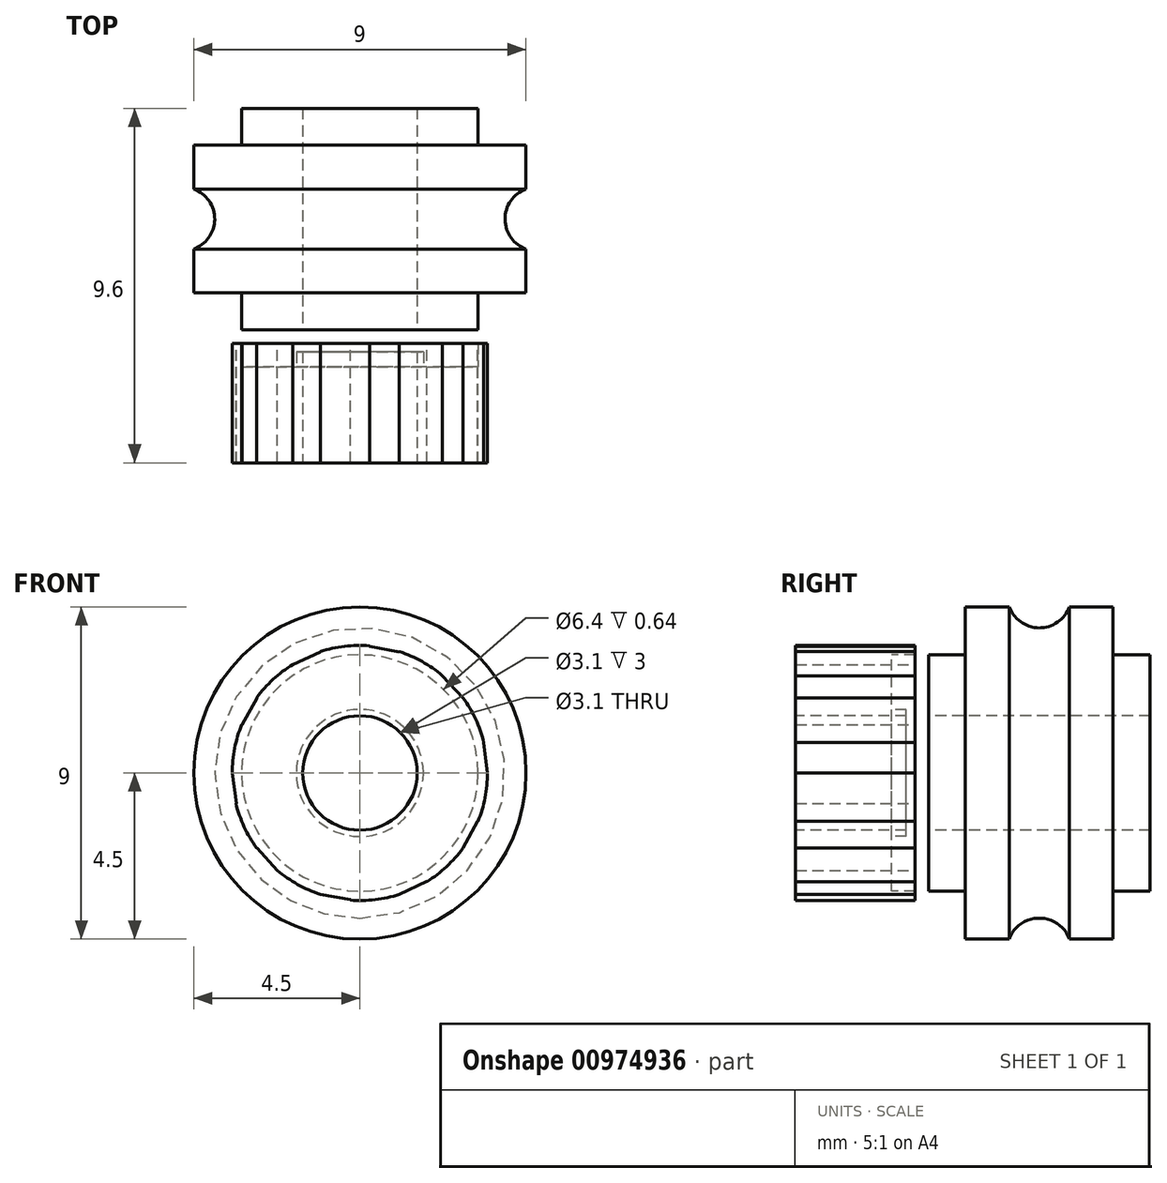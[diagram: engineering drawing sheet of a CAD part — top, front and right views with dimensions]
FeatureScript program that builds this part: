
annotation { "Feature Type Name" : "Feature", "Feature Type Description" : "" }
export const myFeature = defineFeature(function(context is Context, id is Id, definition is map)
    precondition{}
    {
        {
            var Q0;
            Q0=qCreatedBy(makeId("Front.planeOp"),FACE);
            var sketch = newSketch(context, id + "F0", { "sketchPlane" : qUnion([Q0])});
            skCircle(sketch, "E0", {"center": v(0, 0) * mm, "radius": 1.5 * mm});
            skCircle(sketch, "E1", {"center": v(0, 0) * mm, "radius": 4.5 * mm});
            skSolve(sketch);
        }
        {
            var Q0;
            Q0=makeQuery(id+"F0.imprint","IMPRINT",FACE,{"disambiguationData":[TD([[makeQuery(id+"F0.imprint","IMPRINT",EDGE,{"derivedFrom":sQuery(id+"F0.wireOp",EDGE,"E0")}),-1.0]])]});
            extrude(context, id + "F1", {"entities" : qUnion([Q0]), "endBound" : BoundingType.SYMMETRIC, "depth" : 11 * mm});
        }
        {
            var Q0;
            Q0=qCreatedBy(makeId("Right.planeOp"),FACE);
            var sketch = newSketch(context, id + "F2", { "sketchPlane" : qUnion([Q0])});
            skLineSegment(sketch, "E2", {"start": v(5.5, 0) * mm, "end": v(-5.5, 0) * mm, "construction": true});
            skLineSegment(sketch, "E3", {"start": v(3.2, 0) * mm, "end": v(3.2, 4.5) * mm});
            skLineSegment(sketch, "E4", {"start": v(-2.16, 4.5) * mm, "end": v(-0.84, 4.5) * mm, "construction": true});
            skPoint(sketch, "E5", {"position": v(-1.5, 4.6) * mm});
            skCircle(sketch, "E6", {"center": v(-1.5, 4.8) * mm, "radius": 0.87 * mm});
            skSolve(sketch);
        }
        {
            var Q0;
            Q0=makeQuery(id+"F2.imprint","IMPRINT",FACE,{"disambiguationData":[TD([[makeQuery(id+"F2.imprint","IMPRINT",EDGE,{"derivedFrom":sQuery(id+"F2.wireOp",EDGE,"jA4JG8t2-koIH-J3Tn-0CPV-hgkhpaPEa3mh")}),1.0]])]});
            var Q1;
            Q1=makeQuery(id+"F2.imprint","IMPRINT",FACE,{"disambiguationData":[TD([[makeQuery(id+"F2.imprint","IMPRINT",EDGE,{"derivedFrom":sQuery(id+"F2.wireOp",EDGE,"E6")}),1.0]])]});
            var Q2;
            Q2=sQuery(id+"F2.wireOp",EDGE,"E2");
            revolve(context, id + "F3", {"operationType" : NewBodyOperationType.REMOVE, "surfaceOperationType" : NewSurfaceOperationType.NEW, "entities" : qUnion([Q0, Q1]), "axis" : qUnion([Q2]), "revolveType" : RevolveType.FULL, "oppositeDirection" : true});
        }
        {
            var Q0;
            Q0=sQuery(id+"F2.wireOp",VERTEX,"E3.end");
            var Q1;
            Q1=sQuery(id+"F2.wireOp",EDGE,"E3");
            cPlane(context, id + "F4", {"entities" : qUnion([Q0, Q1]), "cplaneType" : CPlaneType.LINE_POINT, "offset" : 25 * mm, "width" : 150 * mm, "height" : 150 * mm});
        }
        {
            var Q0;
            Q0=qCreatedBy(id+"F4.planeOp",FACE);
            var sketch = newSketch(context, id + "F5", { "sketchPlane" : qUnion([Q0])});
            skPoint(sketch, "E7.0", {"position": v(0, 3.2) * mm});
            skSolve(sketch);
        }
        {
            var Q0;
            Q0=makeQuery(id+"F1.opExtrude","CAP_FACE",FACE,{"disambiguationData":[OSD([sQuery(id+"F0.wireOp",EDGE,"E0"),sQuery(id+"F0.wireOp",EDGE,"E1")])],"isStart":false});
            var sketch = newSketch(context, id + "F6", { "sketchPlane" : qUnion([Q0])});
            skPoint(sketch, "E8.center", {"position": v(0, 0) * mm});
            skCircle(sketch, "E9", {"center": v(0, 0) * mm, "radius": 2.24 * mm});
            skArc(sketch, "E10", {"start": v(2.65, 3.64) * mm, "mid": v(1.1, 3.37) * mm, "end": v(0, 2.24) * mm});
            skArc(sketch, "E11", {"start": v(2.65, 3.64) * mm, "mid": v(1.73, 2.67) * mm, "end": v(1.79, 1.34) * mm});
            skArc(sketch, "E12.1.0", {"start": v(0, 4.5) * mm, "mid": v(-1.09, 3.37) * mm, "end": v(-1.31, 1.8) * mm});
            skArc(sketch, "E12.1.1", {"start": v(0, 4.5) * mm, "mid": v(-0.17, 3.18) * mm, "end": v(0.66, 2.14) * mm});
            skArc(sketch, "E12.2.0", {"start": v(-2.64, 3.64) * mm, "mid": v(-2.86, 2.08) * mm, "end": v(-2.13, 0.7) * mm});
            skArc(sketch, "E12.2.1", {"start": v(-2.64, 3.64) * mm, "mid": v(-2, 2.48) * mm, "end": v(-0.72, 2.12) * mm});
            skArc(sketch, "E12.3.0", {"start": v(-4.28, 1.4) * mm, "mid": v(-3.54, 0) * mm, "end": v(-2.13, -0.7) * mm});
            skArc(sketch, "E12.3.1", {"start": v(-4.28, 1.4) * mm, "mid": v(-3.08, 0.82) * mm, "end": v(-1.83, 1.29) * mm});
            skArc(sketch, "E12.4.0", {"start": v(-4.28, -1.38) * mm, "mid": v(-2.87, -2.08) * mm, "end": v(-1.31, -1.8) * mm});
            skArc(sketch, "E12.4.1", {"start": v(-4.28, -1.38) * mm, "mid": v(-2.97, -1.14) * mm, "end": v(-2.24, -0.03) * mm});
            skArc(sketch, "E12.5.0", {"start": v(-2.65, -3.64) * mm, "mid": v(-1.1, -3.37) * mm, "end": v(0, -2.24) * mm});
            skArc(sketch, "E12.5.1", {"start": v(-2.65, -3.64) * mm, "mid": v(-1.73, -2.67) * mm, "end": v(-1.79, -1.34) * mm});
            skArc(sketch, "E12.6.0", {"start": v(0, -4.5) * mm, "mid": v(1.09, -3.37) * mm, "end": v(1.31, -1.8) * mm});
            skArc(sketch, "E12.6.1", {"start": v(0, -4.5) * mm, "mid": v(0.17, -3.18) * mm, "end": v(-0.66, -2.14) * mm});
            skArc(sketch, "E12.7.0", {"start": v(2.64, -3.64) * mm, "mid": v(2.86, -2.08) * mm, "end": v(2.13, -0.7) * mm});
            skArc(sketch, "E12.7.1", {"start": v(2.64, -3.64) * mm, "mid": v(2, -2.48) * mm, "end": v(0.72, -2.12) * mm});
            skArc(sketch, "E12.8.0", {"start": v(4.28, -1.4) * mm, "mid": v(3.54, 0) * mm, "end": v(2.13, 0.7) * mm});
            skArc(sketch, "E12.8.1", {"start": v(4.28, -1.4) * mm, "mid": v(3.08, -0.82) * mm, "end": v(1.83, -1.29) * mm});
            skArc(sketch, "E12.9.0", {"start": v(4.28, 1.38) * mm, "mid": v(2.87, 2.08) * mm, "end": v(1.31, 1.8) * mm});
            skArc(sketch, "E12.9.1", {"start": v(4.28, 1.38) * mm, "mid": v(2.97, 1.14) * mm, "end": v(2.24, 0.03) * mm});
            skSolve(sketch);
        }
        {
            var Q0;
            {var subQ0=sQuery(id+"F6.wireOp",EDGE,"E12.2.0");var subQ3=sQuery(id+"F6.wireOp",EDGE,"E12.3.1");var subQ4=makeQuery(id+"F6.imprint","INTERSECT",VERTEX,{"derivedFrom":[subQ0,subQ3]});Q0=makeQuery(id+"F6.imprint","IMPRINT",FACE,{"disambiguationData":[TD([[makeQuery(id+"F6.imprint","IMPRINT",EDGE,{"disambiguationData":[TD([[subQ4,1.0]])],"derivedFrom":subQ0}),-1.0]])]});}
            var Q1;
            {var subQ0=sQuery(id+"F6.wireOp",EDGE,"E12.1.0");var subQ3=sQuery(id+"F6.wireOp",EDGE,"E12.2.1");var subQ4=makeQuery(id+"F6.imprint","INTERSECT",VERTEX,{"derivedFrom":[subQ0,subQ3]});Q1=makeQuery(id+"F6.imprint","IMPRINT",FACE,{"disambiguationData":[TD([[makeQuery(id+"F6.imprint","IMPRINT",EDGE,{"disambiguationData":[TD([[subQ4,1.0]])],"derivedFrom":subQ0}),-1.0]])]});}
            var Q2;
            {var subQ0=sQuery(id+"F6.wireOp",EDGE,"E10");var subQ3=sQuery(id+"F6.wireOp",EDGE,"E12.1.1");var subQ4=makeQuery(id+"F6.imprint","INTERSECT",VERTEX,{"derivedFrom":[subQ0,subQ3]});Q2=makeQuery(id+"F6.imprint","IMPRINT",FACE,{"disambiguationData":[TD([[makeQuery(id+"F6.imprint","IMPRINT",EDGE,{"disambiguationData":[TD([[subQ4,1.0]])],"derivedFrom":subQ0}),-1.0]])]});}
            var Q3;
            {var subQ0=sQuery(id+"F6.wireOp",EDGE,"E11");var subQ3=sQuery(id+"F6.wireOp",EDGE,"E12.9.0");var subQ4=makeQuery(id+"F6.imprint","INTERSECT",VERTEX,{"derivedFrom":[subQ0,subQ3]});Q3=makeQuery(id+"F6.imprint","IMPRINT",FACE,{"disambiguationData":[TD([[makeQuery(id+"F6.imprint","IMPRINT",EDGE,{"disambiguationData":[TD([[subQ4,1.0]])],"derivedFrom":subQ0}),1.0]])]});}
            var Q4;
            {var subQ0=sQuery(id+"F6.wireOp",EDGE,"E12.8.0");var subQ3=sQuery(id+"F6.wireOp",EDGE,"E12.9.1");var subQ4=makeQuery(id+"F6.imprint","INTERSECT",VERTEX,{"derivedFrom":[subQ0,subQ3]});Q4=makeQuery(id+"F6.imprint","IMPRINT",FACE,{"disambiguationData":[TD([[makeQuery(id+"F6.imprint","IMPRINT",EDGE,{"disambiguationData":[TD([[subQ4,1.0]])],"derivedFrom":subQ0}),-1.0]])]});}
            var Q5;
            {var subQ0=sQuery(id+"F6.wireOp",EDGE,"E12.7.0");var subQ3=sQuery(id+"F6.wireOp",EDGE,"E12.8.1");var subQ4=makeQuery(id+"F6.imprint","INTERSECT",VERTEX,{"derivedFrom":[subQ0,subQ3]});Q5=makeQuery(id+"F6.imprint","IMPRINT",FACE,{"disambiguationData":[TD([[makeQuery(id+"F6.imprint","IMPRINT",EDGE,{"disambiguationData":[TD([[subQ4,1.0]])],"derivedFrom":subQ0}),-1.0]])]});}
            var Q6;
            {var subQ0=sQuery(id+"F6.wireOp",EDGE,"E12.6.0");var subQ3=sQuery(id+"F6.wireOp",EDGE,"E12.7.1");var subQ4=makeQuery(id+"F6.imprint","INTERSECT",VERTEX,{"derivedFrom":[subQ0,subQ3]});Q6=makeQuery(id+"F6.imprint","IMPRINT",FACE,{"disambiguationData":[TD([[makeQuery(id+"F6.imprint","IMPRINT",EDGE,{"disambiguationData":[TD([[subQ4,1.0]])],"derivedFrom":subQ0}),-1.0]])]});}
            var Q7;
            {var subQ0=sQuery(id+"F6.wireOp",EDGE,"E12.5.0");var subQ3=sQuery(id+"F6.wireOp",EDGE,"E12.6.1");var subQ4=makeQuery(id+"F6.imprint","INTERSECT",VERTEX,{"derivedFrom":[subQ0,subQ3]});Q7=makeQuery(id+"F6.imprint","IMPRINT",FACE,{"disambiguationData":[TD([[makeQuery(id+"F6.imprint","IMPRINT",EDGE,{"disambiguationData":[TD([[subQ4,1.0]])],"derivedFrom":subQ0}),-1.0]])]});}
            var Q8;
            {var subQ0=sQuery(id+"F6.wireOp",EDGE,"E12.4.0");var subQ3=sQuery(id+"F6.wireOp",EDGE,"E12.5.1");var subQ4=makeQuery(id+"F6.imprint","INTERSECT",VERTEX,{"derivedFrom":[subQ0,subQ3]});Q8=makeQuery(id+"F6.imprint","IMPRINT",FACE,{"disambiguationData":[TD([[makeQuery(id+"F6.imprint","IMPRINT",EDGE,{"disambiguationData":[TD([[subQ4,1.0]])],"derivedFrom":subQ0}),-1.0]])]});}
            var Q9;
            {var subQ0=sQuery(id+"F6.wireOp",EDGE,"E12.3.0");var subQ3=sQuery(id+"F6.wireOp",EDGE,"E12.4.1");var subQ4=makeQuery(id+"F6.imprint","INTERSECT",VERTEX,{"derivedFrom":[subQ0,subQ3]});Q9=makeQuery(id+"F6.imprint","IMPRINT",FACE,{"disambiguationData":[TD([[makeQuery(id+"F6.imprint","IMPRINT",EDGE,{"disambiguationData":[TD([[subQ4,1.0]])],"derivedFrom":subQ0}),-1.0]])]});}
            extrude(context, id + "F7", {"entities" : qUnion([Q0, Q1, Q2, Q3, Q4, Q5, Q6, Q7, Q8, Q9]), "operationType" : NewBodyOperationType.ADD, "oppositeDirection" : true, "depth" : 2 * mm, "offsetDistance" : 25 * mm});
        }
        {
            var Q0;
            Q0=makeQuery(id+"F1.opExtrude","CAP_FACE",FACE,{"disambiguationData":[OSD([sQuery(id+"F0.wireOp",EDGE,"E0"),sQuery(id+"F0.wireOp",EDGE,"E1")])],"isStart":true});
            var sketch = newSketch(context, id + "F8", { "sketchPlane" : qUnion([Q0])});
            skCircle(sketch, "E13", {"center": v(0, 0) * mm, "radius": 3.2 * mm});
            skSolve(sketch);
        }
        {
            var Q0;
            Q0=makeQuery(id+"F8.imprint","IMPRINT",FACE,{"disambiguationData":[TD([[makeQuery(id+"F8.imprint","IMPRINT",EDGE,{"derivedFrom":sQuery(id+"F8.wireOp",EDGE,"E13")}),-1.0]])]});
            extrude(context, id + "F9", {"entities" : qUnion([Q0]), "operationType" : NewBodyOperationType.REMOVE, "oppositeDirection" : true, "depth" : 5 * mm, "offsetDistance" : 25 * mm});
        }
        {
            var Q0;
            Q0=makeQuery(id+"F1.opExtrude","CAP_FACE",FACE,{"disambiguationData":[OSD([sQuery(id+"F0.wireOp",EDGE,"E0"),sQuery(id+"F0.wireOp",EDGE,"E1")])],"isStart":true});
            var sketch = newSketch(context, id + "F10", { "sketchPlane" : qUnion([Q0])});
            skLineSegment(sketch, "E14", {"start": v(3.6, 0.87) * mm, "end": v(3.1, 0.76) * mm});
            skLineSegment(sketch, "E15", {"start": v(3.6, 0.88) * mm, "end": v(3.6, 0.87) * mm});
            skLineSegment(sketch, "E16", {"start": v(3.6, 0.88) * mm, "end": v(3.6, 0.88) * mm});
            skLineSegment(sketch, "E17", {"start": v(3.62, 0.88) * mm, "end": v(3.6, 0.88) * mm});
            skLineSegment(sketch, "E18", {"start": v(3.63, 0.9) * mm, "end": v(3.62, 0.88) * mm});
            skLineSegment(sketch, "E19", {"start": v(3.65, 0.9) * mm, "end": v(3.63, 0.9) * mm});
            skLineSegment(sketch, "E20", {"start": v(3.68, 0.91) * mm, "end": v(3.65, 0.9) * mm});
            skLineSegment(sketch, "E21", {"start": v(3.7, 0.93) * mm, "end": v(3.68, 0.91) * mm});
            skLineSegment(sketch, "E22", {"start": v(3.74, 0.94) * mm, "end": v(3.7, 0.93) * mm});
            skLineSegment(sketch, "E23", {"start": v(3.77, 0.96) * mm, "end": v(3.74, 0.94) * mm});
            skLineSegment(sketch, "E24", {"start": v(3.8, 0.99) * mm, "end": v(3.77, 0.96) * mm});
            skLineSegment(sketch, "E25", {"start": v(3.85, 1.02) * mm, "end": v(3.8, 0.99) * mm});
            skLineSegment(sketch, "E26", {"start": v(3.9, 1.05) * mm, "end": v(3.85, 1.02) * mm});
            skLineSegment(sketch, "E27", {"start": v(3.94, 1.09) * mm, "end": v(3.9, 1.05) * mm});
            skLineSegment(sketch, "E28", {"start": v(3.98, 1.13) * mm, "end": v(3.94, 1.09) * mm});
            skLineSegment(sketch, "E29", {"start": v(4.03, 1.18) * mm, "end": v(3.98, 1.13) * mm});
            skLineSegment(sketch, "E30", {"start": v(4.08, 1.23) * mm, "end": v(4.03, 1.18) * mm});
            skLineSegment(sketch, "E31", {"start": v(4.14, 1.29) * mm, "end": v(4.08, 1.23) * mm});
            skLineSegment(sketch, "E32", {"start": v(4.19, 1.35) * mm, "end": v(4.14, 1.29) * mm});
            skLineSegment(sketch, "E33", {"start": v(4.24, 1.41) * mm, "end": v(4.19, 1.35) * mm});
            skLineSegment(sketch, "E34", {"start": v(4.3, 1.49) * mm, "end": v(4.24, 1.41) * mm});
            skLineSegment(sketch, "E35", {"start": v(4.35, 1.57) * mm, "end": v(4.3, 1.49) * mm});
            skLineSegment(sketch, "E36", {"start": v(4.4, 1.65) * mm, "end": v(4.35, 1.57) * mm});
            skLineSegment(sketch, "E37", {"start": v(4.45, 1.74) * mm, "end": v(4.4, 1.65) * mm});
            skLineSegment(sketch, "E38", {"start": v(4.5, 1.83) * mm, "end": v(4.45, 1.74) * mm});
            skLineSegment(sketch, "E39", {"start": v(4.55, 1.93) * mm, "end": v(4.5, 1.83) * mm});
            skLineSegment(sketch, "E40", {"start": v(4.55, 2.02) * mm, "end": v(4.55, 1.93) * mm});
            skLineSegment(sketch, "E41", {"start": v(4.48, 2.16) * mm, "end": v(4.55, 2.02) * mm});
            skLineSegment(sketch, "E42", {"start": v(4.42, 2.22) * mm, "end": v(4.48, 2.16) * mm});
            skLineSegment(sketch, "E43", {"start": v(4.31, 2.25) * mm, "end": v(4.42, 2.22) * mm});
            skLineSegment(sketch, "E44", {"start": v(4.2, 2.27) * mm, "end": v(4.31, 2.25) * mm});
            skLineSegment(sketch, "E45", {"start": v(4.1, 2.29) * mm, "end": v(4.2, 2.27) * mm});
            skLineSegment(sketch, "E46", {"start": v(4, 2.3) * mm, "end": v(4.1, 2.29) * mm});
            skLineSegment(sketch, "E47", {"start": v(3.91, 2.31) * mm, "end": v(4, 2.3) * mm});
            skLineSegment(sketch, "E48", {"start": v(3.82, 2.32) * mm, "end": v(3.91, 2.31) * mm});
            skLineSegment(sketch, "E49", {"start": v(3.74, 2.32) * mm, "end": v(3.82, 2.32) * mm});
            skLineSegment(sketch, "E50", {"start": v(3.66, 2.32) * mm, "end": v(3.74, 2.32) * mm});
            skLineSegment(sketch, "E51", {"start": v(3.58, 2.32) * mm, "end": v(3.66, 2.32) * mm});
            skLineSegment(sketch, "E52", {"start": v(3.5, 2.31) * mm, "end": v(3.58, 2.32) * mm});
            skLineSegment(sketch, "E53", {"start": v(3.44, 2.3) * mm, "end": v(3.5, 2.31) * mm});
            skLineSegment(sketch, "E54", {"start": v(3.38, 2.3) * mm, "end": v(3.44, 2.3) * mm});
            skLineSegment(sketch, "E55", {"start": v(3.32, 2.29) * mm, "end": v(3.38, 2.3) * mm});
            skLineSegment(sketch, "E56", {"start": v(3.27, 2.28) * mm, "end": v(3.32, 2.29) * mm});
            skLineSegment(sketch, "E57", {"start": v(3.22, 2.26) * mm, "end": v(3.27, 2.28) * mm});
            skLineSegment(sketch, "E58", {"start": v(3.18, 2.25) * mm, "end": v(3.22, 2.26) * mm});
            skLineSegment(sketch, "E59", {"start": v(3.14, 2.24) * mm, "end": v(3.18, 2.25) * mm});
            skLineSegment(sketch, "E60", {"start": v(3.1, 2.23) * mm, "end": v(3.14, 2.24) * mm});
            skLineSegment(sketch, "E61", {"start": v(3.07, 2.22) * mm, "end": v(3.1, 2.23) * mm});
            skLineSegment(sketch, "E62", {"start": v(3.05, 2.2) * mm, "end": v(3.07, 2.22) * mm});
            skLineSegment(sketch, "E63", {"start": v(3.03, 2.2) * mm, "end": v(3.05, 2.2) * mm});
            skLineSegment(sketch, "E64", {"start": v(3.01, 2.19) * mm, "end": v(3.03, 2.2) * mm});
            skLineSegment(sketch, "E65", {"start": v(3, 2.18) * mm, "end": v(3.01, 2.19) * mm});
            skLineSegment(sketch, "E66", {"start": v(3, 2.18) * mm, "end": v(3, 2.18) * mm});
            skLineSegment(sketch, "E67", {"start": v(3, 2.17) * mm, "end": v(3, 2.18) * mm});
            skLineSegment(sketch, "E68", {"start": v(2.58, 1.88) * mm, "end": v(3, 2.17) * mm});
            skLineSegment(sketch, "E69", {"start": v(2.07, 2.44) * mm, "end": v(2.58, 1.88) * mm});
            skLineSegment(sketch, "E70", {"start": v(2.4, 2.82) * mm, "end": v(2.07, 2.44) * mm});
            skLineSegment(sketch, "E71", {"start": v(2.4, 2.82) * mm, "end": v(2.4, 2.82) * mm});
            skLineSegment(sketch, "E72", {"start": v(2.4, 2.83) * mm, "end": v(2.4, 2.82) * mm});
            skLineSegment(sketch, "E73", {"start": v(2.4, 2.84) * mm, "end": v(2.4, 2.83) * mm});
            skLineSegment(sketch, "E74", {"start": v(2.42, 2.86) * mm, "end": v(2.4, 2.84) * mm});
            skLineSegment(sketch, "E75", {"start": v(2.43, 2.88) * mm, "end": v(2.42, 2.86) * mm});
            skLineSegment(sketch, "E76", {"start": v(2.44, 2.9) * mm, "end": v(2.43, 2.88) * mm});
            skLineSegment(sketch, "E77", {"start": v(2.45, 2.93) * mm, "end": v(2.44, 2.9) * mm});
            skLineSegment(sketch, "E78", {"start": v(2.47, 2.96) * mm, "end": v(2.45, 2.93) * mm});
            skLineSegment(sketch, "E79", {"start": v(2.48, 3) * mm, "end": v(2.47, 2.96) * mm});
            skLineSegment(sketch, "E80", {"start": v(2.5, 3.04) * mm, "end": v(2.48, 3) * mm});
            skLineSegment(sketch, "E81", {"start": v(2.52, 3.09) * mm, "end": v(2.5, 3.04) * mm});
            skLineSegment(sketch, "E82", {"start": v(2.53, 3.14) * mm, "end": v(2.52, 3.09) * mm});
            skLineSegment(sketch, "E83", {"start": v(2.55, 3.2) * mm, "end": v(2.53, 3.14) * mm});
            skLineSegment(sketch, "E84", {"start": v(2.56, 3.26) * mm, "end": v(2.55, 3.2) * mm});
            skLineSegment(sketch, "E85", {"start": v(2.57, 3.32) * mm, "end": v(2.56, 3.26) * mm});
            skLineSegment(sketch, "E86", {"start": v(2.58, 3.4) * mm, "end": v(2.57, 3.32) * mm});
            skLineSegment(sketch, "E87", {"start": v(2.59, 3.47) * mm, "end": v(2.58, 3.4) * mm});
            skLineSegment(sketch, "E88", {"start": v(2.6, 3.55) * mm, "end": v(2.59, 3.47) * mm});
            skLineSegment(sketch, "E89", {"start": v(2.6, 3.64) * mm, "end": v(2.6, 3.55) * mm});
            skLineSegment(sketch, "E90", {"start": v(2.6, 3.73) * mm, "end": v(2.6, 3.64) * mm});
            skLineSegment(sketch, "E91", {"start": v(2.6, 3.82) * mm, "end": v(2.6, 3.73) * mm});
            skLineSegment(sketch, "E92", {"start": v(2.6, 3.92) * mm, "end": v(2.6, 3.82) * mm});
            skLineSegment(sketch, "E93", {"start": v(2.58, 4.02) * mm, "end": v(2.6, 3.92) * mm});
            skLineSegment(sketch, "E94", {"start": v(2.57, 4.13) * mm, "end": v(2.58, 4.02) * mm});
            skLineSegment(sketch, "E95", {"start": v(2.55, 4.24) * mm, "end": v(2.57, 4.13) * mm});
            skLineSegment(sketch, "E96", {"start": v(2.5, 4.3) * mm, "end": v(2.55, 4.24) * mm});
            skLineSegment(sketch, "E97", {"start": v(2.35, 4.39) * mm, "end": v(2.5, 4.3) * mm});
            skLineSegment(sketch, "E98", {"start": v(2.27, 4.4) * mm, "end": v(2.35, 4.39) * mm});
            skLineSegment(sketch, "E99", {"start": v(2.17, 4.35) * mm, "end": v(2.27, 4.4) * mm});
            skLineSegment(sketch, "E100", {"start": v(2.07, 4.3) * mm, "end": v(2.17, 4.35) * mm});
            skLineSegment(sketch, "E101", {"start": v(1.98, 4.26) * mm, "end": v(2.07, 4.3) * mm});
            skLineSegment(sketch, "E102", {"start": v(1.89, 4.22) * mm, "end": v(1.98, 4.26) * mm});
            skLineSegment(sketch, "E103", {"start": v(1.8, 4.17) * mm, "end": v(1.89, 4.22) * mm});
            skLineSegment(sketch, "E104", {"start": v(1.73, 4.12) * mm, "end": v(1.8, 4.17) * mm});
            skLineSegment(sketch, "E105", {"start": v(1.66, 4.07) * mm, "end": v(1.73, 4.12) * mm});
            skLineSegment(sketch, "E106", {"start": v(1.6, 4.03) * mm, "end": v(1.66, 4.07) * mm});
            skLineSegment(sketch, "E107", {"start": v(1.53, 3.98) * mm, "end": v(1.6, 4.03) * mm});
            skLineSegment(sketch, "E108", {"start": v(1.48, 3.93) * mm, "end": v(1.53, 3.98) * mm});
            skLineSegment(sketch, "E109", {"start": v(1.43, 3.89) * mm, "end": v(1.48, 3.93) * mm});
            skLineSegment(sketch, "E110", {"start": v(1.38, 3.84) * mm, "end": v(1.43, 3.89) * mm});
            skLineSegment(sketch, "E111", {"start": v(1.34, 3.8) * mm, "end": v(1.38, 3.84) * mm});
            skLineSegment(sketch, "E112", {"start": v(1.3, 3.76) * mm, "end": v(1.34, 3.8) * mm});
            skLineSegment(sketch, "E113", {"start": v(1.27, 3.72) * mm, "end": v(1.3, 3.76) * mm});
            skLineSegment(sketch, "E114", {"start": v(1.25, 3.69) * mm, "end": v(1.27, 3.72) * mm});
            skLineSegment(sketch, "E115", {"start": v(1.22, 3.66) * mm, "end": v(1.25, 3.69) * mm});
            skLineSegment(sketch, "E116", {"start": v(1.2, 3.63) * mm, "end": v(1.22, 3.66) * mm});
            skLineSegment(sketch, "E117", {"start": v(1.18, 3.6) * mm, "end": v(1.2, 3.63) * mm});
            skLineSegment(sketch, "E118", {"start": v(1.17, 3.58) * mm, "end": v(1.18, 3.6) * mm});
            skLineSegment(sketch, "E119", {"start": v(1.16, 3.56) * mm, "end": v(1.17, 3.58) * mm});
            skLineSegment(sketch, "E120", {"start": v(1.15, 3.54) * mm, "end": v(1.16, 3.56) * mm});
            skLineSegment(sketch, "E121", {"start": v(1.15, 3.53) * mm, "end": v(1.15, 3.54) * mm});
            skLineSegment(sketch, "E122", {"start": v(1.14, 3.52) * mm, "end": v(1.15, 3.53) * mm});
            skLineSegment(sketch, "E123", {"start": v(1.14, 3.52) * mm, "end": v(1.14, 3.52) * mm});
            skLineSegment(sketch, "E124", {"start": v(0.99, 3.04) * mm, "end": v(1.14, 3.52) * mm});
            skLineSegment(sketch, "E125", {"start": v(0.24, 3.18) * mm, "end": v(0.99, 3.04) * mm});
            skLineSegment(sketch, "E126", {"start": v(0.28, 3.69) * mm, "end": v(0.24, 3.18) * mm});
            skLineSegment(sketch, "E127", {"start": v(0.28, 3.7) * mm, "end": v(0.28, 3.69) * mm});
            skLineSegment(sketch, "E128", {"start": v(0.28, 3.7) * mm, "end": v(0.28, 3.7) * mm});
            skLineSegment(sketch, "E129", {"start": v(0.28, 3.71) * mm, "end": v(0.28, 3.7) * mm});
            skLineSegment(sketch, "E130", {"start": v(0.28, 3.73) * mm, "end": v(0.28, 3.71) * mm});
            skLineSegment(sketch, "E131", {"start": v(0.27, 3.75) * mm, "end": v(0.28, 3.73) * mm});
            skLineSegment(sketch, "E132", {"start": v(0.27, 3.78) * mm, "end": v(0.27, 3.75) * mm});
            skLineSegment(sketch, "E133", {"start": v(0.27, 3.81) * mm, "end": v(0.27, 3.78) * mm});
            skLineSegment(sketch, "E134", {"start": v(0.26, 3.85) * mm, "end": v(0.27, 3.81) * mm});
            skLineSegment(sketch, "E135", {"start": v(0.25, 3.89) * mm, "end": v(0.26, 3.85) * mm});
            skLineSegment(sketch, "E136", {"start": v(0.24, 3.93) * mm, "end": v(0.25, 3.89) * mm});
            skLineSegment(sketch, "E137", {"start": v(0.22, 3.98) * mm, "end": v(0.24, 3.93) * mm});
            skLineSegment(sketch, "E138", {"start": v(0.2, 4.03) * mm, "end": v(0.22, 3.98) * mm});
            skLineSegment(sketch, "E139", {"start": v(0.18, 4.08) * mm, "end": v(0.2, 4.03) * mm});
            skLineSegment(sketch, "E140", {"start": v(0.16, 4.14) * mm, "end": v(0.18, 4.08) * mm});
            skLineSegment(sketch, "E141", {"start": v(0.13, 4.2) * mm, "end": v(0.16, 4.14) * mm});
            skLineSegment(sketch, "E142", {"start": v(0.1, 4.26) * mm, "end": v(0.13, 4.2) * mm});
            skLineSegment(sketch, "E143", {"start": v(0.05, 4.33) * mm, "end": v(0.1, 4.26) * mm});
            skLineSegment(sketch, "E144", {"start": v(0.01, 4.4) * mm, "end": v(0.05, 4.33) * mm});
            skLineSegment(sketch, "E145", {"start": v(-0.04, 4.47) * mm, "end": v(0.01, 4.4) * mm});
            skLineSegment(sketch, "E146", {"start": v(-0.09, 4.54) * mm, "end": v(-0.04, 4.47) * mm});
            skLineSegment(sketch, "E147", {"start": v(-0.15, 4.62) * mm, "end": v(-0.09, 4.54) * mm});
            skLineSegment(sketch, "E148", {"start": v(-0.2, 4.7) * mm, "end": v(-0.15, 4.62) * mm});
            skLineSegment(sketch, "E149", {"start": v(-0.28, 4.77) * mm, "end": v(-0.2, 4.7) * mm});
            skLineSegment(sketch, "E150", {"start": v(-0.35, 4.85) * mm, "end": v(-0.28, 4.77) * mm});
            skLineSegment(sketch, "E151", {"start": v(-0.43, 4.93) * mm, "end": v(-0.35, 4.85) * mm});
            skLineSegment(sketch, "E152", {"start": v(-0.51, 4.95) * mm, "end": v(-0.43, 4.93) * mm});
            skLineSegment(sketch, "E153", {"start": v(-0.67, 4.93) * mm, "end": v(-0.51, 4.95) * mm});
            skLineSegment(sketch, "E154", {"start": v(-0.75, 4.9) * mm, "end": v(-0.67, 4.93) * mm});
            skLineSegment(sketch, "E155", {"start": v(-0.8, 4.8) * mm, "end": v(-0.75, 4.9) * mm});
            skLineSegment(sketch, "E156", {"start": v(-0.86, 4.7) * mm, "end": v(-0.8, 4.8) * mm});
            skLineSegment(sketch, "E157", {"start": v(-0.9, 4.61) * mm, "end": v(-0.86, 4.7) * mm});
            skLineSegment(sketch, "E158", {"start": v(-0.95, 4.52) * mm, "end": v(-0.9, 4.61) * mm});
            skLineSegment(sketch, "E159", {"start": v(-1, 4.44) * mm, "end": v(-0.95, 4.52) * mm});
            skLineSegment(sketch, "E160", {"start": v(-1.02, 4.35) * mm, "end": v(-1, 4.44) * mm});
            skLineSegment(sketch, "E161", {"start": v(-1.05, 4.27) * mm, "end": v(-1.02, 4.35) * mm});
            skLineSegment(sketch, "E162", {"start": v(-1.08, 4.2) * mm, "end": v(-1.05, 4.27) * mm});
            skLineSegment(sketch, "E163", {"start": v(-1.1, 4.12) * mm, "end": v(-1.08, 4.2) * mm});
            skLineSegment(sketch, "E164", {"start": v(-1.12, 4.05) * mm, "end": v(-1.1, 4.12) * mm});
            skLineSegment(sketch, "E165", {"start": v(-1.13, 3.98) * mm, "end": v(-1.12, 4.05) * mm});
            skLineSegment(sketch, "E166", {"start": v(-1.14, 3.92) * mm, "end": v(-1.13, 3.98) * mm});
            skLineSegment(sketch, "E167", {"start": v(-1.15, 3.86) * mm, "end": v(-1.14, 3.92) * mm});
            skLineSegment(sketch, "E168", {"start": v(-1.16, 3.81) * mm, "end": v(-1.15, 3.86) * mm});
            skLineSegment(sketch, "E169", {"start": v(-1.16, 3.76) * mm, "end": v(-1.16, 3.81) * mm});
            skLineSegment(sketch, "E170", {"start": v(-1.16, 3.72) * mm, "end": v(-1.16, 3.76) * mm});
            skLineSegment(sketch, "E171", {"start": v(-1.16, 3.68) * mm, "end": v(-1.16, 3.72) * mm});
            skLineSegment(sketch, "E172", {"start": v(-1.16, 3.64) * mm, "end": v(-1.16, 3.68) * mm});
            skLineSegment(sketch, "E173", {"start": v(-1.16, 3.6) * mm, "end": v(-1.16, 3.64) * mm});
            skLineSegment(sketch, "E174", {"start": v(-1.15, 3.58) * mm, "end": v(-1.16, 3.6) * mm});
            skLineSegment(sketch, "E175", {"start": v(-1.15, 3.56) * mm, "end": v(-1.15, 3.58) * mm});
            skLineSegment(sketch, "E176", {"start": v(-1.15, 3.54) * mm, "end": v(-1.15, 3.56) * mm});
            skLineSegment(sketch, "E177", {"start": v(-1.15, 3.53) * mm, "end": v(-1.15, 3.54) * mm});
            skLineSegment(sketch, "E178", {"start": v(-1.14, 3.52) * mm, "end": v(-1.15, 3.53) * mm});
            skLineSegment(sketch, "E179", {"start": v(-1.14, 3.52) * mm, "end": v(-1.14, 3.52) * mm});
            skLineSegment(sketch, "E180", {"start": v(-0.99, 3.04) * mm, "end": v(-1.14, 3.52) * mm});
            skLineSegment(sketch, "E181", {"start": v(-1.68, 2.72) * mm, "end": v(-0.99, 3.04) * mm});
            skLineSegment(sketch, "E182", {"start": v(-1.94, 3.15) * mm, "end": v(-1.68, 2.72) * mm});
            skLineSegment(sketch, "E183", {"start": v(-1.94, 3.15) * mm, "end": v(-1.94, 3.15) * mm});
            skLineSegment(sketch, "E184", {"start": v(-1.95, 3.16) * mm, "end": v(-1.94, 3.15) * mm});
            skLineSegment(sketch, "E185", {"start": v(-1.96, 3.17) * mm, "end": v(-1.95, 3.16) * mm});
            skLineSegment(sketch, "E186", {"start": v(-1.97, 3.18) * mm, "end": v(-1.96, 3.17) * mm});
            skLineSegment(sketch, "E187", {"start": v(-1.98, 3.2) * mm, "end": v(-1.97, 3.18) * mm});
            skLineSegment(sketch, "E188", {"start": v(-2, 3.22) * mm, "end": v(-1.98, 3.2) * mm});
            skLineSegment(sketch, "E189", {"start": v(-2.03, 3.24) * mm, "end": v(-2, 3.22) * mm});
            skLineSegment(sketch, "E190", {"start": v(-2.05, 3.26) * mm, "end": v(-2.03, 3.24) * mm});
            skLineSegment(sketch, "E191", {"start": v(-2.08, 3.29) * mm, "end": v(-2.05, 3.26) * mm});
            skLineSegment(sketch, "E192", {"start": v(-2.12, 3.32) * mm, "end": v(-2.08, 3.29) * mm});
            skLineSegment(sketch, "E193", {"start": v(-2.16, 3.35) * mm, "end": v(-2.12, 3.32) * mm});
            skLineSegment(sketch, "E194", {"start": v(-2.2, 3.38) * mm, "end": v(-2.16, 3.35) * mm});
            skLineSegment(sketch, "E195", {"start": v(-2.25, 3.4) * mm, "end": v(-2.2, 3.38) * mm});
            skLineSegment(sketch, "E196", {"start": v(-2.3, 3.44) * mm, "end": v(-2.25, 3.4) * mm});
            skLineSegment(sketch, "E197", {"start": v(-2.37, 3.47) * mm, "end": v(-2.3, 3.44) * mm});
            skLineSegment(sketch, "E198", {"start": v(-2.43, 3.5) * mm, "end": v(-2.37, 3.47) * mm});
            skLineSegment(sketch, "E199", {"start": v(-2.5, 3.54) * mm, "end": v(-2.43, 3.5) * mm});
            skLineSegment(sketch, "E200", {"start": v(-2.58, 3.57) * mm, "end": v(-2.5, 3.54) * mm});
            skLineSegment(sketch, "E201", {"start": v(-2.66, 3.6) * mm, "end": v(-2.58, 3.57) * mm});
            skLineSegment(sketch, "E202", {"start": v(-2.74, 3.62) * mm, "end": v(-2.66, 3.6) * mm});
            skLineSegment(sketch, "E203", {"start": v(-2.83, 3.65) * mm, "end": v(-2.74, 3.62) * mm});
            skLineSegment(sketch, "E204", {"start": v(-2.93, 3.68) * mm, "end": v(-2.83, 3.65) * mm});
            skLineSegment(sketch, "E205", {"start": v(-3.03, 3.7) * mm, "end": v(-2.93, 3.68) * mm});
            skLineSegment(sketch, "E206", {"start": v(-3.14, 3.72) * mm, "end": v(-3.03, 3.7) * mm});
            skLineSegment(sketch, "E207", {"start": v(-3.25, 3.73) * mm, "end": v(-3.14, 3.72) * mm});
            skLineSegment(sketch, "E208", {"start": v(-3.33, 3.7) * mm, "end": v(-3.25, 3.73) * mm});
            skLineSegment(sketch, "E209", {"start": v(-3.44, 3.6) * mm, "end": v(-3.33, 3.7) * mm});
            skLineSegment(sketch, "E210", {"start": v(-3.48, 3.52) * mm, "end": v(-3.44, 3.6) * mm});
            skLineSegment(sketch, "E211", {"start": v(-3.47, 3.4) * mm, "end": v(-3.48, 3.52) * mm});
            skLineSegment(sketch, "E212", {"start": v(-3.46, 3.3) * mm, "end": v(-3.47, 3.4) * mm});
            skLineSegment(sketch, "E213", {"start": v(-3.45, 3.2) * mm, "end": v(-3.46, 3.3) * mm});
            skLineSegment(sketch, "E214", {"start": v(-3.43, 3.1) * mm, "end": v(-3.45, 3.2) * mm});
            skLineSegment(sketch, "E215", {"start": v(-3.4, 3) * mm, "end": v(-3.43, 3.1) * mm});
            skLineSegment(sketch, "E216", {"start": v(-3.39, 2.92) * mm, "end": v(-3.4, 3) * mm});
            skLineSegment(sketch, "E217", {"start": v(-3.36, 2.84) * mm, "end": v(-3.39, 2.92) * mm});
            skLineSegment(sketch, "E218", {"start": v(-3.34, 2.76) * mm, "end": v(-3.36, 2.84) * mm});
            skLineSegment(sketch, "E219", {"start": v(-3.31, 2.69) * mm, "end": v(-3.34, 2.76) * mm});
            skLineSegment(sketch, "E220", {"start": v(-3.28, 2.62) * mm, "end": v(-3.31, 2.69) * mm});
            skLineSegment(sketch, "E221", {"start": v(-3.26, 2.56) * mm, "end": v(-3.28, 2.62) * mm});
            skLineSegment(sketch, "E222", {"start": v(-3.23, 2.5) * mm, "end": v(-3.26, 2.56) * mm});
            skLineSegment(sketch, "E223", {"start": v(-3.2, 2.45) * mm, "end": v(-3.23, 2.5) * mm});
            skLineSegment(sketch, "E224", {"start": v(-3.18, 2.4) * mm, "end": v(-3.2, 2.45) * mm});
            skLineSegment(sketch, "E225", {"start": v(-3.15, 2.36) * mm, "end": v(-3.18, 2.4) * mm});
            skLineSegment(sketch, "E226", {"start": v(-3.12, 2.32) * mm, "end": v(-3.15, 2.36) * mm});
            skLineSegment(sketch, "E227", {"start": v(-3.1, 2.3) * mm, "end": v(-3.12, 2.32) * mm});
            skLineSegment(sketch, "E228", {"start": v(-3.08, 2.26) * mm, "end": v(-3.1, 2.3) * mm});
            skLineSegment(sketch, "E229", {"start": v(-3.06, 2.24) * mm, "end": v(-3.08, 2.26) * mm});
            skLineSegment(sketch, "E230", {"start": v(-3.04, 2.22) * mm, "end": v(-3.06, 2.24) * mm});
            skLineSegment(sketch, "E231", {"start": v(-3.02, 2.2) * mm, "end": v(-3.04, 2.22) * mm});
            skLineSegment(sketch, "E232", {"start": v(-3.01, 2.2) * mm, "end": v(-3.02, 2.2) * mm});
            skLineSegment(sketch, "E233", {"start": v(-3, 2.18) * mm, "end": v(-3.01, 2.2) * mm});
            skLineSegment(sketch, "E234", {"start": v(-3, 2.18) * mm, "end": v(-3, 2.18) * mm});
            skLineSegment(sketch, "E235", {"start": v(-3, 2.17) * mm, "end": v(-3, 2.18) * mm});
            skLineSegment(sketch, "E236", {"start": v(-2.58, 1.88) * mm, "end": v(-3, 2.17) * mm});
            skLineSegment(sketch, "E237", {"start": v(-2.95, 1.21) * mm, "end": v(-2.58, 1.88) * mm});
            skLineSegment(sketch, "E238", {"start": v(-3.42, 1.4) * mm, "end": v(-2.95, 1.21) * mm});
            skLineSegment(sketch, "E239", {"start": v(-3.42, 1.4) * mm, "end": v(-3.42, 1.4) * mm});
            skLineSegment(sketch, "E240", {"start": v(-3.43, 1.4) * mm, "end": v(-3.42, 1.4) * mm});
            skLineSegment(sketch, "E241", {"start": v(-3.45, 1.41) * mm, "end": v(-3.43, 1.4) * mm});
            skLineSegment(sketch, "E242", {"start": v(-3.46, 1.42) * mm, "end": v(-3.45, 1.41) * mm});
            skLineSegment(sketch, "E243", {"start": v(-3.48, 1.42) * mm, "end": v(-3.46, 1.42) * mm});
            skLineSegment(sketch, "E244", {"start": v(-3.51, 1.43) * mm, "end": v(-3.48, 1.42) * mm});
            skLineSegment(sketch, "E245", {"start": v(-3.54, 1.43) * mm, "end": v(-3.51, 1.43) * mm});
            skLineSegment(sketch, "E246", {"start": v(-3.58, 1.43) * mm, "end": v(-3.54, 1.43) * mm});
            skLineSegment(sketch, "E247", {"start": v(-3.62, 1.44) * mm, "end": v(-3.58, 1.43) * mm});
            skLineSegment(sketch, "E248", {"start": v(-3.66, 1.44) * mm, "end": v(-3.62, 1.44) * mm});
            skLineSegment(sketch, "E249", {"start": v(-3.71, 1.44) * mm, "end": v(-3.66, 1.44) * mm});
            skLineSegment(sketch, "E250", {"start": v(-3.77, 1.44) * mm, "end": v(-3.71, 1.44) * mm});
            skLineSegment(sketch, "E251", {"start": v(-3.83, 1.43) * mm, "end": v(-3.77, 1.44) * mm});
            skLineSegment(sketch, "E252", {"start": v(-3.89, 1.43) * mm, "end": v(-3.83, 1.43) * mm});
            skLineSegment(sketch, "E253", {"start": v(-3.96, 1.42) * mm, "end": v(-3.89, 1.43) * mm});
            skLineSegment(sketch, "E254", {"start": v(-4.03, 1.4) * mm, "end": v(-3.96, 1.42) * mm});
            skLineSegment(sketch, "E255", {"start": v(-4.1, 1.4) * mm, "end": v(-4.03, 1.4) * mm});
            skLineSegment(sketch, "E256", {"start": v(-4.18, 1.37) * mm, "end": v(-4.1, 1.4) * mm});
            skLineSegment(sketch, "E257", {"start": v(-4.26, 1.35) * mm, "end": v(-4.18, 1.37) * mm});
            skLineSegment(sketch, "E258", {"start": v(-4.35, 1.32) * mm, "end": v(-4.26, 1.35) * mm});
            skLineSegment(sketch, "E259", {"start": v(-4.44, 1.29) * mm, "end": v(-4.35, 1.32) * mm});
            skLineSegment(sketch, "E260", {"start": v(-4.53, 1.25) * mm, "end": v(-4.44, 1.29) * mm});
            skLineSegment(sketch, "E261", {"start": v(-4.62, 1.21) * mm, "end": v(-4.53, 1.25) * mm});
            skLineSegment(sketch, "E262", {"start": v(-4.72, 1.16) * mm, "end": v(-4.62, 1.21) * mm});
            skLineSegment(sketch, "E263", {"start": v(-4.82, 1.11) * mm, "end": v(-4.72, 1.16) * mm});
            skLineSegment(sketch, "E264", {"start": v(-4.87, 1.04) * mm, "end": v(-4.82, 1.11) * mm});
            skLineSegment(sketch, "E265", {"start": v(-4.9, 0.88) * mm, "end": v(-4.87, 1.04) * mm});
            skLineSegment(sketch, "E266", {"start": v(-4.88, 0.8) * mm, "end": v(-4.9, 0.88) * mm});
            skLineSegment(sketch, "E267", {"start": v(-4.8, 0.72) * mm, "end": v(-4.88, 0.8) * mm});
            skLineSegment(sketch, "E268", {"start": v(-4.74, 0.64) * mm, "end": v(-4.8, 0.72) * mm});
            skLineSegment(sketch, "E269", {"start": v(-4.67, 0.56) * mm, "end": v(-4.74, 0.64) * mm});
            skLineSegment(sketch, "E270", {"start": v(-4.6, 0.5) * mm, "end": v(-4.67, 0.56) * mm});
            skLineSegment(sketch, "E271", {"start": v(-4.52, 0.43) * mm, "end": v(-4.6, 0.5) * mm});
            skLineSegment(sketch, "E272", {"start": v(-4.46, 0.37) * mm, "end": v(-4.52, 0.43) * mm});
            skLineSegment(sketch, "E273", {"start": v(-4.39, 0.32) * mm, "end": v(-4.46, 0.37) * mm});
            skLineSegment(sketch, "E274", {"start": v(-4.32, 0.27) * mm, "end": v(-4.39, 0.32) * mm});
            skLineSegment(sketch, "E275", {"start": v(-4.26, 0.23) * mm, "end": v(-4.32, 0.27) * mm});
            skLineSegment(sketch, "E276", {"start": v(-4.2, 0.19) * mm, "end": v(-4.26, 0.23) * mm});
            skLineSegment(sketch, "E277", {"start": v(-4.14, 0.16) * mm, "end": v(-4.2, 0.19) * mm});
            skLineSegment(sketch, "E278", {"start": v(-4.08, 0.13) * mm, "end": v(-4.14, 0.16) * mm});
            skLineSegment(sketch, "E279", {"start": v(-4.03, 0.1) * mm, "end": v(-4.08, 0.13) * mm});
            skLineSegment(sketch, "E280", {"start": v(-3.98, 0.08) * mm, "end": v(-4.03, 0.1) * mm});
            skLineSegment(sketch, "E281", {"start": v(-3.94, 0.06) * mm, "end": v(-3.98, 0.08) * mm});
            skLineSegment(sketch, "E282", {"start": v(-3.9, 0.04) * mm, "end": v(-3.94, 0.06) * mm});
            skLineSegment(sketch, "E283", {"start": v(-3.85, 0.03) * mm, "end": v(-3.9, 0.04) * mm});
            skLineSegment(sketch, "E284", {"start": v(-3.82, 0.02) * mm, "end": v(-3.85, 0.03) * mm});
            skLineSegment(sketch, "E285", {"start": v(-3.79, 0.01) * mm, "end": v(-3.82, 0.02) * mm});
            skLineSegment(sketch, "E286", {"start": v(-3.76, 0) * mm, "end": v(-3.79, 0.01) * mm});
            skLineSegment(sketch, "E287", {"start": v(-3.74, 0) * mm, "end": v(-3.76, 0) * mm});
            skLineSegment(sketch, "E288", {"start": v(-3.72, 0) * mm, "end": v(-3.74, 0) * mm});
            skLineSegment(sketch, "E289", {"start": v(-3.7, 0) * mm, "end": v(-3.72, 0) * mm});
            skLineSegment(sketch, "E290", {"start": v(-3.7, 0) * mm, "end": v(-3.7, 0) * mm});
            skLineSegment(sketch, "E291", {"start": v(-3.2, 0) * mm, "end": v(-3.7, 0) * mm});
            skLineSegment(sketch, "E292", {"start": v(-3.1, -0.76) * mm, "end": v(-3.2, 0) * mm});
            skLineSegment(sketch, "E293", {"start": v(-3.6, -0.87) * mm, "end": v(-3.1, -0.76) * mm});
            skLineSegment(sketch, "E294", {"start": v(-3.6, -0.88) * mm, "end": v(-3.6, -0.87) * mm});
            skLineSegment(sketch, "E295", {"start": v(-3.6, -0.88) * mm, "end": v(-3.6, -0.88) * mm});
            skLineSegment(sketch, "E296", {"start": v(-3.62, -0.88) * mm, "end": v(-3.6, -0.88) * mm});
            skLineSegment(sketch, "E297", {"start": v(-3.63, -0.9) * mm, "end": v(-3.62, -0.88) * mm});
            skLineSegment(sketch, "E298", {"start": v(-3.65, -0.9) * mm, "end": v(-3.63, -0.9) * mm});
            skLineSegment(sketch, "E299", {"start": v(-3.68, -0.91) * mm, "end": v(-3.65, -0.9) * mm});
            skLineSegment(sketch, "E300", {"start": v(-3.7, -0.93) * mm, "end": v(-3.68, -0.91) * mm});
            skLineSegment(sketch, "E301", {"start": v(-3.74, -0.94) * mm, "end": v(-3.7, -0.93) * mm});
            skLineSegment(sketch, "E302", {"start": v(-3.77, -0.96) * mm, "end": v(-3.74, -0.94) * mm});
            skLineSegment(sketch, "E303", {"start": v(-3.8, -0.99) * mm, "end": v(-3.77, -0.96) * mm});
            skLineSegment(sketch, "E304", {"start": v(-3.85, -1.02) * mm, "end": v(-3.8, -0.99) * mm});
            skLineSegment(sketch, "E305", {"start": v(-3.9, -1.05) * mm, "end": v(-3.85, -1.02) * mm});
            skLineSegment(sketch, "E306", {"start": v(-3.94, -1.09) * mm, "end": v(-3.9, -1.05) * mm});
            skLineSegment(sketch, "E307", {"start": v(-3.98, -1.13) * mm, "end": v(-3.94, -1.09) * mm});
            skLineSegment(sketch, "E308", {"start": v(-4.03, -1.18) * mm, "end": v(-3.98, -1.13) * mm});
            skLineSegment(sketch, "E309", {"start": v(-4.08, -1.23) * mm, "end": v(-4.03, -1.18) * mm});
            skLineSegment(sketch, "E310", {"start": v(-4.14, -1.29) * mm, "end": v(-4.08, -1.23) * mm});
            skLineSegment(sketch, "E311", {"start": v(-4.19, -1.35) * mm, "end": v(-4.14, -1.29) * mm});
            skLineSegment(sketch, "E312", {"start": v(-4.24, -1.41) * mm, "end": v(-4.19, -1.35) * mm});
            skLineSegment(sketch, "E313", {"start": v(-4.3, -1.49) * mm, "end": v(-4.24, -1.41) * mm});
            skLineSegment(sketch, "E314", {"start": v(-4.35, -1.57) * mm, "end": v(-4.3, -1.49) * mm});
            skLineSegment(sketch, "E315", {"start": v(-4.4, -1.65) * mm, "end": v(-4.35, -1.57) * mm});
            skLineSegment(sketch, "E316", {"start": v(-4.45, -1.74) * mm, "end": v(-4.4, -1.65) * mm});
            skLineSegment(sketch, "E317", {"start": v(-4.5, -1.83) * mm, "end": v(-4.45, -1.74) * mm});
            skLineSegment(sketch, "E318", {"start": v(-4.55, -1.93) * mm, "end": v(-4.5, -1.83) * mm});
            skLineSegment(sketch, "E319", {"start": v(-4.55, -2.02) * mm, "end": v(-4.55, -1.93) * mm});
            skLineSegment(sketch, "E320", {"start": v(-4.48, -2.16) * mm, "end": v(-4.55, -2.02) * mm});
            skLineSegment(sketch, "E321", {"start": v(-4.42, -2.22) * mm, "end": v(-4.48, -2.16) * mm});
            skLineSegment(sketch, "E322", {"start": v(-4.31, -2.25) * mm, "end": v(-4.42, -2.22) * mm});
            skLineSegment(sketch, "E323", {"start": v(-4.2, -2.27) * mm, "end": v(-4.31, -2.25) * mm});
            skLineSegment(sketch, "E324", {"start": v(-4.1, -2.29) * mm, "end": v(-4.2, -2.27) * mm});
            skLineSegment(sketch, "E325", {"start": v(-4, -2.3) * mm, "end": v(-4.1, -2.29) * mm});
            skLineSegment(sketch, "E326", {"start": v(-3.91, -2.31) * mm, "end": v(-4, -2.3) * mm});
            skLineSegment(sketch, "E327", {"start": v(-3.82, -2.32) * mm, "end": v(-3.91, -2.31) * mm});
            skLineSegment(sketch, "E328", {"start": v(-3.74, -2.32) * mm, "end": v(-3.82, -2.32) * mm});
            skLineSegment(sketch, "E329", {"start": v(-3.66, -2.32) * mm, "end": v(-3.74, -2.32) * mm});
            skLineSegment(sketch, "E330", {"start": v(-3.58, -2.32) * mm, "end": v(-3.66, -2.32) * mm});
            skLineSegment(sketch, "E331", {"start": v(-3.5, -2.31) * mm, "end": v(-3.58, -2.32) * mm});
            skLineSegment(sketch, "E332", {"start": v(-3.44, -2.3) * mm, "end": v(-3.5, -2.31) * mm});
            skLineSegment(sketch, "E333", {"start": v(-3.38, -2.3) * mm, "end": v(-3.44, -2.3) * mm});
            skLineSegment(sketch, "E334", {"start": v(-3.32, -2.29) * mm, "end": v(-3.38, -2.3) * mm});
            skLineSegment(sketch, "E335", {"start": v(-3.27, -2.28) * mm, "end": v(-3.32, -2.29) * mm});
            skLineSegment(sketch, "E336", {"start": v(-3.22, -2.26) * mm, "end": v(-3.27, -2.28) * mm});
            skLineSegment(sketch, "E337", {"start": v(-3.18, -2.25) * mm, "end": v(-3.22, -2.26) * mm});
            skLineSegment(sketch, "E338", {"start": v(-3.14, -2.24) * mm, "end": v(-3.18, -2.25) * mm});
            skLineSegment(sketch, "E339", {"start": v(-3.1, -2.23) * mm, "end": v(-3.14, -2.24) * mm});
            skLineSegment(sketch, "E340", {"start": v(-3.07, -2.22) * mm, "end": v(-3.1, -2.23) * mm});
            skLineSegment(sketch, "E341", {"start": v(-3.05, -2.2) * mm, "end": v(-3.07, -2.22) * mm});
            skLineSegment(sketch, "E342", {"start": v(-3.03, -2.2) * mm, "end": v(-3.05, -2.2) * mm});
            skLineSegment(sketch, "E343", {"start": v(-3.01, -2.19) * mm, "end": v(-3.03, -2.2) * mm});
            skLineSegment(sketch, "E344", {"start": v(-3, -2.18) * mm, "end": v(-3.01, -2.19) * mm});
            skLineSegment(sketch, "E345", {"start": v(-3, -2.18) * mm, "end": v(-3, -2.18) * mm});
            skLineSegment(sketch, "E346", {"start": v(-3, -2.17) * mm, "end": v(-3, -2.18) * mm});
            skLineSegment(sketch, "E347", {"start": v(-2.58, -1.88) * mm, "end": v(-3, -2.17) * mm});
            skLineSegment(sketch, "E348", {"start": v(-2.07, -2.44) * mm, "end": v(-2.58, -1.88) * mm});
            skLineSegment(sketch, "E349", {"start": v(-2.4, -2.82) * mm, "end": v(-2.07, -2.44) * mm});
            skLineSegment(sketch, "E350", {"start": v(-2.4, -2.82) * mm, "end": v(-2.4, -2.82) * mm});
            skLineSegment(sketch, "E351", {"start": v(-2.4, -2.83) * mm, "end": v(-2.4, -2.82) * mm});
            skLineSegment(sketch, "E352", {"start": v(-2.4, -2.84) * mm, "end": v(-2.4, -2.83) * mm});
            skLineSegment(sketch, "E353", {"start": v(-2.42, -2.86) * mm, "end": v(-2.4, -2.84) * mm});
            skLineSegment(sketch, "E354", {"start": v(-2.43, -2.88) * mm, "end": v(-2.42, -2.86) * mm});
            skLineSegment(sketch, "E355", {"start": v(-2.44, -2.9) * mm, "end": v(-2.43, -2.88) * mm});
            skLineSegment(sketch, "E356", {"start": v(-2.45, -2.93) * mm, "end": v(-2.44, -2.9) * mm});
            skLineSegment(sketch, "E357", {"start": v(-2.47, -2.96) * mm, "end": v(-2.45, -2.93) * mm});
            skLineSegment(sketch, "E358", {"start": v(-2.48, -3) * mm, "end": v(-2.47, -2.96) * mm});
            skLineSegment(sketch, "E359", {"start": v(-2.5, -3.04) * mm, "end": v(-2.48, -3) * mm});
            skLineSegment(sketch, "E360", {"start": v(-2.52, -3.09) * mm, "end": v(-2.5, -3.04) * mm});
            skLineSegment(sketch, "E361", {"start": v(-2.53, -3.14) * mm, "end": v(-2.52, -3.09) * mm});
            skLineSegment(sketch, "E362", {"start": v(-2.55, -3.2) * mm, "end": v(-2.53, -3.14) * mm});
            skLineSegment(sketch, "E363", {"start": v(-2.56, -3.26) * mm, "end": v(-2.55, -3.2) * mm});
            skLineSegment(sketch, "E364", {"start": v(-2.57, -3.32) * mm, "end": v(-2.56, -3.26) * mm});
            skLineSegment(sketch, "E365", {"start": v(-2.58, -3.4) * mm, "end": v(-2.57, -3.32) * mm});
            skLineSegment(sketch, "E366", {"start": v(-2.59, -3.47) * mm, "end": v(-2.58, -3.4) * mm});
            skLineSegment(sketch, "E367", {"start": v(-2.6, -3.55) * mm, "end": v(-2.59, -3.47) * mm});
            skLineSegment(sketch, "E368", {"start": v(-2.6, -3.64) * mm, "end": v(-2.6, -3.55) * mm});
            skLineSegment(sketch, "E369", {"start": v(-2.6, -3.73) * mm, "end": v(-2.6, -3.64) * mm});
            skLineSegment(sketch, "E370", {"start": v(-2.6, -3.82) * mm, "end": v(-2.6, -3.73) * mm});
            skLineSegment(sketch, "E371", {"start": v(-2.6, -3.92) * mm, "end": v(-2.6, -3.82) * mm});
            skLineSegment(sketch, "E372", {"start": v(-2.58, -4.02) * mm, "end": v(-2.6, -3.92) * mm});
            skLineSegment(sketch, "E373", {"start": v(-2.57, -4.13) * mm, "end": v(-2.58, -4.02) * mm});
            skLineSegment(sketch, "E374", {"start": v(-2.55, -4.24) * mm, "end": v(-2.57, -4.13) * mm});
            skLineSegment(sketch, "E375", {"start": v(-2.5, -4.3) * mm, "end": v(-2.55, -4.24) * mm});
            skLineSegment(sketch, "E376", {"start": v(-2.35, -4.39) * mm, "end": v(-2.5, -4.3) * mm});
            skLineSegment(sketch, "E377", {"start": v(-2.27, -4.4) * mm, "end": v(-2.35, -4.39) * mm});
            skLineSegment(sketch, "E378", {"start": v(-2.17, -4.35) * mm, "end": v(-2.27, -4.4) * mm});
            skLineSegment(sketch, "E379", {"start": v(-2.07, -4.3) * mm, "end": v(-2.17, -4.35) * mm});
            skLineSegment(sketch, "E380", {"start": v(-1.98, -4.26) * mm, "end": v(-2.07, -4.3) * mm});
            skLineSegment(sketch, "E381", {"start": v(-1.89, -4.22) * mm, "end": v(-1.98, -4.26) * mm});
            skLineSegment(sketch, "E382", {"start": v(-1.8, -4.17) * mm, "end": v(-1.89, -4.22) * mm});
            skLineSegment(sketch, "E383", {"start": v(-1.73, -4.12) * mm, "end": v(-1.8, -4.17) * mm});
            skLineSegment(sketch, "E384", {"start": v(-1.66, -4.07) * mm, "end": v(-1.73, -4.12) * mm});
            skLineSegment(sketch, "E385", {"start": v(-1.6, -4.03) * mm, "end": v(-1.66, -4.07) * mm});
            skLineSegment(sketch, "E386", {"start": v(-1.53, -3.98) * mm, "end": v(-1.6, -4.03) * mm});
            skLineSegment(sketch, "E387", {"start": v(-1.48, -3.93) * mm, "end": v(-1.53, -3.98) * mm});
            skLineSegment(sketch, "E388", {"start": v(-1.43, -3.89) * mm, "end": v(-1.48, -3.93) * mm});
            skLineSegment(sketch, "E389", {"start": v(-1.38, -3.84) * mm, "end": v(-1.43, -3.89) * mm});
            skLineSegment(sketch, "E390", {"start": v(-1.34, -3.8) * mm, "end": v(-1.38, -3.84) * mm});
            skLineSegment(sketch, "E391", {"start": v(-1.3, -3.76) * mm, "end": v(-1.34, -3.8) * mm});
            skLineSegment(sketch, "E392", {"start": v(-1.27, -3.72) * mm, "end": v(-1.3, -3.76) * mm});
            skLineSegment(sketch, "E393", {"start": v(-1.25, -3.69) * mm, "end": v(-1.27, -3.72) * mm});
            skLineSegment(sketch, "E394", {"start": v(-1.22, -3.66) * mm, "end": v(-1.25, -3.69) * mm});
            skLineSegment(sketch, "E395", {"start": v(-1.2, -3.63) * mm, "end": v(-1.22, -3.66) * mm});
            skLineSegment(sketch, "E396", {"start": v(-1.18, -3.6) * mm, "end": v(-1.2, -3.63) * mm});
            skLineSegment(sketch, "E397", {"start": v(-1.17, -3.58) * mm, "end": v(-1.18, -3.6) * mm});
            skLineSegment(sketch, "E398", {"start": v(-1.16, -3.56) * mm, "end": v(-1.17, -3.58) * mm});
            skLineSegment(sketch, "E399", {"start": v(-1.15, -3.54) * mm, "end": v(-1.16, -3.56) * mm});
            skLineSegment(sketch, "E400", {"start": v(-1.15, -3.53) * mm, "end": v(-1.15, -3.54) * mm});
            skLineSegment(sketch, "E401", {"start": v(-1.14, -3.52) * mm, "end": v(-1.15, -3.53) * mm});
            skLineSegment(sketch, "E402", {"start": v(-1.14, -3.52) * mm, "end": v(-1.14, -3.52) * mm});
            skLineSegment(sketch, "E403", {"start": v(-0.99, -3.04) * mm, "end": v(-1.14, -3.52) * mm});
            skLineSegment(sketch, "E404", {"start": v(-0.24, -3.18) * mm, "end": v(-0.99, -3.04) * mm});
            skLineSegment(sketch, "E405", {"start": v(-0.28, -3.69) * mm, "end": v(-0.24, -3.18) * mm});
            skLineSegment(sketch, "E406", {"start": v(-0.28, -3.7) * mm, "end": v(-0.28, -3.69) * mm});
            skLineSegment(sketch, "E407", {"start": v(-0.28, -3.7) * mm, "end": v(-0.28, -3.7) * mm});
            skLineSegment(sketch, "E408", {"start": v(-0.28, -3.71) * mm, "end": v(-0.28, -3.7) * mm});
            skLineSegment(sketch, "E409", {"start": v(-0.28, -3.73) * mm, "end": v(-0.28, -3.71) * mm});
            skLineSegment(sketch, "E410", {"start": v(-0.27, -3.75) * mm, "end": v(-0.28, -3.73) * mm});
            skLineSegment(sketch, "E411", {"start": v(-0.27, -3.78) * mm, "end": v(-0.27, -3.75) * mm});
            skLineSegment(sketch, "E412", {"start": v(-0.27, -3.81) * mm, "end": v(-0.27, -3.78) * mm});
            skLineSegment(sketch, "E413", {"start": v(-0.26, -3.85) * mm, "end": v(-0.27, -3.81) * mm});
            skLineSegment(sketch, "E414", {"start": v(-0.25, -3.89) * mm, "end": v(-0.26, -3.85) * mm});
            skLineSegment(sketch, "E415", {"start": v(-0.24, -3.93) * mm, "end": v(-0.25, -3.89) * mm});
            skLineSegment(sketch, "E416", {"start": v(-0.22, -3.98) * mm, "end": v(-0.24, -3.93) * mm});
            skLineSegment(sketch, "E417", {"start": v(-0.2, -4.03) * mm, "end": v(-0.22, -3.98) * mm});
            skLineSegment(sketch, "E418", {"start": v(-0.18, -4.08) * mm, "end": v(-0.2, -4.03) * mm});
            skLineSegment(sketch, "E419", {"start": v(-0.16, -4.14) * mm, "end": v(-0.18, -4.08) * mm});
            skLineSegment(sketch, "E420", {"start": v(-0.13, -4.2) * mm, "end": v(-0.16, -4.14) * mm});
            skLineSegment(sketch, "E421", {"start": v(-0.1, -4.26) * mm, "end": v(-0.13, -4.2) * mm});
            skLineSegment(sketch, "E422", {"start": v(-0.05, -4.33) * mm, "end": v(-0.1, -4.26) * mm});
            skLineSegment(sketch, "E423", {"start": v(-0.01, -4.4) * mm, "end": v(-0.05, -4.33) * mm});
            skLineSegment(sketch, "E424", {"start": v(0.04, -4.47) * mm, "end": v(-0.01, -4.4) * mm});
            skLineSegment(sketch, "E425", {"start": v(0.09, -4.54) * mm, "end": v(0.04, -4.47) * mm});
            skLineSegment(sketch, "E426", {"start": v(0.15, -4.62) * mm, "end": v(0.09, -4.54) * mm});
            skLineSegment(sketch, "E427", {"start": v(0.2, -4.7) * mm, "end": v(0.15, -4.62) * mm});
            skLineSegment(sketch, "E428", {"start": v(0.28, -4.77) * mm, "end": v(0.2, -4.7) * mm});
            skLineSegment(sketch, "E429", {"start": v(0.35, -4.85) * mm, "end": v(0.28, -4.77) * mm});
            skLineSegment(sketch, "E430", {"start": v(0.43, -4.93) * mm, "end": v(0.35, -4.85) * mm});
            skLineSegment(sketch, "E431", {"start": v(0.51, -4.95) * mm, "end": v(0.43, -4.93) * mm});
            skLineSegment(sketch, "E432", {"start": v(0.67, -4.93) * mm, "end": v(0.51, -4.95) * mm});
            skLineSegment(sketch, "E433", {"start": v(0.75, -4.9) * mm, "end": v(0.67, -4.93) * mm});
            skLineSegment(sketch, "E434", {"start": v(0.8, -4.8) * mm, "end": v(0.75, -4.9) * mm});
            skLineSegment(sketch, "E435", {"start": v(0.86, -4.7) * mm, "end": v(0.8, -4.8) * mm});
            skLineSegment(sketch, "E436", {"start": v(0.9, -4.61) * mm, "end": v(0.86, -4.7) * mm});
            skLineSegment(sketch, "E437", {"start": v(0.95, -4.52) * mm, "end": v(0.9, -4.61) * mm});
            skLineSegment(sketch, "E438", {"start": v(1, -4.44) * mm, "end": v(0.95, -4.52) * mm});
            skLineSegment(sketch, "E439", {"start": v(1.02, -4.35) * mm, "end": v(1, -4.44) * mm});
            skLineSegment(sketch, "E440", {"start": v(1.05, -4.27) * mm, "end": v(1.02, -4.35) * mm});
            skLineSegment(sketch, "E441", {"start": v(1.08, -4.2) * mm, "end": v(1.05, -4.27) * mm});
            skLineSegment(sketch, "E442", {"start": v(1.1, -4.12) * mm, "end": v(1.08, -4.2) * mm});
            skLineSegment(sketch, "E443", {"start": v(1.12, -4.05) * mm, "end": v(1.1, -4.12) * mm});
            skLineSegment(sketch, "E444", {"start": v(1.13, -3.98) * mm, "end": v(1.12, -4.05) * mm});
            skLineSegment(sketch, "E445", {"start": v(1.14, -3.92) * mm, "end": v(1.13, -3.98) * mm});
            skLineSegment(sketch, "E446", {"start": v(1.15, -3.86) * mm, "end": v(1.14, -3.92) * mm});
            skLineSegment(sketch, "E447", {"start": v(1.16, -3.81) * mm, "end": v(1.15, -3.86) * mm});
            skLineSegment(sketch, "E448", {"start": v(1.16, -3.76) * mm, "end": v(1.16, -3.81) * mm});
            skLineSegment(sketch, "E449", {"start": v(1.16, -3.72) * mm, "end": v(1.16, -3.76) * mm});
            skLineSegment(sketch, "E450", {"start": v(1.16, -3.68) * mm, "end": v(1.16, -3.72) * mm});
            skLineSegment(sketch, "E451", {"start": v(1.16, -3.64) * mm, "end": v(1.16, -3.68) * mm});
            skLineSegment(sketch, "E452", {"start": v(1.16, -3.6) * mm, "end": v(1.16, -3.64) * mm});
            skLineSegment(sketch, "E453", {"start": v(1.15, -3.58) * mm, "end": v(1.16, -3.6) * mm});
            skLineSegment(sketch, "E454", {"start": v(1.15, -3.56) * mm, "end": v(1.15, -3.58) * mm});
            skLineSegment(sketch, "E455", {"start": v(1.15, -3.54) * mm, "end": v(1.15, -3.56) * mm});
            skLineSegment(sketch, "E456", {"start": v(1.15, -3.53) * mm, "end": v(1.15, -3.54) * mm});
            skLineSegment(sketch, "E457", {"start": v(1.14, -3.52) * mm, "end": v(1.15, -3.53) * mm});
            skLineSegment(sketch, "E458", {"start": v(1.14, -3.52) * mm, "end": v(1.14, -3.52) * mm});
            skLineSegment(sketch, "E459", {"start": v(0.99, -3.04) * mm, "end": v(1.14, -3.52) * mm});
            skLineSegment(sketch, "E460", {"start": v(1.68, -2.72) * mm, "end": v(0.99, -3.04) * mm});
            skLineSegment(sketch, "E461", {"start": v(1.94, -3.15) * mm, "end": v(1.68, -2.72) * mm});
            skLineSegment(sketch, "E462", {"start": v(1.94, -3.15) * mm, "end": v(1.94, -3.15) * mm});
            skLineSegment(sketch, "E463", {"start": v(1.95, -3.16) * mm, "end": v(1.94, -3.15) * mm});
            skLineSegment(sketch, "E464", {"start": v(1.96, -3.17) * mm, "end": v(1.95, -3.16) * mm});
            skLineSegment(sketch, "E465", {"start": v(1.97, -3.18) * mm, "end": v(1.96, -3.17) * mm});
            skLineSegment(sketch, "E466", {"start": v(1.98, -3.2) * mm, "end": v(1.97, -3.18) * mm});
            skLineSegment(sketch, "E467", {"start": v(2, -3.22) * mm, "end": v(1.98, -3.2) * mm});
            skLineSegment(sketch, "E468", {"start": v(2.03, -3.24) * mm, "end": v(2, -3.22) * mm});
            skLineSegment(sketch, "E469", {"start": v(2.05, -3.26) * mm, "end": v(2.03, -3.24) * mm});
            skLineSegment(sketch, "E470", {"start": v(2.08, -3.29) * mm, "end": v(2.05, -3.26) * mm});
            skLineSegment(sketch, "E471", {"start": v(2.12, -3.32) * mm, "end": v(2.08, -3.29) * mm});
            skLineSegment(sketch, "E472", {"start": v(2.16, -3.35) * mm, "end": v(2.12, -3.32) * mm});
            skLineSegment(sketch, "E473", {"start": v(2.2, -3.38) * mm, "end": v(2.16, -3.35) * mm});
            skLineSegment(sketch, "E474", {"start": v(2.25, -3.4) * mm, "end": v(2.2, -3.38) * mm});
            skLineSegment(sketch, "E475", {"start": v(2.3, -3.44) * mm, "end": v(2.25, -3.4) * mm});
            skLineSegment(sketch, "E476", {"start": v(2.37, -3.47) * mm, "end": v(2.3, -3.44) * mm});
            skLineSegment(sketch, "E477", {"start": v(2.43, -3.5) * mm, "end": v(2.37, -3.47) * mm});
            skLineSegment(sketch, "E478", {"start": v(2.5, -3.54) * mm, "end": v(2.43, -3.5) * mm});
            skLineSegment(sketch, "E479", {"start": v(2.58, -3.57) * mm, "end": v(2.5, -3.54) * mm});
            skLineSegment(sketch, "E480", {"start": v(2.66, -3.6) * mm, "end": v(2.58, -3.57) * mm});
            skLineSegment(sketch, "E481", {"start": v(2.74, -3.62) * mm, "end": v(2.66, -3.6) * mm});
            skLineSegment(sketch, "E482", {"start": v(2.83, -3.65) * mm, "end": v(2.74, -3.62) * mm});
            skLineSegment(sketch, "E483", {"start": v(2.93, -3.68) * mm, "end": v(2.83, -3.65) * mm});
            skLineSegment(sketch, "E484", {"start": v(3.03, -3.7) * mm, "end": v(2.93, -3.68) * mm});
            skLineSegment(sketch, "E485", {"start": v(3.14, -3.72) * mm, "end": v(3.03, -3.7) * mm});
            skLineSegment(sketch, "E486", {"start": v(3.25, -3.73) * mm, "end": v(3.14, -3.72) * mm});
            skLineSegment(sketch, "E487", {"start": v(3.33, -3.7) * mm, "end": v(3.25, -3.73) * mm});
            skLineSegment(sketch, "E488", {"start": v(3.44, -3.6) * mm, "end": v(3.33, -3.7) * mm});
            skLineSegment(sketch, "E489", {"start": v(3.48, -3.52) * mm, "end": v(3.44, -3.6) * mm});
            skLineSegment(sketch, "E490", {"start": v(3.47, -3.4) * mm, "end": v(3.48, -3.52) * mm});
            skLineSegment(sketch, "E491", {"start": v(3.46, -3.3) * mm, "end": v(3.47, -3.4) * mm});
            skLineSegment(sketch, "E492", {"start": v(3.45, -3.2) * mm, "end": v(3.46, -3.3) * mm});
            skLineSegment(sketch, "E493", {"start": v(3.43, -3.1) * mm, "end": v(3.45, -3.2) * mm});
            skLineSegment(sketch, "E494", {"start": v(3.4, -3) * mm, "end": v(3.43, -3.1) * mm});
            skLineSegment(sketch, "E495", {"start": v(3.39, -2.92) * mm, "end": v(3.4, -3) * mm});
            skLineSegment(sketch, "E496", {"start": v(3.36, -2.84) * mm, "end": v(3.39, -2.92) * mm});
            skLineSegment(sketch, "E497", {"start": v(3.34, -2.76) * mm, "end": v(3.36, -2.84) * mm});
            skLineSegment(sketch, "E498", {"start": v(3.31, -2.69) * mm, "end": v(3.34, -2.76) * mm});
            skLineSegment(sketch, "E499", {"start": v(3.28, -2.62) * mm, "end": v(3.31, -2.69) * mm});
            skLineSegment(sketch, "E500", {"start": v(3.26, -2.56) * mm, "end": v(3.28, -2.62) * mm});
            skLineSegment(sketch, "E501", {"start": v(3.23, -2.5) * mm, "end": v(3.26, -2.56) * mm});
            skLineSegment(sketch, "E502", {"start": v(3.2, -2.45) * mm, "end": v(3.23, -2.5) * mm});
            skLineSegment(sketch, "E503", {"start": v(3.18, -2.4) * mm, "end": v(3.2, -2.45) * mm});
            skLineSegment(sketch, "E504", {"start": v(3.15, -2.36) * mm, "end": v(3.18, -2.4) * mm});
            skLineSegment(sketch, "E505", {"start": v(3.12, -2.32) * mm, "end": v(3.15, -2.36) * mm});
            skLineSegment(sketch, "E506", {"start": v(3.1, -2.3) * mm, "end": v(3.12, -2.32) * mm});
            skLineSegment(sketch, "E507", {"start": v(3.08, -2.26) * mm, "end": v(3.1, -2.3) * mm});
            skLineSegment(sketch, "E508", {"start": v(3.06, -2.24) * mm, "end": v(3.08, -2.26) * mm});
            skLineSegment(sketch, "E509", {"start": v(3.04, -2.22) * mm, "end": v(3.06, -2.24) * mm});
            skLineSegment(sketch, "E510", {"start": v(3.02, -2.2) * mm, "end": v(3.04, -2.22) * mm});
            skLineSegment(sketch, "E511", {"start": v(3.01, -2.2) * mm, "end": v(3.02, -2.2) * mm});
            skLineSegment(sketch, "E512", {"start": v(3, -2.18) * mm, "end": v(3.01, -2.2) * mm});
            skLineSegment(sketch, "E513", {"start": v(3, -2.18) * mm, "end": v(3, -2.18) * mm});
            skLineSegment(sketch, "E514", {"start": v(3, -2.17) * mm, "end": v(3, -2.18) * mm});
            skLineSegment(sketch, "E515", {"start": v(2.58, -1.88) * mm, "end": v(3, -2.17) * mm});
            skLineSegment(sketch, "E516", {"start": v(2.95, -1.21) * mm, "end": v(2.58, -1.88) * mm});
            skLineSegment(sketch, "E517", {"start": v(3.42, -1.4) * mm, "end": v(2.95, -1.21) * mm});
            skLineSegment(sketch, "E518", {"start": v(3.42, -1.4) * mm, "end": v(3.42, -1.4) * mm});
            skLineSegment(sketch, "E519", {"start": v(3.43, -1.4) * mm, "end": v(3.42, -1.4) * mm});
            skLineSegment(sketch, "E520", {"start": v(3.45, -1.41) * mm, "end": v(3.43, -1.4) * mm});
            skLineSegment(sketch, "E521", {"start": v(3.46, -1.42) * mm, "end": v(3.45, -1.41) * mm});
            skLineSegment(sketch, "E522", {"start": v(3.48, -1.42) * mm, "end": v(3.46, -1.42) * mm});
            skLineSegment(sketch, "E523", {"start": v(3.51, -1.43) * mm, "end": v(3.48, -1.42) * mm});
            skLineSegment(sketch, "E524", {"start": v(3.54, -1.43) * mm, "end": v(3.51, -1.43) * mm});
            skLineSegment(sketch, "E525", {"start": v(3.58, -1.43) * mm, "end": v(3.54, -1.43) * mm});
            skLineSegment(sketch, "E526", {"start": v(3.62, -1.44) * mm, "end": v(3.58, -1.43) * mm});
            skLineSegment(sketch, "E527", {"start": v(3.66, -1.44) * mm, "end": v(3.62, -1.44) * mm});
            skLineSegment(sketch, "E528", {"start": v(3.71, -1.44) * mm, "end": v(3.66, -1.44) * mm});
            skLineSegment(sketch, "E529", {"start": v(3.77, -1.44) * mm, "end": v(3.71, -1.44) * mm});
            skLineSegment(sketch, "E530", {"start": v(3.83, -1.43) * mm, "end": v(3.77, -1.44) * mm});
            skLineSegment(sketch, "E531", {"start": v(3.89, -1.43) * mm, "end": v(3.83, -1.43) * mm});
            skLineSegment(sketch, "E532", {"start": v(3.96, -1.42) * mm, "end": v(3.89, -1.43) * mm});
            skLineSegment(sketch, "E533", {"start": v(4.03, -1.4) * mm, "end": v(3.96, -1.42) * mm});
            skLineSegment(sketch, "E534", {"start": v(4.1, -1.4) * mm, "end": v(4.03, -1.4) * mm});
            skLineSegment(sketch, "E535", {"start": v(4.18, -1.37) * mm, "end": v(4.1, -1.4) * mm});
            skLineSegment(sketch, "E536", {"start": v(4.26, -1.35) * mm, "end": v(4.18, -1.37) * mm});
            skLineSegment(sketch, "E537", {"start": v(4.35, -1.32) * mm, "end": v(4.26, -1.35) * mm});
            skLineSegment(sketch, "E538", {"start": v(4.44, -1.29) * mm, "end": v(4.35, -1.32) * mm});
            skLineSegment(sketch, "E539", {"start": v(4.53, -1.25) * mm, "end": v(4.44, -1.29) * mm});
            skLineSegment(sketch, "E540", {"start": v(4.62, -1.21) * mm, "end": v(4.53, -1.25) * mm});
            skLineSegment(sketch, "E541", {"start": v(4.72, -1.16) * mm, "end": v(4.62, -1.21) * mm});
            skLineSegment(sketch, "E542", {"start": v(4.82, -1.11) * mm, "end": v(4.72, -1.16) * mm});
            skLineSegment(sketch, "E543", {"start": v(4.87, -1.04) * mm, "end": v(4.82, -1.11) * mm});
            skLineSegment(sketch, "E544", {"start": v(4.9, -0.88) * mm, "end": v(4.87, -1.04) * mm});
            skLineSegment(sketch, "E545", {"start": v(4.88, -0.8) * mm, "end": v(4.9, -0.88) * mm});
            skLineSegment(sketch, "E546", {"start": v(4.8, -0.72) * mm, "end": v(4.88, -0.8) * mm});
            skLineSegment(sketch, "E547", {"start": v(4.74, -0.64) * mm, "end": v(4.8, -0.72) * mm});
            skLineSegment(sketch, "E548", {"start": v(4.67, -0.56) * mm, "end": v(4.74, -0.64) * mm});
            skLineSegment(sketch, "E549", {"start": v(4.6, -0.5) * mm, "end": v(4.67, -0.56) * mm});
            skLineSegment(sketch, "E550", {"start": v(4.52, -0.43) * mm, "end": v(4.6, -0.5) * mm});
            skLineSegment(sketch, "E551", {"start": v(4.46, -0.37) * mm, "end": v(4.52, -0.43) * mm});
            skLineSegment(sketch, "E552", {"start": v(4.39, -0.32) * mm, "end": v(4.46, -0.37) * mm});
            skLineSegment(sketch, "E553", {"start": v(4.32, -0.27) * mm, "end": v(4.39, -0.32) * mm});
            skLineSegment(sketch, "E554", {"start": v(4.26, -0.23) * mm, "end": v(4.32, -0.27) * mm});
            skLineSegment(sketch, "E555", {"start": v(4.2, -0.19) * mm, "end": v(4.26, -0.23) * mm});
            skLineSegment(sketch, "E556", {"start": v(4.14, -0.16) * mm, "end": v(4.2, -0.19) * mm});
            skLineSegment(sketch, "E557", {"start": v(4.08, -0.13) * mm, "end": v(4.14, -0.16) * mm});
            skLineSegment(sketch, "E558", {"start": v(4.03, -0.1) * mm, "end": v(4.08, -0.13) * mm});
            skLineSegment(sketch, "E559", {"start": v(3.98, -0.08) * mm, "end": v(4.03, -0.1) * mm});
            skLineSegment(sketch, "E560", {"start": v(3.94, -0.06) * mm, "end": v(3.98, -0.08) * mm});
            skLineSegment(sketch, "E561", {"start": v(3.9, -0.04) * mm, "end": v(3.94, -0.06) * mm});
            skLineSegment(sketch, "E562", {"start": v(3.85, -0.03) * mm, "end": v(3.9, -0.04) * mm});
            skLineSegment(sketch, "E563", {"start": v(3.82, -0.02) * mm, "end": v(3.85, -0.03) * mm});
            skLineSegment(sketch, "E564", {"start": v(3.79, -0.01) * mm, "end": v(3.82, -0.02) * mm});
            skLineSegment(sketch, "E565", {"start": v(3.76, 0) * mm, "end": v(3.79, -0.01) * mm});
            skLineSegment(sketch, "E566", {"start": v(3.74, 0) * mm, "end": v(3.76, 0) * mm});
            skLineSegment(sketch, "E567", {"start": v(3.72, 0) * mm, "end": v(3.74, 0) * mm});
            skLineSegment(sketch, "E568", {"start": v(3.7, 0) * mm, "end": v(3.72, 0) * mm});
            skLineSegment(sketch, "E569", {"start": v(3.7, 0) * mm, "end": v(3.7, 0) * mm});
            skLineSegment(sketch, "E570", {"start": v(3.2, 0) * mm, "end": v(3.7, 0) * mm});
            skLineSegment(sketch, "E571", {"start": v(3.1, 0.76) * mm, "end": v(3.2, 0) * mm});
            skSolve(sketch);
        }
        {
            var Q0;
            {var subQ0=sQuery(id+"F10.wireOp",EDGE,"E273");Q0=makeQuery(id+"F10.imprint","IMPRINT",FACE,{"disambiguationData":[TD([[makeQuery(id+"F10.imprint","IMPRINT",EDGE,{"derivedFrom":subQ0}),1.0]])]});}
            var Q1;
            {var subQ0=sQuery(id+"F10.wireOp",EDGE,"E328");Q1=makeQuery(id+"F10.imprint","IMPRINT",FACE,{"disambiguationData":[TD([[makeQuery(id+"F10.imprint","IMPRINT",EDGE,{"derivedFrom":subQ0}),1.0]])]});}
            var Q2;
            {var subQ5=sQuery(id+"F10.wireOp",EDGE,"E384");Q2=makeQuery(id+"F10.imprint","IMPRINT",FACE,{"disambiguationData":[TD([[makeQuery(id+"F10.imprint","IMPRINT",EDGE,{"derivedFrom":subQ5}),1.0]])]});}
            var Q3;
            {var subQ0=sQuery(id+"F10.wireOp",EDGE,"E440");Q3=makeQuery(id+"F10.imprint","IMPRINT",FACE,{"disambiguationData":[TD([[makeQuery(id+"F10.imprint","IMPRINT",EDGE,{"derivedFrom":subQ0}),1.0]])]});}
            var Q4;
            {var subQ0=sQuery(id+"F10.wireOp",EDGE,"E496");Q4=makeQuery(id+"F10.imprint","IMPRINT",FACE,{"disambiguationData":[TD([[makeQuery(id+"F10.imprint","IMPRINT",EDGE,{"derivedFrom":subQ0}),1.0]])]});}
            var Q5;
            {var subQ0=sQuery(id+"F10.wireOp",EDGE,"E49");Q5=makeQuery(id+"F10.imprint","IMPRINT",FACE,{"disambiguationData":[TD([[makeQuery(id+"F10.imprint","IMPRINT",EDGE,{"derivedFrom":subQ0}),1.0]])]});}
            var Q6;
            Q6=makeQuery(id+"F10.imprint","IMPRINT",FACE,{"disambiguationData":[TD([[makeQuery(id+"F10.imprint","IMPRINT",EDGE,{"derivedFrom":sQuery(id+"F10.wireOp",EDGE,"E14")}),1.0]])]});
            var Q7;
            {var subQ0=sQuery(id+"F10.wireOp",EDGE,"E161");Q7=makeQuery(id+"F10.imprint","IMPRINT",FACE,{"disambiguationData":[TD([[makeQuery(id+"F10.imprint","IMPRINT",EDGE,{"derivedFrom":subQ0}),1.0]])]});}
            var Q8;
            {var subQ5=sQuery(id+"F10.wireOp",EDGE,"E105");Q8=makeQuery(id+"F10.imprint","IMPRINT",FACE,{"disambiguationData":[TD([[makeQuery(id+"F10.imprint","IMPRINT",EDGE,{"derivedFrom":subQ5}),1.0]])]});}
            var Q9;
            {var subQ0=sQuery(id+"F10.wireOp",EDGE,"E217");Q9=makeQuery(id+"F10.imprint","IMPRINT",FACE,{"disambiguationData":[TD([[makeQuery(id+"F10.imprint","IMPRINT",EDGE,{"derivedFrom":subQ0}),1.0]])]});}
            extrude(context, id + "F11", {"entities" : qUnion([Q0, Q1, Q2, Q3, Q4, Q5, Q6, Q7, Q8, Q9]), "operationType" : NewBodyOperationType.REMOVE, "oppositeDirection" : true, "depth" : 4 * mm, "offsetDistance" : 25 * mm});
        }
        {
            var Q0;
            {var subQ0=sQuery(id+"F10.wireOp",EDGE,"E259");Q0=makeQuery(id+"F10.imprint","IMPRINT",FACE,{"disambiguationData":[TD([[makeQuery(id+"F10.imprint","IMPRINT",EDGE,{"derivedFrom":subQ0}),-1.0]])]});}
            var Q1;
            {var subQ5=sQuery(id+"F10.wireOp",EDGE,"E203");Q1=makeQuery(id+"F10.imprint","IMPRINT",FACE,{"disambiguationData":[TD([[makeQuery(id+"F10.imprint","IMPRINT",EDGE,{"derivedFrom":subQ5}),-1.0]])]});}
            var Q2;
            {var subQ0=sQuery(id+"F10.wireOp",EDGE,"E147");Q2=makeQuery(id+"F10.imprint","IMPRINT",FACE,{"disambiguationData":[TD([[makeQuery(id+"F10.imprint","IMPRINT",EDGE,{"derivedFrom":subQ0}),-1.0]])]});}
            var Q3;
            {var subQ5=sQuery(id+"F10.wireOp",EDGE,"E91");Q3=makeQuery(id+"F10.imprint","IMPRINT",FACE,{"disambiguationData":[TD([[makeQuery(id+"F10.imprint","IMPRINT",EDGE,{"derivedFrom":subQ5}),-1.0]])]});}
            var Q4;
            {var subQ0=sQuery(id+"F10.wireOp",EDGE,"E35");Q4=makeQuery(id+"F10.imprint","IMPRINT",FACE,{"disambiguationData":[TD([[makeQuery(id+"F10.imprint","IMPRINT",EDGE,{"derivedFrom":subQ0}),-1.0]])]});}
            var Q5;
            {var subQ0=sQuery(id+"F10.wireOp",EDGE,"E538");Q5=makeQuery(id+"F10.imprint","IMPRINT",FACE,{"disambiguationData":[TD([[makeQuery(id+"F10.imprint","IMPRINT",EDGE,{"derivedFrom":subQ0}),-1.0]])]});}
            var Q6;
            {var subQ0=sQuery(id+"F10.wireOp",EDGE,"E482");Q6=makeQuery(id+"F10.imprint","IMPRINT",FACE,{"disambiguationData":[TD([[makeQuery(id+"F10.imprint","IMPRINT",EDGE,{"derivedFrom":subQ0}),-1.0]])]});}
            var Q7;
            {var subQ0=sQuery(id+"F10.wireOp",EDGE,"E426");Q7=makeQuery(id+"F10.imprint","IMPRINT",FACE,{"disambiguationData":[TD([[makeQuery(id+"F10.imprint","IMPRINT",EDGE,{"derivedFrom":subQ0}),-1.0]])]});}
            var Q8;
            {var subQ5=sQuery(id+"F10.wireOp",EDGE,"E314");Q8=makeQuery(id+"F10.imprint","IMPRINT",FACE,{"disambiguationData":[TD([[makeQuery(id+"F10.imprint","IMPRINT",EDGE,{"derivedFrom":subQ5}),-1.0]])]});}
            var Q9;
            {var subQ0=sQuery(id+"F10.wireOp",EDGE,"E370");Q9=makeQuery(id+"F10.imprint","IMPRINT",FACE,{"disambiguationData":[TD([[makeQuery(id+"F10.imprint","IMPRINT",EDGE,{"derivedFrom":subQ0}),-1.0]])]});}
            extrude(context, id + "F12", {"entities" : qUnion([Q0, Q1, Q2, Q3, Q4, Q5, Q6, Q7, Q8, Q9]), "operationType" : NewBodyOperationType.ADD, "oppositeDirection" : true, "depth" : 4 * mm, "offsetDistance" : 25 * mm});
        }
        {
            var Q0;
            {var subQ0=sQuery(id+"F0.wireOp",EDGE,"E1");Q0=makeQuery(id+"F7.boolean.opBoolean","MERGE",FACE,{"derivedFrom":[makeQuery(id+"F1.opExtrude","CAP_FACE",FACE,{"disambiguationData":[OSD([sQuery(id+"F0.wireOp",EDGE,"E0"),subQ0])],"isStart":false}),makeQuery(id+"F7.opExtrude","CAP_FACE",FACE,{"disambiguationData":[OSD([subQ0,sQuery(id+"F6.wireOp",EDGE,"E10"),sQuery(id+"F6.wireOp",EDGE,"E12.1.1")])],"isStart":true}),makeQuery(id+"F7.opExtrude","CAP_FACE",FACE,{"disambiguationData":[OSD([subQ0,sQuery(id+"F6.wireOp",EDGE,"E11"),sQuery(id+"F6.wireOp",EDGE,"E12.9.0")])],"isStart":true}),makeQuery(id+"F7.opExtrude","CAP_FACE",FACE,{"disambiguationData":[OSD([subQ0,sQuery(id+"F6.wireOp",EDGE,"E12.1.0"),sQuery(id+"F6.wireOp",EDGE,"E12.2.1")])],"isStart":true}),makeQuery(id+"F7.opExtrude","CAP_FACE",FACE,{"disambiguationData":[OSD([subQ0,sQuery(id+"F6.wireOp",EDGE,"E12.2.0"),sQuery(id+"F6.wireOp",EDGE,"E12.3.1")])],"isStart":true}),makeQuery(id+"F7.opExtrude","CAP_FACE",FACE,{"disambiguationData":[OSD([subQ0,sQuery(id+"F6.wireOp",EDGE,"E12.3.0"),sQuery(id+"F6.wireOp",EDGE,"E12.4.1")])],"isStart":true}),makeQuery(id+"F7.opExtrude","CAP_FACE",FACE,{"disambiguationData":[OSD([subQ0,sQuery(id+"F6.wireOp",EDGE,"E12.4.0"),sQuery(id+"F6.wireOp",EDGE,"E12.5.1")])],"isStart":true}),makeQuery(id+"F7.opExtrude","CAP_FACE",FACE,{"disambiguationData":[OSD([subQ0,sQuery(id+"F6.wireOp",EDGE,"E12.5.0"),sQuery(id+"F6.wireOp",EDGE,"E12.6.1")])],"isStart":true}),makeQuery(id+"F7.opExtrude","CAP_FACE",FACE,{"disambiguationData":[OSD([subQ0,sQuery(id+"F6.wireOp",EDGE,"E12.6.0"),sQuery(id+"F6.wireOp",EDGE,"E12.7.1")])],"isStart":true}),makeQuery(id+"F7.opExtrude","CAP_FACE",FACE,{"disambiguationData":[OSD([subQ0,sQuery(id+"F6.wireOp",EDGE,"E12.7.0"),sQuery(id+"F6.wireOp",EDGE,"E12.8.1")])],"isStart":true}),makeQuery(id+"F7.opExtrude","CAP_FACE",FACE,{"disambiguationData":[OSD([subQ0,sQuery(id+"F6.wireOp",EDGE,"E12.8.0"),sQuery(id+"F6.wireOp",EDGE,"E12.9.1")])],"isStart":true})]});}
            var sketch = newSketch(context, id + "F13", { "sketchPlane" : qUnion([Q0])});
            skCircle(sketch, "E572", {"center": v(0, 0) * mm, "radius": 3.2 * mm});
            skSolve(sketch);
        }
        {
            var Q0;
            Q0=makeQuery(id+"F13.imprint","IMPRINT",FACE,{"disambiguationData":[TD([[makeQuery(id+"F13.imprint","IMPRINT",EDGE,{"derivedFrom":sQuery(id+"F13.wireOp",EDGE,"E572")}),-1.0]])]});
            extrude(context, id + "F14", {"entities" : qUnion([Q0]), "operationType" : NewBodyOperationType.REMOVE, "oppositeDirection" : true, "depth" : 2 * mm, "offsetDistance" : 25 * mm});
        }
        {
            var Q0;
            {var subQ0=sQuery(id+"F0.wireOp",EDGE,"E1");Q0=makeQuery(id+"F7.boolean.opBoolean","MERGE",FACE,{"derivedFrom":[makeQuery(id+"F1.opExtrude","CAP_FACE",FACE,{"disambiguationData":[OSD([sQuery(id+"F0.wireOp",EDGE,"E0"),subQ0])],"isStart":false}),makeQuery(id+"F7.opExtrude","CAP_FACE",FACE,{"disambiguationData":[OSD([subQ0,sQuery(id+"F6.wireOp",EDGE,"E10"),sQuery(id+"F6.wireOp",EDGE,"E12.1.1")])],"isStart":true}),makeQuery(id+"F7.opExtrude","CAP_FACE",FACE,{"disambiguationData":[OSD([subQ0,sQuery(id+"F6.wireOp",EDGE,"E11"),sQuery(id+"F6.wireOp",EDGE,"E12.9.0")])],"isStart":true}),makeQuery(id+"F7.opExtrude","CAP_FACE",FACE,{"disambiguationData":[OSD([subQ0,sQuery(id+"F6.wireOp",EDGE,"E12.1.0"),sQuery(id+"F6.wireOp",EDGE,"E12.2.1")])],"isStart":true}),makeQuery(id+"F7.opExtrude","CAP_FACE",FACE,{"disambiguationData":[OSD([subQ0,sQuery(id+"F6.wireOp",EDGE,"E12.2.0"),sQuery(id+"F6.wireOp",EDGE,"E12.3.1")])],"isStart":true}),makeQuery(id+"F7.opExtrude","CAP_FACE",FACE,{"disambiguationData":[OSD([subQ0,sQuery(id+"F6.wireOp",EDGE,"E12.3.0"),sQuery(id+"F6.wireOp",EDGE,"E12.4.1")])],"isStart":true}),makeQuery(id+"F7.opExtrude","CAP_FACE",FACE,{"disambiguationData":[OSD([subQ0,sQuery(id+"F6.wireOp",EDGE,"E12.4.0"),sQuery(id+"F6.wireOp",EDGE,"E12.5.1")])],"isStart":true}),makeQuery(id+"F7.opExtrude","CAP_FACE",FACE,{"disambiguationData":[OSD([subQ0,sQuery(id+"F6.wireOp",EDGE,"E12.5.0"),sQuery(id+"F6.wireOp",EDGE,"E12.6.1")])],"isStart":true}),makeQuery(id+"F7.opExtrude","CAP_FACE",FACE,{"disambiguationData":[OSD([subQ0,sQuery(id+"F6.wireOp",EDGE,"E12.6.0"),sQuery(id+"F6.wireOp",EDGE,"E12.7.1")])],"isStart":true}),makeQuery(id+"F7.opExtrude","CAP_FACE",FACE,{"disambiguationData":[OSD([subQ0,sQuery(id+"F6.wireOp",EDGE,"E12.7.0"),sQuery(id+"F6.wireOp",EDGE,"E12.8.1")])],"isStart":true}),makeQuery(id+"F7.opExtrude","CAP_FACE",FACE,{"disambiguationData":[OSD([subQ0,sQuery(id+"F6.wireOp",EDGE,"E12.8.0"),sQuery(id+"F6.wireOp",EDGE,"E12.9.1")])],"isStart":true})]});}
            var sketch = newSketch(context, id + "F15", { "sketchPlane" : qUnion([Q0])});
            skLineSegment(sketch, "E573", {"start": v(3.6, 0.87) * mm, "end": v(3.1, 0.76) * mm});
            skLineSegment(sketch, "E574", {"start": v(3.6, 0.88) * mm, "end": v(3.6, 0.87) * mm});
            skLineSegment(sketch, "E575", {"start": v(3.6, 0.88) * mm, "end": v(3.6, 0.88) * mm});
            skLineSegment(sketch, "E576", {"start": v(3.62, 0.88) * mm, "end": v(3.6, 0.88) * mm});
            skLineSegment(sketch, "E577", {"start": v(3.63, 0.9) * mm, "end": v(3.62, 0.88) * mm});
            skLineSegment(sketch, "E578", {"start": v(3.65, 0.9) * mm, "end": v(3.63, 0.9) * mm});
            skLineSegment(sketch, "E579", {"start": v(3.68, 0.91) * mm, "end": v(3.65, 0.9) * mm});
            skLineSegment(sketch, "E580", {"start": v(3.7, 0.93) * mm, "end": v(3.68, 0.91) * mm});
            skLineSegment(sketch, "E581", {"start": v(3.74, 0.94) * mm, "end": v(3.7, 0.93) * mm});
            skLineSegment(sketch, "E582", {"start": v(3.77, 0.96) * mm, "end": v(3.74, 0.94) * mm});
            skLineSegment(sketch, "E583", {"start": v(3.8, 0.99) * mm, "end": v(3.77, 0.96) * mm});
            skLineSegment(sketch, "E584", {"start": v(3.85, 1.02) * mm, "end": v(3.8, 0.99) * mm});
            skLineSegment(sketch, "E585", {"start": v(3.9, 1.05) * mm, "end": v(3.85, 1.02) * mm});
            skLineSegment(sketch, "E586", {"start": v(3.94, 1.09) * mm, "end": v(3.9, 1.05) * mm});
            skLineSegment(sketch, "E587", {"start": v(3.98, 1.13) * mm, "end": v(3.94, 1.09) * mm});
            skLineSegment(sketch, "E588", {"start": v(4.03, 1.18) * mm, "end": v(3.98, 1.13) * mm});
            skLineSegment(sketch, "E589", {"start": v(4.08, 1.23) * mm, "end": v(4.03, 1.18) * mm});
            skLineSegment(sketch, "E590", {"start": v(4.14, 1.29) * mm, "end": v(4.08, 1.23) * mm});
            skLineSegment(sketch, "E591", {"start": v(4.19, 1.35) * mm, "end": v(4.14, 1.29) * mm});
            skLineSegment(sketch, "E592", {"start": v(4.24, 1.41) * mm, "end": v(4.19, 1.35) * mm});
            skLineSegment(sketch, "E593", {"start": v(4.3, 1.49) * mm, "end": v(4.24, 1.41) * mm});
            skLineSegment(sketch, "E594", {"start": v(4.35, 1.57) * mm, "end": v(4.3, 1.49) * mm});
            skLineSegment(sketch, "E595", {"start": v(4.4, 1.65) * mm, "end": v(4.35, 1.57) * mm});
            skLineSegment(sketch, "E596", {"start": v(4.45, 1.74) * mm, "end": v(4.4, 1.65) * mm});
            skLineSegment(sketch, "E597", {"start": v(4.5, 1.83) * mm, "end": v(4.45, 1.74) * mm});
            skLineSegment(sketch, "E598", {"start": v(4.55, 1.93) * mm, "end": v(4.5, 1.83) * mm});
            skLineSegment(sketch, "E599", {"start": v(4.55, 2.02) * mm, "end": v(4.55, 1.93) * mm});
            skLineSegment(sketch, "E600", {"start": v(4.48, 2.16) * mm, "end": v(4.55, 2.02) * mm});
            skLineSegment(sketch, "E601", {"start": v(4.42, 2.22) * mm, "end": v(4.48, 2.16) * mm});
            skLineSegment(sketch, "E602", {"start": v(4.31, 2.25) * mm, "end": v(4.42, 2.22) * mm});
            skLineSegment(sketch, "E603", {"start": v(4.2, 2.27) * mm, "end": v(4.31, 2.25) * mm});
            skLineSegment(sketch, "E604", {"start": v(4.1, 2.29) * mm, "end": v(4.2, 2.27) * mm});
            skLineSegment(sketch, "E605", {"start": v(4, 2.3) * mm, "end": v(4.1, 2.29) * mm});
            skLineSegment(sketch, "E606", {"start": v(3.91, 2.31) * mm, "end": v(4, 2.3) * mm});
            skLineSegment(sketch, "E607", {"start": v(3.82, 2.32) * mm, "end": v(3.91, 2.31) * mm});
            skLineSegment(sketch, "E608", {"start": v(3.74, 2.32) * mm, "end": v(3.82, 2.32) * mm});
            skLineSegment(sketch, "E609", {"start": v(3.66, 2.32) * mm, "end": v(3.74, 2.32) * mm});
            skLineSegment(sketch, "E610", {"start": v(3.58, 2.32) * mm, "end": v(3.66, 2.32) * mm});
            skLineSegment(sketch, "E611", {"start": v(3.5, 2.31) * mm, "end": v(3.58, 2.32) * mm});
            skLineSegment(sketch, "E612", {"start": v(3.44, 2.3) * mm, "end": v(3.5, 2.31) * mm});
            skLineSegment(sketch, "E613", {"start": v(3.38, 2.3) * mm, "end": v(3.44, 2.3) * mm});
            skLineSegment(sketch, "E614", {"start": v(3.32, 2.29) * mm, "end": v(3.38, 2.3) * mm});
            skLineSegment(sketch, "E615", {"start": v(3.27, 2.28) * mm, "end": v(3.32, 2.29) * mm});
            skLineSegment(sketch, "E616", {"start": v(3.22, 2.26) * mm, "end": v(3.27, 2.28) * mm});
            skLineSegment(sketch, "E617", {"start": v(3.18, 2.25) * mm, "end": v(3.22, 2.26) * mm});
            skLineSegment(sketch, "E618", {"start": v(3.14, 2.24) * mm, "end": v(3.18, 2.25) * mm});
            skLineSegment(sketch, "E619", {"start": v(3.1, 2.23) * mm, "end": v(3.14, 2.24) * mm});
            skLineSegment(sketch, "E620", {"start": v(3.07, 2.22) * mm, "end": v(3.1, 2.23) * mm});
            skLineSegment(sketch, "E621", {"start": v(3.05, 2.2) * mm, "end": v(3.07, 2.22) * mm});
            skLineSegment(sketch, "E622", {"start": v(3.03, 2.2) * mm, "end": v(3.05, 2.2) * mm});
            skLineSegment(sketch, "E623", {"start": v(3.01, 2.19) * mm, "end": v(3.03, 2.2) * mm});
            skLineSegment(sketch, "E624", {"start": v(3, 2.18) * mm, "end": v(3.01, 2.19) * mm});
            skLineSegment(sketch, "E625", {"start": v(3, 2.18) * mm, "end": v(3, 2.18) * mm});
            skLineSegment(sketch, "E626", {"start": v(3, 2.17) * mm, "end": v(3, 2.18) * mm});
            skLineSegment(sketch, "E627", {"start": v(2.58, 1.88) * mm, "end": v(3, 2.17) * mm});
            skLineSegment(sketch, "E628", {"start": v(2.07, 2.44) * mm, "end": v(2.58, 1.88) * mm});
            skLineSegment(sketch, "E629", {"start": v(2.4, 2.82) * mm, "end": v(2.07, 2.44) * mm});
            skLineSegment(sketch, "E630", {"start": v(2.4, 2.82) * mm, "end": v(2.4, 2.82) * mm});
            skLineSegment(sketch, "E631", {"start": v(2.4, 2.83) * mm, "end": v(2.4, 2.82) * mm});
            skLineSegment(sketch, "E632", {"start": v(2.4, 2.84) * mm, "end": v(2.4, 2.83) * mm});
            skLineSegment(sketch, "E633", {"start": v(2.42, 2.86) * mm, "end": v(2.4, 2.84) * mm});
            skLineSegment(sketch, "E634", {"start": v(2.43, 2.88) * mm, "end": v(2.42, 2.86) * mm});
            skLineSegment(sketch, "E635", {"start": v(2.44, 2.9) * mm, "end": v(2.43, 2.88) * mm});
            skLineSegment(sketch, "E636", {"start": v(2.45, 2.93) * mm, "end": v(2.44, 2.9) * mm});
            skLineSegment(sketch, "E637", {"start": v(2.47, 2.96) * mm, "end": v(2.45, 2.93) * mm});
            skLineSegment(sketch, "E638", {"start": v(2.48, 3) * mm, "end": v(2.47, 2.96) * mm});
            skLineSegment(sketch, "E639", {"start": v(2.5, 3.04) * mm, "end": v(2.48, 3) * mm});
            skLineSegment(sketch, "E640", {"start": v(2.52, 3.09) * mm, "end": v(2.5, 3.04) * mm});
            skLineSegment(sketch, "E641", {"start": v(2.53, 3.14) * mm, "end": v(2.52, 3.09) * mm});
            skLineSegment(sketch, "E642", {"start": v(2.55, 3.2) * mm, "end": v(2.53, 3.14) * mm});
            skLineSegment(sketch, "E643", {"start": v(2.56, 3.26) * mm, "end": v(2.55, 3.2) * mm});
            skLineSegment(sketch, "E644", {"start": v(2.57, 3.32) * mm, "end": v(2.56, 3.26) * mm});
            skLineSegment(sketch, "E645", {"start": v(2.58, 3.4) * mm, "end": v(2.57, 3.32) * mm});
            skLineSegment(sketch, "E646", {"start": v(2.59, 3.47) * mm, "end": v(2.58, 3.4) * mm});
            skLineSegment(sketch, "E647", {"start": v(2.6, 3.55) * mm, "end": v(2.59, 3.47) * mm});
            skLineSegment(sketch, "E648", {"start": v(2.6, 3.64) * mm, "end": v(2.6, 3.55) * mm});
            skLineSegment(sketch, "E649", {"start": v(2.6, 3.73) * mm, "end": v(2.6, 3.64) * mm});
            skLineSegment(sketch, "E650", {"start": v(2.6, 3.82) * mm, "end": v(2.6, 3.73) * mm});
            skLineSegment(sketch, "E651", {"start": v(2.6, 3.92) * mm, "end": v(2.6, 3.82) * mm});
            skLineSegment(sketch, "E652", {"start": v(2.58, 4.02) * mm, "end": v(2.6, 3.92) * mm});
            skLineSegment(sketch, "E653", {"start": v(2.57, 4.13) * mm, "end": v(2.58, 4.02) * mm});
            skLineSegment(sketch, "E654", {"start": v(2.55, 4.24) * mm, "end": v(2.57, 4.13) * mm});
            skLineSegment(sketch, "E655", {"start": v(2.5, 4.3) * mm, "end": v(2.55, 4.24) * mm});
            skLineSegment(sketch, "E656", {"start": v(2.35, 4.39) * mm, "end": v(2.5, 4.3) * mm});
            skLineSegment(sketch, "E657", {"start": v(2.27, 4.4) * mm, "end": v(2.35, 4.39) * mm});
            skLineSegment(sketch, "E658", {"start": v(2.17, 4.35) * mm, "end": v(2.27, 4.4) * mm});
            skLineSegment(sketch, "E659", {"start": v(2.07, 4.3) * mm, "end": v(2.17, 4.35) * mm});
            skLineSegment(sketch, "E660", {"start": v(1.98, 4.26) * mm, "end": v(2.07, 4.3) * mm});
            skLineSegment(sketch, "E661", {"start": v(1.89, 4.22) * mm, "end": v(1.98, 4.26) * mm});
            skLineSegment(sketch, "E662", {"start": v(1.8, 4.17) * mm, "end": v(1.89, 4.22) * mm});
            skLineSegment(sketch, "E663", {"start": v(1.73, 4.12) * mm, "end": v(1.8, 4.17) * mm});
            skLineSegment(sketch, "E664", {"start": v(1.66, 4.07) * mm, "end": v(1.73, 4.12) * mm});
            skLineSegment(sketch, "E665", {"start": v(1.6, 4.03) * mm, "end": v(1.66, 4.07) * mm});
            skLineSegment(sketch, "E666", {"start": v(1.53, 3.98) * mm, "end": v(1.6, 4.03) * mm});
            skLineSegment(sketch, "E667", {"start": v(1.48, 3.93) * mm, "end": v(1.53, 3.98) * mm});
            skLineSegment(sketch, "E668", {"start": v(1.43, 3.89) * mm, "end": v(1.48, 3.93) * mm});
            skLineSegment(sketch, "E669", {"start": v(1.38, 3.84) * mm, "end": v(1.43, 3.89) * mm});
            skLineSegment(sketch, "E670", {"start": v(1.34, 3.8) * mm, "end": v(1.38, 3.84) * mm});
            skLineSegment(sketch, "E671", {"start": v(1.3, 3.76) * mm, "end": v(1.34, 3.8) * mm});
            skLineSegment(sketch, "E672", {"start": v(1.27, 3.72) * mm, "end": v(1.3, 3.76) * mm});
            skLineSegment(sketch, "E673", {"start": v(1.25, 3.69) * mm, "end": v(1.27, 3.72) * mm});
            skLineSegment(sketch, "E674", {"start": v(1.22, 3.66) * mm, "end": v(1.25, 3.69) * mm});
            skLineSegment(sketch, "E675", {"start": v(1.2, 3.63) * mm, "end": v(1.22, 3.66) * mm});
            skLineSegment(sketch, "E676", {"start": v(1.18, 3.6) * mm, "end": v(1.2, 3.63) * mm});
            skLineSegment(sketch, "E677", {"start": v(1.17, 3.58) * mm, "end": v(1.18, 3.6) * mm});
            skLineSegment(sketch, "E678", {"start": v(1.16, 3.56) * mm, "end": v(1.17, 3.58) * mm});
            skLineSegment(sketch, "E679", {"start": v(1.15, 3.54) * mm, "end": v(1.16, 3.56) * mm});
            skLineSegment(sketch, "E680", {"start": v(1.15, 3.53) * mm, "end": v(1.15, 3.54) * mm});
            skLineSegment(sketch, "E681", {"start": v(1.14, 3.52) * mm, "end": v(1.15, 3.53) * mm});
            skLineSegment(sketch, "E682", {"start": v(1.14, 3.52) * mm, "end": v(1.14, 3.52) * mm});
            skLineSegment(sketch, "E683", {"start": v(0.99, 3.04) * mm, "end": v(1.14, 3.52) * mm});
            skLineSegment(sketch, "E684", {"start": v(0.24, 3.18) * mm, "end": v(0.99, 3.04) * mm});
            skLineSegment(sketch, "E685", {"start": v(0.28, 3.69) * mm, "end": v(0.24, 3.18) * mm});
            skLineSegment(sketch, "E686", {"start": v(0.28, 3.7) * mm, "end": v(0.28, 3.69) * mm});
            skLineSegment(sketch, "E687", {"start": v(0.28, 3.7) * mm, "end": v(0.28, 3.7) * mm});
            skLineSegment(sketch, "E688", {"start": v(0.28, 3.71) * mm, "end": v(0.28, 3.7) * mm});
            skLineSegment(sketch, "E689", {"start": v(0.28, 3.73) * mm, "end": v(0.28, 3.71) * mm});
            skLineSegment(sketch, "E690", {"start": v(0.27, 3.75) * mm, "end": v(0.28, 3.73) * mm});
            skLineSegment(sketch, "E691", {"start": v(0.27, 3.78) * mm, "end": v(0.27, 3.75) * mm});
            skLineSegment(sketch, "E692", {"start": v(0.27, 3.81) * mm, "end": v(0.27, 3.78) * mm});
            skLineSegment(sketch, "E693", {"start": v(0.26, 3.85) * mm, "end": v(0.27, 3.81) * mm});
            skLineSegment(sketch, "E694", {"start": v(0.25, 3.89) * mm, "end": v(0.26, 3.85) * mm});
            skLineSegment(sketch, "E695", {"start": v(0.24, 3.93) * mm, "end": v(0.25, 3.89) * mm});
            skLineSegment(sketch, "E696", {"start": v(0.22, 3.98) * mm, "end": v(0.24, 3.93) * mm});
            skLineSegment(sketch, "E697", {"start": v(0.2, 4.03) * mm, "end": v(0.22, 3.98) * mm});
            skLineSegment(sketch, "E698", {"start": v(0.18, 4.08) * mm, "end": v(0.2, 4.03) * mm});
            skLineSegment(sketch, "E699", {"start": v(0.16, 4.14) * mm, "end": v(0.18, 4.08) * mm});
            skLineSegment(sketch, "E700", {"start": v(0.13, 4.2) * mm, "end": v(0.16, 4.14) * mm});
            skLineSegment(sketch, "E701", {"start": v(0.1, 4.26) * mm, "end": v(0.13, 4.2) * mm});
            skLineSegment(sketch, "E702", {"start": v(0.05, 4.33) * mm, "end": v(0.1, 4.26) * mm});
            skLineSegment(sketch, "E703", {"start": v(0.01, 4.4) * mm, "end": v(0.05, 4.33) * mm});
            skLineSegment(sketch, "E704", {"start": v(-0.04, 4.47) * mm, "end": v(0.01, 4.4) * mm});
            skLineSegment(sketch, "E705", {"start": v(-0.09, 4.54) * mm, "end": v(-0.04, 4.47) * mm});
            skLineSegment(sketch, "E706", {"start": v(-0.15, 4.62) * mm, "end": v(-0.09, 4.54) * mm});
            skLineSegment(sketch, "E707", {"start": v(-0.2, 4.7) * mm, "end": v(-0.15, 4.62) * mm});
            skLineSegment(sketch, "E708", {"start": v(-0.28, 4.77) * mm, "end": v(-0.2, 4.7) * mm});
            skLineSegment(sketch, "E709", {"start": v(-0.35, 4.85) * mm, "end": v(-0.28, 4.77) * mm});
            skLineSegment(sketch, "E710", {"start": v(-0.43, 4.93) * mm, "end": v(-0.35, 4.85) * mm});
            skLineSegment(sketch, "E711", {"start": v(-0.51, 4.95) * mm, "end": v(-0.43, 4.93) * mm});
            skLineSegment(sketch, "E712", {"start": v(-0.67, 4.93) * mm, "end": v(-0.51, 4.95) * mm});
            skLineSegment(sketch, "E713", {"start": v(-0.75, 4.9) * mm, "end": v(-0.67, 4.93) * mm});
            skLineSegment(sketch, "E714", {"start": v(-0.8, 4.8) * mm, "end": v(-0.75, 4.9) * mm});
            skLineSegment(sketch, "E715", {"start": v(-0.86, 4.7) * mm, "end": v(-0.8, 4.8) * mm});
            skLineSegment(sketch, "E716", {"start": v(-0.9, 4.61) * mm, "end": v(-0.86, 4.7) * mm});
            skLineSegment(sketch, "E717", {"start": v(-0.95, 4.52) * mm, "end": v(-0.9, 4.61) * mm});
            skLineSegment(sketch, "E718", {"start": v(-1, 4.44) * mm, "end": v(-0.95, 4.52) * mm});
            skLineSegment(sketch, "E719", {"start": v(-1.02, 4.35) * mm, "end": v(-1, 4.44) * mm});
            skLineSegment(sketch, "E720", {"start": v(-1.05, 4.27) * mm, "end": v(-1.02, 4.35) * mm});
            skLineSegment(sketch, "E721", {"start": v(-1.08, 4.2) * mm, "end": v(-1.05, 4.27) * mm});
            skLineSegment(sketch, "E722", {"start": v(-1.1, 4.12) * mm, "end": v(-1.08, 4.2) * mm});
            skLineSegment(sketch, "E723", {"start": v(-1.12, 4.05) * mm, "end": v(-1.1, 4.12) * mm});
            skLineSegment(sketch, "E724", {"start": v(-1.13, 3.98) * mm, "end": v(-1.12, 4.05) * mm});
            skLineSegment(sketch, "E725", {"start": v(-1.14, 3.92) * mm, "end": v(-1.13, 3.98) * mm});
            skLineSegment(sketch, "E726", {"start": v(-1.15, 3.86) * mm, "end": v(-1.14, 3.92) * mm});
            skLineSegment(sketch, "E727", {"start": v(-1.16, 3.81) * mm, "end": v(-1.15, 3.86) * mm});
            skLineSegment(sketch, "E728", {"start": v(-1.16, 3.76) * mm, "end": v(-1.16, 3.81) * mm});
            skLineSegment(sketch, "E729", {"start": v(-1.16, 3.72) * mm, "end": v(-1.16, 3.76) * mm});
            skLineSegment(sketch, "E730", {"start": v(-1.16, 3.68) * mm, "end": v(-1.16, 3.72) * mm});
            skLineSegment(sketch, "E731", {"start": v(-1.16, 3.64) * mm, "end": v(-1.16, 3.68) * mm});
            skLineSegment(sketch, "E732", {"start": v(-1.16, 3.6) * mm, "end": v(-1.16, 3.64) * mm});
            skLineSegment(sketch, "E733", {"start": v(-1.15, 3.58) * mm, "end": v(-1.16, 3.6) * mm});
            skLineSegment(sketch, "E734", {"start": v(-1.15, 3.56) * mm, "end": v(-1.15, 3.58) * mm});
            skLineSegment(sketch, "E735", {"start": v(-1.15, 3.54) * mm, "end": v(-1.15, 3.56) * mm});
            skLineSegment(sketch, "E736", {"start": v(-1.15, 3.53) * mm, "end": v(-1.15, 3.54) * mm});
            skLineSegment(sketch, "E737", {"start": v(-1.14, 3.52) * mm, "end": v(-1.15, 3.53) * mm});
            skLineSegment(sketch, "E738", {"start": v(-1.14, 3.52) * mm, "end": v(-1.14, 3.52) * mm});
            skLineSegment(sketch, "E739", {"start": v(-0.99, 3.04) * mm, "end": v(-1.14, 3.52) * mm});
            skLineSegment(sketch, "E740", {"start": v(-1.68, 2.72) * mm, "end": v(-0.99, 3.04) * mm});
            skLineSegment(sketch, "E741", {"start": v(-1.94, 3.15) * mm, "end": v(-1.68, 2.72) * mm});
            skLineSegment(sketch, "E742", {"start": v(-1.94, 3.15) * mm, "end": v(-1.94, 3.15) * mm});
            skLineSegment(sketch, "E743", {"start": v(-1.95, 3.16) * mm, "end": v(-1.94, 3.15) * mm});
            skLineSegment(sketch, "E744", {"start": v(-1.96, 3.17) * mm, "end": v(-1.95, 3.16) * mm});
            skLineSegment(sketch, "E745", {"start": v(-1.97, 3.18) * mm, "end": v(-1.96, 3.17) * mm});
            skLineSegment(sketch, "E746", {"start": v(-1.98, 3.2) * mm, "end": v(-1.97, 3.18) * mm});
            skLineSegment(sketch, "E747", {"start": v(-2, 3.22) * mm, "end": v(-1.98, 3.2) * mm});
            skLineSegment(sketch, "E748", {"start": v(-2.03, 3.24) * mm, "end": v(-2, 3.22) * mm});
            skLineSegment(sketch, "E749", {"start": v(-2.05, 3.26) * mm, "end": v(-2.03, 3.24) * mm});
            skLineSegment(sketch, "E750", {"start": v(-2.08, 3.29) * mm, "end": v(-2.05, 3.26) * mm});
            skLineSegment(sketch, "E751", {"start": v(-2.12, 3.32) * mm, "end": v(-2.08, 3.29) * mm});
            skLineSegment(sketch, "E752", {"start": v(-2.16, 3.35) * mm, "end": v(-2.12, 3.32) * mm});
            skLineSegment(sketch, "E753", {"start": v(-2.2, 3.38) * mm, "end": v(-2.16, 3.35) * mm});
            skLineSegment(sketch, "E754", {"start": v(-2.25, 3.4) * mm, "end": v(-2.2, 3.38) * mm});
            skLineSegment(sketch, "E755", {"start": v(-2.3, 3.44) * mm, "end": v(-2.25, 3.4) * mm});
            skLineSegment(sketch, "E756", {"start": v(-2.37, 3.47) * mm, "end": v(-2.3, 3.44) * mm});
            skLineSegment(sketch, "E757", {"start": v(-2.43, 3.5) * mm, "end": v(-2.37, 3.47) * mm});
            skLineSegment(sketch, "E758", {"start": v(-2.5, 3.54) * mm, "end": v(-2.43, 3.5) * mm});
            skLineSegment(sketch, "E759", {"start": v(-2.58, 3.57) * mm, "end": v(-2.5, 3.54) * mm});
            skLineSegment(sketch, "E760", {"start": v(-2.66, 3.6) * mm, "end": v(-2.58, 3.57) * mm});
            skLineSegment(sketch, "E761", {"start": v(-2.74, 3.62) * mm, "end": v(-2.66, 3.6) * mm});
            skLineSegment(sketch, "E762", {"start": v(-2.83, 3.65) * mm, "end": v(-2.74, 3.62) * mm});
            skLineSegment(sketch, "E763", {"start": v(-2.93, 3.68) * mm, "end": v(-2.83, 3.65) * mm});
            skLineSegment(sketch, "E764", {"start": v(-3.03, 3.7) * mm, "end": v(-2.93, 3.68) * mm});
            skLineSegment(sketch, "E765", {"start": v(-3.14, 3.72) * mm, "end": v(-3.03, 3.7) * mm});
            skLineSegment(sketch, "E766", {"start": v(-3.25, 3.73) * mm, "end": v(-3.14, 3.72) * mm});
            skLineSegment(sketch, "E767", {"start": v(-3.33, 3.7) * mm, "end": v(-3.25, 3.73) * mm});
            skLineSegment(sketch, "E768", {"start": v(-3.44, 3.6) * mm, "end": v(-3.33, 3.7) * mm});
            skLineSegment(sketch, "E769", {"start": v(-3.48, 3.52) * mm, "end": v(-3.44, 3.6) * mm});
            skLineSegment(sketch, "E770", {"start": v(-3.47, 3.4) * mm, "end": v(-3.48, 3.52) * mm});
            skLineSegment(sketch, "E771", {"start": v(-3.46, 3.3) * mm, "end": v(-3.47, 3.4) * mm});
            skLineSegment(sketch, "E772", {"start": v(-3.45, 3.2) * mm, "end": v(-3.46, 3.3) * mm});
            skLineSegment(sketch, "E773", {"start": v(-3.43, 3.1) * mm, "end": v(-3.45, 3.2) * mm});
            skLineSegment(sketch, "E774", {"start": v(-3.4, 3) * mm, "end": v(-3.43, 3.1) * mm});
            skLineSegment(sketch, "E775", {"start": v(-3.39, 2.92) * mm, "end": v(-3.4, 3) * mm});
            skLineSegment(sketch, "E776", {"start": v(-3.36, 2.84) * mm, "end": v(-3.39, 2.92) * mm});
            skLineSegment(sketch, "E777", {"start": v(-3.34, 2.76) * mm, "end": v(-3.36, 2.84) * mm});
            skLineSegment(sketch, "E778", {"start": v(-3.31, 2.69) * mm, "end": v(-3.34, 2.76) * mm});
            skLineSegment(sketch, "E779", {"start": v(-3.28, 2.62) * mm, "end": v(-3.31, 2.69) * mm});
            skLineSegment(sketch, "E780", {"start": v(-3.26, 2.56) * mm, "end": v(-3.28, 2.62) * mm});
            skLineSegment(sketch, "E781", {"start": v(-3.23, 2.5) * mm, "end": v(-3.26, 2.56) * mm});
            skLineSegment(sketch, "E782", {"start": v(-3.2, 2.45) * mm, "end": v(-3.23, 2.5) * mm});
            skLineSegment(sketch, "E783", {"start": v(-3.18, 2.4) * mm, "end": v(-3.2, 2.45) * mm});
            skLineSegment(sketch, "E784", {"start": v(-3.15, 2.36) * mm, "end": v(-3.18, 2.4) * mm});
            skLineSegment(sketch, "E785", {"start": v(-3.12, 2.32) * mm, "end": v(-3.15, 2.36) * mm});
            skLineSegment(sketch, "E786", {"start": v(-3.1, 2.3) * mm, "end": v(-3.12, 2.32) * mm});
            skLineSegment(sketch, "E787", {"start": v(-3.08, 2.26) * mm, "end": v(-3.1, 2.3) * mm});
            skLineSegment(sketch, "E788", {"start": v(-3.06, 2.24) * mm, "end": v(-3.08, 2.26) * mm});
            skLineSegment(sketch, "E789", {"start": v(-3.04, 2.22) * mm, "end": v(-3.06, 2.24) * mm});
            skLineSegment(sketch, "E790", {"start": v(-3.02, 2.2) * mm, "end": v(-3.04, 2.22) * mm});
            skLineSegment(sketch, "E791", {"start": v(-3.01, 2.2) * mm, "end": v(-3.02, 2.2) * mm});
            skLineSegment(sketch, "E792", {"start": v(-3, 2.18) * mm, "end": v(-3.01, 2.2) * mm});
            skLineSegment(sketch, "E793", {"start": v(-3, 2.18) * mm, "end": v(-3, 2.18) * mm});
            skLineSegment(sketch, "E794", {"start": v(-3, 2.17) * mm, "end": v(-3, 2.18) * mm});
            skLineSegment(sketch, "E795", {"start": v(-2.58, 1.88) * mm, "end": v(-3, 2.17) * mm});
            skLineSegment(sketch, "E796", {"start": v(-2.95, 1.21) * mm, "end": v(-2.58, 1.88) * mm});
            skLineSegment(sketch, "E797", {"start": v(-3.42, 1.4) * mm, "end": v(-2.95, 1.21) * mm});
            skLineSegment(sketch, "E798", {"start": v(-3.42, 1.4) * mm, "end": v(-3.42, 1.4) * mm});
            skLineSegment(sketch, "E799", {"start": v(-3.43, 1.4) * mm, "end": v(-3.42, 1.4) * mm});
            skLineSegment(sketch, "E800", {"start": v(-3.45, 1.41) * mm, "end": v(-3.43, 1.4) * mm});
            skLineSegment(sketch, "E801", {"start": v(-3.46, 1.42) * mm, "end": v(-3.45, 1.41) * mm});
            skLineSegment(sketch, "E802", {"start": v(-3.48, 1.42) * mm, "end": v(-3.46, 1.42) * mm});
            skLineSegment(sketch, "E803", {"start": v(-3.51, 1.43) * mm, "end": v(-3.48, 1.42) * mm});
            skLineSegment(sketch, "E804", {"start": v(-3.54, 1.43) * mm, "end": v(-3.51, 1.43) * mm});
            skLineSegment(sketch, "E805", {"start": v(-3.58, 1.43) * mm, "end": v(-3.54, 1.43) * mm});
            skLineSegment(sketch, "E806", {"start": v(-3.62, 1.44) * mm, "end": v(-3.58, 1.43) * mm});
            skLineSegment(sketch, "E807", {"start": v(-3.66, 1.44) * mm, "end": v(-3.62, 1.44) * mm});
            skLineSegment(sketch, "E808", {"start": v(-3.71, 1.44) * mm, "end": v(-3.66, 1.44) * mm});
            skLineSegment(sketch, "E809", {"start": v(-3.77, 1.44) * mm, "end": v(-3.71, 1.44) * mm});
            skLineSegment(sketch, "E810", {"start": v(-3.83, 1.43) * mm, "end": v(-3.77, 1.44) * mm});
            skLineSegment(sketch, "E811", {"start": v(-3.89, 1.43) * mm, "end": v(-3.83, 1.43) * mm});
            skLineSegment(sketch, "E812", {"start": v(-3.96, 1.42) * mm, "end": v(-3.89, 1.43) * mm});
            skLineSegment(sketch, "E813", {"start": v(-4.03, 1.4) * mm, "end": v(-3.96, 1.42) * mm});
            skLineSegment(sketch, "E814", {"start": v(-4.1, 1.4) * mm, "end": v(-4.03, 1.4) * mm});
            skLineSegment(sketch, "E815", {"start": v(-4.18, 1.37) * mm, "end": v(-4.1, 1.4) * mm});
            skLineSegment(sketch, "E816", {"start": v(-4.26, 1.35) * mm, "end": v(-4.18, 1.37) * mm});
            skLineSegment(sketch, "E817", {"start": v(-4.35, 1.32) * mm, "end": v(-4.26, 1.35) * mm});
            skLineSegment(sketch, "E818", {"start": v(-4.44, 1.29) * mm, "end": v(-4.35, 1.32) * mm});
            skLineSegment(sketch, "E819", {"start": v(-4.53, 1.25) * mm, "end": v(-4.44, 1.29) * mm});
            skLineSegment(sketch, "E820", {"start": v(-4.62, 1.21) * mm, "end": v(-4.53, 1.25) * mm});
            skLineSegment(sketch, "E821", {"start": v(-4.72, 1.16) * mm, "end": v(-4.62, 1.21) * mm});
            skLineSegment(sketch, "E822", {"start": v(-4.82, 1.11) * mm, "end": v(-4.72, 1.16) * mm});
            skLineSegment(sketch, "E823", {"start": v(-4.87, 1.04) * mm, "end": v(-4.82, 1.11) * mm});
            skLineSegment(sketch, "E824", {"start": v(-4.9, 0.88) * mm, "end": v(-4.87, 1.04) * mm});
            skLineSegment(sketch, "E825", {"start": v(-4.88, 0.8) * mm, "end": v(-4.9, 0.88) * mm});
            skLineSegment(sketch, "E826", {"start": v(-4.8, 0.72) * mm, "end": v(-4.88, 0.8) * mm});
            skLineSegment(sketch, "E827", {"start": v(-4.74, 0.64) * mm, "end": v(-4.8, 0.72) * mm});
            skLineSegment(sketch, "E828", {"start": v(-4.67, 0.56) * mm, "end": v(-4.74, 0.64) * mm});
            skLineSegment(sketch, "E829", {"start": v(-4.6, 0.5) * mm, "end": v(-4.67, 0.56) * mm});
            skLineSegment(sketch, "E830", {"start": v(-4.52, 0.43) * mm, "end": v(-4.6, 0.5) * mm});
            skLineSegment(sketch, "E831", {"start": v(-4.46, 0.37) * mm, "end": v(-4.52, 0.43) * mm});
            skLineSegment(sketch, "E832", {"start": v(-4.39, 0.32) * mm, "end": v(-4.46, 0.37) * mm});
            skLineSegment(sketch, "E833", {"start": v(-4.32, 0.27) * mm, "end": v(-4.39, 0.32) * mm});
            skLineSegment(sketch, "E834", {"start": v(-4.26, 0.23) * mm, "end": v(-4.32, 0.27) * mm});
            skLineSegment(sketch, "E835", {"start": v(-4.2, 0.19) * mm, "end": v(-4.26, 0.23) * mm});
            skLineSegment(sketch, "E836", {"start": v(-4.14, 0.16) * mm, "end": v(-4.2, 0.19) * mm});
            skLineSegment(sketch, "E837", {"start": v(-4.08, 0.13) * mm, "end": v(-4.14, 0.16) * mm});
            skLineSegment(sketch, "E838", {"start": v(-4.03, 0.1) * mm, "end": v(-4.08, 0.13) * mm});
            skLineSegment(sketch, "E839", {"start": v(-3.98, 0.08) * mm, "end": v(-4.03, 0.1) * mm});
            skLineSegment(sketch, "E840", {"start": v(-3.94, 0.06) * mm, "end": v(-3.98, 0.08) * mm});
            skLineSegment(sketch, "E841", {"start": v(-3.9, 0.04) * mm, "end": v(-3.94, 0.06) * mm});
            skLineSegment(sketch, "E842", {"start": v(-3.85, 0.03) * mm, "end": v(-3.9, 0.04) * mm});
            skLineSegment(sketch, "E843", {"start": v(-3.82, 0.02) * mm, "end": v(-3.85, 0.03) * mm});
            skLineSegment(sketch, "E844", {"start": v(-3.79, 0.01) * mm, "end": v(-3.82, 0.02) * mm});
            skLineSegment(sketch, "E845", {"start": v(-3.76, 0) * mm, "end": v(-3.79, 0.01) * mm});
            skLineSegment(sketch, "E846", {"start": v(-3.74, 0) * mm, "end": v(-3.76, 0) * mm});
            skLineSegment(sketch, "E847", {"start": v(-3.72, 0) * mm, "end": v(-3.74, 0) * mm});
            skLineSegment(sketch, "E848", {"start": v(-3.7, 0) * mm, "end": v(-3.72, 0) * mm});
            skLineSegment(sketch, "E849", {"start": v(-3.7, 0) * mm, "end": v(-3.7, 0) * mm});
            skLineSegment(sketch, "E850", {"start": v(-3.2, 0) * mm, "end": v(-3.7, 0) * mm});
            skLineSegment(sketch, "E851", {"start": v(-3.1, -0.76) * mm, "end": v(-3.2, 0) * mm});
            skLineSegment(sketch, "E852", {"start": v(-3.6, -0.87) * mm, "end": v(-3.1, -0.76) * mm});
            skLineSegment(sketch, "E853", {"start": v(-3.6, -0.88) * mm, "end": v(-3.6, -0.87) * mm});
            skLineSegment(sketch, "E854", {"start": v(-3.6, -0.88) * mm, "end": v(-3.6, -0.88) * mm});
            skLineSegment(sketch, "E855", {"start": v(-3.62, -0.88) * mm, "end": v(-3.6, -0.88) * mm});
            skLineSegment(sketch, "E856", {"start": v(-3.63, -0.9) * mm, "end": v(-3.62, -0.88) * mm});
            skLineSegment(sketch, "E857", {"start": v(-3.65, -0.9) * mm, "end": v(-3.63, -0.9) * mm});
            skLineSegment(sketch, "E858", {"start": v(-3.68, -0.91) * mm, "end": v(-3.65, -0.9) * mm});
            skLineSegment(sketch, "E859", {"start": v(-3.7, -0.93) * mm, "end": v(-3.68, -0.91) * mm});
            skLineSegment(sketch, "E860", {"start": v(-3.74, -0.94) * mm, "end": v(-3.7, -0.93) * mm});
            skLineSegment(sketch, "E861", {"start": v(-3.77, -0.96) * mm, "end": v(-3.74, -0.94) * mm});
            skLineSegment(sketch, "E862", {"start": v(-3.8, -0.99) * mm, "end": v(-3.77, -0.96) * mm});
            skLineSegment(sketch, "E863", {"start": v(-3.85, -1.02) * mm, "end": v(-3.8, -0.99) * mm});
            skLineSegment(sketch, "E864", {"start": v(-3.9, -1.05) * mm, "end": v(-3.85, -1.02) * mm});
            skLineSegment(sketch, "E865", {"start": v(-3.94, -1.09) * mm, "end": v(-3.9, -1.05) * mm});
            skLineSegment(sketch, "E866", {"start": v(-3.98, -1.13) * mm, "end": v(-3.94, -1.09) * mm});
            skLineSegment(sketch, "E867", {"start": v(-4.03, -1.18) * mm, "end": v(-3.98, -1.13) * mm});
            skLineSegment(sketch, "E868", {"start": v(-4.08, -1.23) * mm, "end": v(-4.03, -1.18) * mm});
            skLineSegment(sketch, "E869", {"start": v(-4.14, -1.29) * mm, "end": v(-4.08, -1.23) * mm});
            skLineSegment(sketch, "E870", {"start": v(-4.19, -1.35) * mm, "end": v(-4.14, -1.29) * mm});
            skLineSegment(sketch, "E871", {"start": v(-4.24, -1.41) * mm, "end": v(-4.19, -1.35) * mm});
            skLineSegment(sketch, "E872", {"start": v(-4.3, -1.49) * mm, "end": v(-4.24, -1.41) * mm});
            skLineSegment(sketch, "E873", {"start": v(-4.35, -1.57) * mm, "end": v(-4.3, -1.49) * mm});
            skLineSegment(sketch, "E874", {"start": v(-4.4, -1.65) * mm, "end": v(-4.35, -1.57) * mm});
            skLineSegment(sketch, "E875", {"start": v(-4.45, -1.74) * mm, "end": v(-4.4, -1.65) * mm});
            skLineSegment(sketch, "E876", {"start": v(-4.5, -1.83) * mm, "end": v(-4.45, -1.74) * mm});
            skLineSegment(sketch, "E877", {"start": v(-4.55, -1.93) * mm, "end": v(-4.5, -1.83) * mm});
            skLineSegment(sketch, "E878", {"start": v(-4.55, -2.02) * mm, "end": v(-4.55, -1.93) * mm});
            skLineSegment(sketch, "E879", {"start": v(-4.48, -2.16) * mm, "end": v(-4.55, -2.02) * mm});
            skLineSegment(sketch, "E880", {"start": v(-4.42, -2.22) * mm, "end": v(-4.48, -2.16) * mm});
            skLineSegment(sketch, "E881", {"start": v(-4.31, -2.25) * mm, "end": v(-4.42, -2.22) * mm});
            skLineSegment(sketch, "E882", {"start": v(-4.2, -2.27) * mm, "end": v(-4.31, -2.25) * mm});
            skLineSegment(sketch, "E883", {"start": v(-4.1, -2.29) * mm, "end": v(-4.2, -2.27) * mm});
            skLineSegment(sketch, "E884", {"start": v(-4, -2.3) * mm, "end": v(-4.1, -2.29) * mm});
            skLineSegment(sketch, "E885", {"start": v(-3.91, -2.31) * mm, "end": v(-4, -2.3) * mm});
            skLineSegment(sketch, "E886", {"start": v(-3.82, -2.32) * mm, "end": v(-3.91, -2.31) * mm});
            skLineSegment(sketch, "E887", {"start": v(-3.74, -2.32) * mm, "end": v(-3.82, -2.32) * mm});
            skLineSegment(sketch, "E888", {"start": v(-3.66, -2.32) * mm, "end": v(-3.74, -2.32) * mm});
            skLineSegment(sketch, "E889", {"start": v(-3.58, -2.32) * mm, "end": v(-3.66, -2.32) * mm});
            skLineSegment(sketch, "E890", {"start": v(-3.5, -2.31) * mm, "end": v(-3.58, -2.32) * mm});
            skLineSegment(sketch, "E891", {"start": v(-3.44, -2.3) * mm, "end": v(-3.5, -2.31) * mm});
            skLineSegment(sketch, "E892", {"start": v(-3.38, -2.3) * mm, "end": v(-3.44, -2.3) * mm});
            skLineSegment(sketch, "E893", {"start": v(-3.32, -2.29) * mm, "end": v(-3.38, -2.3) * mm});
            skLineSegment(sketch, "E894", {"start": v(-3.27, -2.28) * mm, "end": v(-3.32, -2.29) * mm});
            skLineSegment(sketch, "E895", {"start": v(-3.22, -2.26) * mm, "end": v(-3.27, -2.28) * mm});
            skLineSegment(sketch, "E896", {"start": v(-3.18, -2.25) * mm, "end": v(-3.22, -2.26) * mm});
            skLineSegment(sketch, "E897", {"start": v(-3.14, -2.24) * mm, "end": v(-3.18, -2.25) * mm});
            skLineSegment(sketch, "E898", {"start": v(-3.1, -2.23) * mm, "end": v(-3.14, -2.24) * mm});
            skLineSegment(sketch, "E899", {"start": v(-3.07, -2.22) * mm, "end": v(-3.1, -2.23) * mm});
            skLineSegment(sketch, "E900", {"start": v(-3.05, -2.2) * mm, "end": v(-3.07, -2.22) * mm});
            skLineSegment(sketch, "E901", {"start": v(-3.03, -2.2) * mm, "end": v(-3.05, -2.2) * mm});
            skLineSegment(sketch, "E902", {"start": v(-3.01, -2.19) * mm, "end": v(-3.03, -2.2) * mm});
            skLineSegment(sketch, "E903", {"start": v(-3, -2.18) * mm, "end": v(-3.01, -2.19) * mm});
            skLineSegment(sketch, "E904", {"start": v(-3, -2.18) * mm, "end": v(-3, -2.18) * mm});
            skLineSegment(sketch, "E905", {"start": v(-3, -2.17) * mm, "end": v(-3, -2.18) * mm});
            skLineSegment(sketch, "E906", {"start": v(-2.58, -1.88) * mm, "end": v(-3, -2.17) * mm});
            skLineSegment(sketch, "E907", {"start": v(-2.07, -2.44) * mm, "end": v(-2.58, -1.88) * mm});
            skLineSegment(sketch, "E908", {"start": v(-2.4, -2.82) * mm, "end": v(-2.07, -2.44) * mm});
            skLineSegment(sketch, "E909", {"start": v(-2.4, -2.82) * mm, "end": v(-2.4, -2.82) * mm});
            skLineSegment(sketch, "E910", {"start": v(-2.4, -2.83) * mm, "end": v(-2.4, -2.82) * mm});
            skLineSegment(sketch, "E911", {"start": v(-2.4, -2.84) * mm, "end": v(-2.4, -2.83) * mm});
            skLineSegment(sketch, "E912", {"start": v(-2.42, -2.86) * mm, "end": v(-2.4, -2.84) * mm});
            skLineSegment(sketch, "E913", {"start": v(-2.43, -2.88) * mm, "end": v(-2.42, -2.86) * mm});
            skLineSegment(sketch, "E914", {"start": v(-2.44, -2.9) * mm, "end": v(-2.43, -2.88) * mm});
            skLineSegment(sketch, "E915", {"start": v(-2.45, -2.93) * mm, "end": v(-2.44, -2.9) * mm});
            skLineSegment(sketch, "E916", {"start": v(-2.47, -2.96) * mm, "end": v(-2.45, -2.93) * mm});
            skLineSegment(sketch, "E917", {"start": v(-2.48, -3) * mm, "end": v(-2.47, -2.96) * mm});
            skLineSegment(sketch, "E918", {"start": v(-2.5, -3.04) * mm, "end": v(-2.48, -3) * mm});
            skLineSegment(sketch, "E919", {"start": v(-2.52, -3.09) * mm, "end": v(-2.5, -3.04) * mm});
            skLineSegment(sketch, "E920", {"start": v(-2.53, -3.14) * mm, "end": v(-2.52, -3.09) * mm});
            skLineSegment(sketch, "E921", {"start": v(-2.55, -3.2) * mm, "end": v(-2.53, -3.14) * mm});
            skLineSegment(sketch, "E922", {"start": v(-2.56, -3.26) * mm, "end": v(-2.55, -3.2) * mm});
            skLineSegment(sketch, "E923", {"start": v(-2.57, -3.32) * mm, "end": v(-2.56, -3.26) * mm});
            skLineSegment(sketch, "E924", {"start": v(-2.58, -3.4) * mm, "end": v(-2.57, -3.32) * mm});
            skLineSegment(sketch, "E925", {"start": v(-2.59, -3.47) * mm, "end": v(-2.58, -3.4) * mm});
            skLineSegment(sketch, "E926", {"start": v(-2.6, -3.55) * mm, "end": v(-2.59, -3.47) * mm});
            skLineSegment(sketch, "E927", {"start": v(-2.6, -3.64) * mm, "end": v(-2.6, -3.55) * mm});
            skLineSegment(sketch, "E928", {"start": v(-2.6, -3.73) * mm, "end": v(-2.6, -3.64) * mm});
            skLineSegment(sketch, "E929", {"start": v(-2.6, -3.82) * mm, "end": v(-2.6, -3.73) * mm});
            skLineSegment(sketch, "E930", {"start": v(-2.6, -3.92) * mm, "end": v(-2.6, -3.82) * mm});
            skLineSegment(sketch, "E931", {"start": v(-2.58, -4.02) * mm, "end": v(-2.6, -3.92) * mm});
            skLineSegment(sketch, "E932", {"start": v(-2.57, -4.13) * mm, "end": v(-2.58, -4.02) * mm});
            skLineSegment(sketch, "E933", {"start": v(-2.55, -4.24) * mm, "end": v(-2.57, -4.13) * mm});
            skLineSegment(sketch, "E934", {"start": v(-2.5, -4.3) * mm, "end": v(-2.55, -4.24) * mm});
            skLineSegment(sketch, "E935", {"start": v(-2.35, -4.39) * mm, "end": v(-2.5, -4.3) * mm});
            skLineSegment(sketch, "E936", {"start": v(-2.27, -4.4) * mm, "end": v(-2.35, -4.39) * mm});
            skLineSegment(sketch, "E937", {"start": v(-2.17, -4.35) * mm, "end": v(-2.27, -4.4) * mm});
            skLineSegment(sketch, "E938", {"start": v(-2.07, -4.3) * mm, "end": v(-2.17, -4.35) * mm});
            skLineSegment(sketch, "E939", {"start": v(-1.98, -4.26) * mm, "end": v(-2.07, -4.3) * mm});
            skLineSegment(sketch, "E940", {"start": v(-1.89, -4.22) * mm, "end": v(-1.98, -4.26) * mm});
            skLineSegment(sketch, "E941", {"start": v(-1.8, -4.17) * mm, "end": v(-1.89, -4.22) * mm});
            skLineSegment(sketch, "E942", {"start": v(-1.73, -4.12) * mm, "end": v(-1.8, -4.17) * mm});
            skLineSegment(sketch, "E943", {"start": v(-1.66, -4.07) * mm, "end": v(-1.73, -4.12) * mm});
            skLineSegment(sketch, "E944", {"start": v(-1.6, -4.03) * mm, "end": v(-1.66, -4.07) * mm});
            skLineSegment(sketch, "E945", {"start": v(-1.53, -3.98) * mm, "end": v(-1.6, -4.03) * mm});
            skLineSegment(sketch, "E946", {"start": v(-1.48, -3.93) * mm, "end": v(-1.53, -3.98) * mm});
            skLineSegment(sketch, "E947", {"start": v(-1.43, -3.89) * mm, "end": v(-1.48, -3.93) * mm});
            skLineSegment(sketch, "E948", {"start": v(-1.38, -3.84) * mm, "end": v(-1.43, -3.89) * mm});
            skLineSegment(sketch, "E949", {"start": v(-1.34, -3.8) * mm, "end": v(-1.38, -3.84) * mm});
            skLineSegment(sketch, "E950", {"start": v(-1.3, -3.76) * mm, "end": v(-1.34, -3.8) * mm});
            skLineSegment(sketch, "E951", {"start": v(-1.27, -3.72) * mm, "end": v(-1.3, -3.76) * mm});
            skLineSegment(sketch, "E952", {"start": v(-1.25, -3.69) * mm, "end": v(-1.27, -3.72) * mm});
            skLineSegment(sketch, "E953", {"start": v(-1.22, -3.66) * mm, "end": v(-1.25, -3.69) * mm});
            skLineSegment(sketch, "E954", {"start": v(-1.2, -3.63) * mm, "end": v(-1.22, -3.66) * mm});
            skLineSegment(sketch, "E955", {"start": v(-1.18, -3.6) * mm, "end": v(-1.2, -3.63) * mm});
            skLineSegment(sketch, "E956", {"start": v(-1.17, -3.58) * mm, "end": v(-1.18, -3.6) * mm});
            skLineSegment(sketch, "E957", {"start": v(-1.16, -3.56) * mm, "end": v(-1.17, -3.58) * mm});
            skLineSegment(sketch, "E958", {"start": v(-1.15, -3.54) * mm, "end": v(-1.16, -3.56) * mm});
            skLineSegment(sketch, "E959", {"start": v(-1.15, -3.53) * mm, "end": v(-1.15, -3.54) * mm});
            skLineSegment(sketch, "E960", {"start": v(-1.14, -3.52) * mm, "end": v(-1.15, -3.53) * mm});
            skLineSegment(sketch, "E961", {"start": v(-1.14, -3.52) * mm, "end": v(-1.14, -3.52) * mm});
            skLineSegment(sketch, "E962", {"start": v(-0.99, -3.04) * mm, "end": v(-1.14, -3.52) * mm});
            skLineSegment(sketch, "E963", {"start": v(-0.24, -3.18) * mm, "end": v(-0.99, -3.04) * mm});
            skLineSegment(sketch, "E964", {"start": v(-0.28, -3.69) * mm, "end": v(-0.24, -3.18) * mm});
            skLineSegment(sketch, "E965", {"start": v(-0.28, -3.7) * mm, "end": v(-0.28, -3.69) * mm});
            skLineSegment(sketch, "E966", {"start": v(-0.28, -3.7) * mm, "end": v(-0.28, -3.7) * mm});
            skLineSegment(sketch, "E967", {"start": v(-0.28, -3.71) * mm, "end": v(-0.28, -3.7) * mm});
            skLineSegment(sketch, "E968", {"start": v(-0.28, -3.73) * mm, "end": v(-0.28, -3.71) * mm});
            skLineSegment(sketch, "E969", {"start": v(-0.27, -3.75) * mm, "end": v(-0.28, -3.73) * mm});
            skLineSegment(sketch, "E970", {"start": v(-0.27, -3.78) * mm, "end": v(-0.27, -3.75) * mm});
            skLineSegment(sketch, "E971", {"start": v(-0.27, -3.81) * mm, "end": v(-0.27, -3.78) * mm});
            skLineSegment(sketch, "E972", {"start": v(-0.26, -3.85) * mm, "end": v(-0.27, -3.81) * mm});
            skLineSegment(sketch, "E973", {"start": v(-0.25, -3.89) * mm, "end": v(-0.26, -3.85) * mm});
            skLineSegment(sketch, "E974", {"start": v(-0.24, -3.93) * mm, "end": v(-0.25, -3.89) * mm});
            skLineSegment(sketch, "E975", {"start": v(-0.22, -3.98) * mm, "end": v(-0.24, -3.93) * mm});
            skLineSegment(sketch, "E976", {"start": v(-0.2, -4.03) * mm, "end": v(-0.22, -3.98) * mm});
            skLineSegment(sketch, "E977", {"start": v(-0.18, -4.08) * mm, "end": v(-0.2, -4.03) * mm});
            skLineSegment(sketch, "E978", {"start": v(-0.16, -4.14) * mm, "end": v(-0.18, -4.08) * mm});
            skLineSegment(sketch, "E979", {"start": v(-0.13, -4.2) * mm, "end": v(-0.16, -4.14) * mm});
            skLineSegment(sketch, "E980", {"start": v(-0.1, -4.26) * mm, "end": v(-0.13, -4.2) * mm});
            skLineSegment(sketch, "E981", {"start": v(-0.05, -4.33) * mm, "end": v(-0.1, -4.26) * mm});
            skLineSegment(sketch, "E982", {"start": v(-0.01, -4.4) * mm, "end": v(-0.05, -4.33) * mm});
            skLineSegment(sketch, "E983", {"start": v(0.04, -4.47) * mm, "end": v(-0.01, -4.4) * mm});
            skLineSegment(sketch, "E984", {"start": v(0.09, -4.54) * mm, "end": v(0.04, -4.47) * mm});
            skLineSegment(sketch, "E985", {"start": v(0.15, -4.62) * mm, "end": v(0.09, -4.54) * mm});
            skLineSegment(sketch, "E986", {"start": v(0.2, -4.7) * mm, "end": v(0.15, -4.62) * mm});
            skLineSegment(sketch, "E987", {"start": v(0.28, -4.77) * mm, "end": v(0.2, -4.7) * mm});
            skLineSegment(sketch, "E988", {"start": v(0.35, -4.85) * mm, "end": v(0.28, -4.77) * mm});
            skLineSegment(sketch, "E989", {"start": v(0.43, -4.93) * mm, "end": v(0.35, -4.85) * mm});
            skLineSegment(sketch, "E990", {"start": v(0.51, -4.95) * mm, "end": v(0.43, -4.93) * mm});
            skLineSegment(sketch, "E991", {"start": v(0.67, -4.93) * mm, "end": v(0.51, -4.95) * mm});
            skLineSegment(sketch, "E992", {"start": v(0.75, -4.9) * mm, "end": v(0.67, -4.93) * mm});
            skLineSegment(sketch, "E993", {"start": v(0.8, -4.8) * mm, "end": v(0.75, -4.9) * mm});
            skLineSegment(sketch, "E994", {"start": v(0.86, -4.7) * mm, "end": v(0.8, -4.8) * mm});
            skLineSegment(sketch, "E995", {"start": v(0.9, -4.61) * mm, "end": v(0.86, -4.7) * mm});
            skLineSegment(sketch, "E996", {"start": v(0.95, -4.52) * mm, "end": v(0.9, -4.61) * mm});
            skLineSegment(sketch, "E997", {"start": v(1, -4.44) * mm, "end": v(0.95, -4.52) * mm});
            skLineSegment(sketch, "E998", {"start": v(1.02, -4.35) * mm, "end": v(1, -4.44) * mm});
            skLineSegment(sketch, "E999", {"start": v(1.05, -4.27) * mm, "end": v(1.02, -4.35) * mm});
            skLineSegment(sketch, "E1000", {"start": v(1.08, -4.2) * mm, "end": v(1.05, -4.27) * mm});
            skLineSegment(sketch, "E1001", {"start": v(1.1, -4.12) * mm, "end": v(1.08, -4.2) * mm});
            skLineSegment(sketch, "E1002", {"start": v(1.12, -4.05) * mm, "end": v(1.1, -4.12) * mm});
            skLineSegment(sketch, "E1003", {"start": v(1.13, -3.98) * mm, "end": v(1.12, -4.05) * mm});
            skLineSegment(sketch, "E1004", {"start": v(1.14, -3.92) * mm, "end": v(1.13, -3.98) * mm});
            skLineSegment(sketch, "E1005", {"start": v(1.15, -3.86) * mm, "end": v(1.14, -3.92) * mm});
            skLineSegment(sketch, "E1006", {"start": v(1.16, -3.81) * mm, "end": v(1.15, -3.86) * mm});
            skLineSegment(sketch, "E1007", {"start": v(1.16, -3.76) * mm, "end": v(1.16, -3.81) * mm});
            skLineSegment(sketch, "E1008", {"start": v(1.16, -3.72) * mm, "end": v(1.16, -3.76) * mm});
            skLineSegment(sketch, "E1009", {"start": v(1.16, -3.68) * mm, "end": v(1.16, -3.72) * mm});
            skLineSegment(sketch, "E1010", {"start": v(1.16, -3.64) * mm, "end": v(1.16, -3.68) * mm});
            skLineSegment(sketch, "E1011", {"start": v(1.16, -3.6) * mm, "end": v(1.16, -3.64) * mm});
            skLineSegment(sketch, "E1012", {"start": v(1.15, -3.58) * mm, "end": v(1.16, -3.6) * mm});
            skLineSegment(sketch, "E1013", {"start": v(1.15, -3.56) * mm, "end": v(1.15, -3.58) * mm});
            skLineSegment(sketch, "E1014", {"start": v(1.15, -3.54) * mm, "end": v(1.15, -3.56) * mm});
            skLineSegment(sketch, "E1015", {"start": v(1.15, -3.53) * mm, "end": v(1.15, -3.54) * mm});
            skLineSegment(sketch, "E1016", {"start": v(1.14, -3.52) * mm, "end": v(1.15, -3.53) * mm});
            skLineSegment(sketch, "E1017", {"start": v(1.14, -3.52) * mm, "end": v(1.14, -3.52) * mm});
            skLineSegment(sketch, "E1018", {"start": v(0.99, -3.04) * mm, "end": v(1.14, -3.52) * mm});
            skLineSegment(sketch, "E1019", {"start": v(1.68, -2.72) * mm, "end": v(0.99, -3.04) * mm});
            skLineSegment(sketch, "E1020", {"start": v(1.94, -3.15) * mm, "end": v(1.68, -2.72) * mm});
            skLineSegment(sketch, "E1021", {"start": v(1.94, -3.15) * mm, "end": v(1.94, -3.15) * mm});
            skLineSegment(sketch, "E1022", {"start": v(1.95, -3.16) * mm, "end": v(1.94, -3.15) * mm});
            skLineSegment(sketch, "E1023", {"start": v(1.96, -3.17) * mm, "end": v(1.95, -3.16) * mm});
            skLineSegment(sketch, "E1024", {"start": v(1.97, -3.18) * mm, "end": v(1.96, -3.17) * mm});
            skLineSegment(sketch, "E1025", {"start": v(1.98, -3.2) * mm, "end": v(1.97, -3.18) * mm});
            skLineSegment(sketch, "E1026", {"start": v(2, -3.22) * mm, "end": v(1.98, -3.2) * mm});
            skLineSegment(sketch, "E1027", {"start": v(2.03, -3.24) * mm, "end": v(2, -3.22) * mm});
            skLineSegment(sketch, "E1028", {"start": v(2.05, -3.26) * mm, "end": v(2.03, -3.24) * mm});
            skLineSegment(sketch, "E1029", {"start": v(2.08, -3.29) * mm, "end": v(2.05, -3.26) * mm});
            skLineSegment(sketch, "E1030", {"start": v(2.12, -3.32) * mm, "end": v(2.08, -3.29) * mm});
            skLineSegment(sketch, "E1031", {"start": v(2.16, -3.35) * mm, "end": v(2.12, -3.32) * mm});
            skLineSegment(sketch, "E1032", {"start": v(2.2, -3.38) * mm, "end": v(2.16, -3.35) * mm});
            skLineSegment(sketch, "E1033", {"start": v(2.25, -3.4) * mm, "end": v(2.2, -3.38) * mm});
            skLineSegment(sketch, "E1034", {"start": v(2.3, -3.44) * mm, "end": v(2.25, -3.4) * mm});
            skLineSegment(sketch, "E1035", {"start": v(2.37, -3.47) * mm, "end": v(2.3, -3.44) * mm});
            skLineSegment(sketch, "E1036", {"start": v(2.43, -3.5) * mm, "end": v(2.37, -3.47) * mm});
            skLineSegment(sketch, "E1037", {"start": v(2.5, -3.54) * mm, "end": v(2.43, -3.5) * mm});
            skLineSegment(sketch, "E1038", {"start": v(2.58, -3.57) * mm, "end": v(2.5, -3.54) * mm});
            skLineSegment(sketch, "E1039", {"start": v(2.66, -3.6) * mm, "end": v(2.58, -3.57) * mm});
            skLineSegment(sketch, "E1040", {"start": v(2.74, -3.62) * mm, "end": v(2.66, -3.6) * mm});
            skLineSegment(sketch, "E1041", {"start": v(2.83, -3.65) * mm, "end": v(2.74, -3.62) * mm});
            skLineSegment(sketch, "E1042", {"start": v(2.93, -3.68) * mm, "end": v(2.83, -3.65) * mm});
            skLineSegment(sketch, "E1043", {"start": v(3.03, -3.7) * mm, "end": v(2.93, -3.68) * mm});
            skLineSegment(sketch, "E1044", {"start": v(3.14, -3.72) * mm, "end": v(3.03, -3.7) * mm});
            skLineSegment(sketch, "E1045", {"start": v(3.25, -3.73) * mm, "end": v(3.14, -3.72) * mm});
            skLineSegment(sketch, "E1046", {"start": v(3.33, -3.7) * mm, "end": v(3.25, -3.73) * mm});
            skLineSegment(sketch, "E1047", {"start": v(3.44, -3.6) * mm, "end": v(3.33, -3.7) * mm});
            skLineSegment(sketch, "E1048", {"start": v(3.48, -3.52) * mm, "end": v(3.44, -3.6) * mm});
            skLineSegment(sketch, "E1049", {"start": v(3.47, -3.4) * mm, "end": v(3.48, -3.52) * mm});
            skLineSegment(sketch, "E1050", {"start": v(3.46, -3.3) * mm, "end": v(3.47, -3.4) * mm});
            skLineSegment(sketch, "E1051", {"start": v(3.45, -3.2) * mm, "end": v(3.46, -3.3) * mm});
            skLineSegment(sketch, "E1052", {"start": v(3.43, -3.1) * mm, "end": v(3.45, -3.2) * mm});
            skLineSegment(sketch, "E1053", {"start": v(3.4, -3) * mm, "end": v(3.43, -3.1) * mm});
            skLineSegment(sketch, "E1054", {"start": v(3.39, -2.92) * mm, "end": v(3.4, -3) * mm});
            skLineSegment(sketch, "E1055", {"start": v(3.36, -2.84) * mm, "end": v(3.39, -2.92) * mm});
            skLineSegment(sketch, "E1056", {"start": v(3.34, -2.76) * mm, "end": v(3.36, -2.84) * mm});
            skLineSegment(sketch, "E1057", {"start": v(3.31, -2.69) * mm, "end": v(3.34, -2.76) * mm});
            skLineSegment(sketch, "E1058", {"start": v(3.28, -2.62) * mm, "end": v(3.31, -2.69) * mm});
            skLineSegment(sketch, "E1059", {"start": v(3.26, -2.56) * mm, "end": v(3.28, -2.62) * mm});
            skLineSegment(sketch, "E1060", {"start": v(3.23, -2.5) * mm, "end": v(3.26, -2.56) * mm});
            skLineSegment(sketch, "E1061", {"start": v(3.2, -2.45) * mm, "end": v(3.23, -2.5) * mm});
            skLineSegment(sketch, "E1062", {"start": v(3.18, -2.4) * mm, "end": v(3.2, -2.45) * mm});
            skLineSegment(sketch, "E1063", {"start": v(3.15, -2.36) * mm, "end": v(3.18, -2.4) * mm});
            skLineSegment(sketch, "E1064", {"start": v(3.12, -2.32) * mm, "end": v(3.15, -2.36) * mm});
            skLineSegment(sketch, "E1065", {"start": v(3.1, -2.3) * mm, "end": v(3.12, -2.32) * mm});
            skLineSegment(sketch, "E1066", {"start": v(3.08, -2.26) * mm, "end": v(3.1, -2.3) * mm});
            skLineSegment(sketch, "E1067", {"start": v(3.06, -2.24) * mm, "end": v(3.08, -2.26) * mm});
            skLineSegment(sketch, "E1068", {"start": v(3.04, -2.22) * mm, "end": v(3.06, -2.24) * mm});
            skLineSegment(sketch, "E1069", {"start": v(3.02, -2.2) * mm, "end": v(3.04, -2.22) * mm});
            skLineSegment(sketch, "E1070", {"start": v(3.01, -2.2) * mm, "end": v(3.02, -2.2) * mm});
            skLineSegment(sketch, "E1071", {"start": v(3, -2.18) * mm, "end": v(3.01, -2.2) * mm});
            skLineSegment(sketch, "E1072", {"start": v(3, -2.18) * mm, "end": v(3, -2.18) * mm});
            skLineSegment(sketch, "E1073", {"start": v(3, -2.17) * mm, "end": v(3, -2.18) * mm});
            skLineSegment(sketch, "E1074", {"start": v(2.58, -1.88) * mm, "end": v(3, -2.17) * mm});
            skLineSegment(sketch, "E1075", {"start": v(2.95, -1.21) * mm, "end": v(2.58, -1.88) * mm});
            skLineSegment(sketch, "E1076", {"start": v(3.42, -1.4) * mm, "end": v(2.95, -1.21) * mm});
            skLineSegment(sketch, "E1077", {"start": v(3.42, -1.4) * mm, "end": v(3.42, -1.4) * mm});
            skLineSegment(sketch, "E1078", {"start": v(3.43, -1.4) * mm, "end": v(3.42, -1.4) * mm});
            skLineSegment(sketch, "E1079", {"start": v(3.45, -1.41) * mm, "end": v(3.43, -1.4) * mm});
            skLineSegment(sketch, "E1080", {"start": v(3.46, -1.42) * mm, "end": v(3.45, -1.41) * mm});
            skLineSegment(sketch, "E1081", {"start": v(3.48, -1.42) * mm, "end": v(3.46, -1.42) * mm});
            skLineSegment(sketch, "E1082", {"start": v(3.51, -1.43) * mm, "end": v(3.48, -1.42) * mm});
            skLineSegment(sketch, "E1083", {"start": v(3.54, -1.43) * mm, "end": v(3.51, -1.43) * mm});
            skLineSegment(sketch, "E1084", {"start": v(3.58, -1.43) * mm, "end": v(3.54, -1.43) * mm});
            skLineSegment(sketch, "E1085", {"start": v(3.62, -1.44) * mm, "end": v(3.58, -1.43) * mm});
            skLineSegment(sketch, "E1086", {"start": v(3.66, -1.44) * mm, "end": v(3.62, -1.44) * mm});
            skLineSegment(sketch, "E1087", {"start": v(3.71, -1.44) * mm, "end": v(3.66, -1.44) * mm});
            skLineSegment(sketch, "E1088", {"start": v(3.77, -1.44) * mm, "end": v(3.71, -1.44) * mm});
            skLineSegment(sketch, "E1089", {"start": v(3.83, -1.43) * mm, "end": v(3.77, -1.44) * mm});
            skLineSegment(sketch, "E1090", {"start": v(3.89, -1.43) * mm, "end": v(3.83, -1.43) * mm});
            skLineSegment(sketch, "E1091", {"start": v(3.96, -1.42) * mm, "end": v(3.89, -1.43) * mm});
            skLineSegment(sketch, "E1092", {"start": v(4.03, -1.4) * mm, "end": v(3.96, -1.42) * mm});
            skLineSegment(sketch, "E1093", {"start": v(4.1, -1.4) * mm, "end": v(4.03, -1.4) * mm});
            skLineSegment(sketch, "E1094", {"start": v(4.18, -1.37) * mm, "end": v(4.1, -1.4) * mm});
            skLineSegment(sketch, "E1095", {"start": v(4.26, -1.35) * mm, "end": v(4.18, -1.37) * mm});
            skLineSegment(sketch, "E1096", {"start": v(4.35, -1.32) * mm, "end": v(4.26, -1.35) * mm});
            skLineSegment(sketch, "E1097", {"start": v(4.44, -1.29) * mm, "end": v(4.35, -1.32) * mm});
            skLineSegment(sketch, "E1098", {"start": v(4.53, -1.25) * mm, "end": v(4.44, -1.29) * mm});
            skLineSegment(sketch, "E1099", {"start": v(4.62, -1.21) * mm, "end": v(4.53, -1.25) * mm});
            skLineSegment(sketch, "E1100", {"start": v(4.72, -1.16) * mm, "end": v(4.62, -1.21) * mm});
            skLineSegment(sketch, "E1101", {"start": v(4.82, -1.11) * mm, "end": v(4.72, -1.16) * mm});
            skLineSegment(sketch, "E1102", {"start": v(4.87, -1.04) * mm, "end": v(4.82, -1.11) * mm});
            skLineSegment(sketch, "E1103", {"start": v(4.9, -0.88) * mm, "end": v(4.87, -1.04) * mm});
            skLineSegment(sketch, "E1104", {"start": v(4.88, -0.8) * mm, "end": v(4.9, -0.88) * mm});
            skLineSegment(sketch, "E1105", {"start": v(4.8, -0.72) * mm, "end": v(4.88, -0.8) * mm});
            skLineSegment(sketch, "E1106", {"start": v(4.74, -0.64) * mm, "end": v(4.8, -0.72) * mm});
            skLineSegment(sketch, "E1107", {"start": v(4.67, -0.56) * mm, "end": v(4.74, -0.64) * mm});
            skLineSegment(sketch, "E1108", {"start": v(4.6, -0.5) * mm, "end": v(4.67, -0.56) * mm});
            skLineSegment(sketch, "E1109", {"start": v(4.52, -0.43) * mm, "end": v(4.6, -0.5) * mm});
            skLineSegment(sketch, "E1110", {"start": v(4.46, -0.37) * mm, "end": v(4.52, -0.43) * mm});
            skLineSegment(sketch, "E1111", {"start": v(4.39, -0.32) * mm, "end": v(4.46, -0.37) * mm});
            skLineSegment(sketch, "E1112", {"start": v(4.32, -0.27) * mm, "end": v(4.39, -0.32) * mm});
            skLineSegment(sketch, "E1113", {"start": v(4.26, -0.23) * mm, "end": v(4.32, -0.27) * mm});
            skLineSegment(sketch, "E1114", {"start": v(4.2, -0.19) * mm, "end": v(4.26, -0.23) * mm});
            skLineSegment(sketch, "E1115", {"start": v(4.14, -0.16) * mm, "end": v(4.2, -0.19) * mm});
            skLineSegment(sketch, "E1116", {"start": v(4.08, -0.13) * mm, "end": v(4.14, -0.16) * mm});
            skLineSegment(sketch, "E1117", {"start": v(4.03, -0.1) * mm, "end": v(4.08, -0.13) * mm});
            skLineSegment(sketch, "E1118", {"start": v(3.98, -0.08) * mm, "end": v(4.03, -0.1) * mm});
            skLineSegment(sketch, "E1119", {"start": v(3.94, -0.06) * mm, "end": v(3.98, -0.08) * mm});
            skLineSegment(sketch, "E1120", {"start": v(3.9, -0.04) * mm, "end": v(3.94, -0.06) * mm});
            skLineSegment(sketch, "E1121", {"start": v(3.85, -0.03) * mm, "end": v(3.9, -0.04) * mm});
            skLineSegment(sketch, "E1122", {"start": v(3.82, -0.02) * mm, "end": v(3.85, -0.03) * mm});
            skLineSegment(sketch, "E1123", {"start": v(3.79, -0.01) * mm, "end": v(3.82, -0.02) * mm});
            skLineSegment(sketch, "E1124", {"start": v(3.76, 0) * mm, "end": v(3.79, -0.01) * mm});
            skLineSegment(sketch, "E1125", {"start": v(3.74, 0) * mm, "end": v(3.76, 0) * mm});
            skLineSegment(sketch, "E1126", {"start": v(3.72, 0) * mm, "end": v(3.74, 0) * mm});
            skLineSegment(sketch, "E1127", {"start": v(3.7, 0) * mm, "end": v(3.72, 0) * mm});
            skLineSegment(sketch, "E1128", {"start": v(3.7, 0) * mm, "end": v(3.7, 0) * mm});
            skLineSegment(sketch, "E1129", {"start": v(3.2, 0) * mm, "end": v(3.7, 0) * mm});
            skLineSegment(sketch, "E1130", {"start": v(3.1, 0.76) * mm, "end": v(3.2, 0) * mm});
            skSolve(sketch);
        }
        {
            var Q0;
            {var subQ0=sQuery(id+"F15.wireOp",EDGE,"E964");Q0=makeQuery(id+"F15.imprint","IMPRINT",FACE,{"disambiguationData":[TD([[makeQuery(id+"F15.imprint","IMPRINT",EDGE,{"derivedFrom":subQ0}),-1.0]])]});}
            var Q1;
            {var subQ0=sQuery(id+"F15.wireOp",EDGE,"E1020");Q1=makeQuery(id+"F15.imprint","IMPRINT",FACE,{"disambiguationData":[TD([[makeQuery(id+"F15.imprint","IMPRINT",EDGE,{"derivedFrom":subQ0}),-1.0]])]});}
            var Q2;
            {var subQ0=sQuery(id+"F15.wireOp",EDGE,"E1076");Q2=makeQuery(id+"F15.imprint","IMPRINT",FACE,{"disambiguationData":[TD([[makeQuery(id+"F15.imprint","IMPRINT",EDGE,{"derivedFrom":subQ0}),-1.0]])]});}
            var Q3;
            {var subQ0=sQuery(id+"F15.wireOp",EDGE,"E573");Q3=makeQuery(id+"F15.imprint","IMPRINT",FACE,{"disambiguationData":[TD([[makeQuery(id+"F15.imprint","IMPRINT",EDGE,{"derivedFrom":subQ0}),-1.0]])]});}
            var Q4;
            {var subQ0=sQuery(id+"F15.wireOp",EDGE,"E629");Q4=makeQuery(id+"F15.imprint","IMPRINT",FACE,{"disambiguationData":[TD([[makeQuery(id+"F15.imprint","IMPRINT",EDGE,{"derivedFrom":subQ0}),-1.0]])]});}
            var Q5;
            {var subQ0=sQuery(id+"F15.wireOp",EDGE,"E741");Q5=makeQuery(id+"F15.imprint","IMPRINT",FACE,{"disambiguationData":[TD([[makeQuery(id+"F15.imprint","IMPRINT",EDGE,{"derivedFrom":subQ0}),-1.0]])]});}
            var Q6;
            {var subQ0=sQuery(id+"F15.wireOp",EDGE,"E797");Q6=makeQuery(id+"F15.imprint","IMPRINT",FACE,{"disambiguationData":[TD([[makeQuery(id+"F15.imprint","IMPRINT",EDGE,{"derivedFrom":subQ0}),-1.0]])]});}
            var Q7;
            {var subQ0=sQuery(id+"F15.wireOp",EDGE,"E685");Q7=makeQuery(id+"F15.imprint","IMPRINT",FACE,{"disambiguationData":[TD([[makeQuery(id+"F15.imprint","IMPRINT",EDGE,{"derivedFrom":subQ0}),-1.0]])]});}
            var Q8;
            {var subQ0=sQuery(id+"F15.wireOp",EDGE,"E852");Q8=makeQuery(id+"F15.imprint","IMPRINT",FACE,{"disambiguationData":[TD([[makeQuery(id+"F15.imprint","IMPRINT",EDGE,{"derivedFrom":subQ0}),-1.0]])]});}
            var Q9;
            {var subQ0=sQuery(id+"F15.wireOp",EDGE,"E908");Q9=makeQuery(id+"F15.imprint","IMPRINT",FACE,{"disambiguationData":[TD([[makeQuery(id+"F15.imprint","IMPRINT",EDGE,{"derivedFrom":subQ0}),-1.0]])]});}
            var Q10;
            {var subQ3=sQuery(id+"F15.wireOp",EDGE,"E628");Q10=makeQuery(id+"F15.imprint","IMPRINT",FACE,{"disambiguationData":[TD([[makeQuery(id+"F15.imprint","IMPRINT",EDGE,{"derivedFrom":subQ3}),-1.0]])]});}
            extrude(context, id + "F16", {"entities" : qUnion([Q0, Q1, Q2, Q3, Q4, Q5, Q6, Q7, Q8, Q9, Q10]), "depth" : 2 * mm, "offsetDistance" : 25 * mm, "hasSecondDirection" : true, "secondDirectionOppositeDirection" : true, "secondDirectionDepth" : 1 * mm});
        }
        {
            var Q0;
            Q0=makeQuery(id+"F16.opExtrude","SWEPT_BODY",BODY,{"disambiguationData":[OSD([sQuery(id+"F0.wireOp",EDGE,"E0"),sQuery(id+"F13.wireOp",EDGE,"E572"),sQuery(id+"F15.wireOp",EDGE,"E573"),sQuery(id+"F15.wireOp",EDGE,"E574"),sQuery(id+"F15.wireOp",EDGE,"E575"),sQuery(id+"F15.wireOp",EDGE,"E576"),sQuery(id+"F15.wireOp",EDGE,"E577"),sQuery(id+"F15.wireOp",EDGE,"E578"),sQuery(id+"F15.wireOp",EDGE,"E579"),sQuery(id+"F15.wireOp",EDGE,"E580"),sQuery(id+"F15.wireOp",EDGE,"E581"),sQuery(id+"F15.wireOp",EDGE,"E582"),sQuery(id+"F15.wireOp",EDGE,"E583"),sQuery(id+"F15.wireOp",EDGE,"E584"),sQuery(id+"F15.wireOp",EDGE,"E585"),sQuery(id+"F15.wireOp",EDGE,"E586"),sQuery(id+"F15.wireOp",EDGE,"E587"),sQuery(id+"F15.wireOp",EDGE,"E588"),sQuery(id+"F15.wireOp",EDGE,"E589"),sQuery(id+"F15.wireOp",EDGE,"E590"),sQuery(id+"F15.wireOp",EDGE,"E591"),sQuery(id+"F15.wireOp",EDGE,"E592"),sQuery(id+"F15.wireOp",EDGE,"E593"),sQuery(id+"F15.wireOp",EDGE,"E594"),sQuery(id+"F15.wireOp",EDGE,"E595"),sQuery(id+"F15.wireOp",EDGE,"E596"),sQuery(id+"F15.wireOp",EDGE,"E597"),sQuery(id+"F15.wireOp",EDGE,"E598"),sQuery(id+"F15.wireOp",EDGE,"E599"),sQuery(id+"F15.wireOp",EDGE,"E600"),sQuery(id+"F15.wireOp",EDGE,"E601"),sQuery(id+"F15.wireOp",EDGE,"E602"),sQuery(id+"F15.wireOp",EDGE,"E603"),sQuery(id+"F15.wireOp",EDGE,"E604"),sQuery(id+"F15.wireOp",EDGE,"E605"),sQuery(id+"F15.wireOp",EDGE,"E606"),sQuery(id+"F15.wireOp",EDGE,"E607"),sQuery(id+"F15.wireOp",EDGE,"E608"),sQuery(id+"F15.wireOp",EDGE,"E609"),sQuery(id+"F15.wireOp",EDGE,"E610"),sQuery(id+"F15.wireOp",EDGE,"E611"),sQuery(id+"F15.wireOp",EDGE,"E612"),sQuery(id+"F15.wireOp",EDGE,"E613"),sQuery(id+"F15.wireOp",EDGE,"E614"),sQuery(id+"F15.wireOp",EDGE,"E615"),sQuery(id+"F15.wireOp",EDGE,"E616"),sQuery(id+"F15.wireOp",EDGE,"E617"),sQuery(id+"F15.wireOp",EDGE,"E618"),sQuery(id+"F15.wireOp",EDGE,"E619"),sQuery(id+"F15.wireOp",EDGE,"E620"),sQuery(id+"F15.wireOp",EDGE,"E621"),sQuery(id+"F15.wireOp",EDGE,"E622"),sQuery(id+"F15.wireOp",EDGE,"E623"),sQuery(id+"F15.wireOp",EDGE,"E624"),sQuery(id+"F15.wireOp",EDGE,"E625"),sQuery(id+"F15.wireOp",EDGE,"E626"),sQuery(id+"F15.wireOp",EDGE,"E627"),sQuery(id+"F15.wireOp",EDGE,"E628"),sQuery(id+"F15.wireOp",EDGE,"E629"),sQuery(id+"F15.wireOp",EDGE,"E630"),sQuery(id+"F15.wireOp",EDGE,"E631"),sQuery(id+"F15.wireOp",EDGE,"E632"),sQuery(id+"F15.wireOp",EDGE,"E633"),sQuery(id+"F15.wireOp",EDGE,"E634"),sQuery(id+"F15.wireOp",EDGE,"E635"),sQuery(id+"F15.wireOp",EDGE,"E636"),sQuery(id+"F15.wireOp",EDGE,"E637"),sQuery(id+"F15.wireOp",EDGE,"E638"),sQuery(id+"F15.wireOp",EDGE,"E639"),sQuery(id+"F15.wireOp",EDGE,"E640"),sQuery(id+"F15.wireOp",EDGE,"E641"),sQuery(id+"F15.wireOp",EDGE,"E642"),sQuery(id+"F15.wireOp",EDGE,"E643"),sQuery(id+"F15.wireOp",EDGE,"E644"),sQuery(id+"F15.wireOp",EDGE,"E645"),sQuery(id+"F15.wireOp",EDGE,"E646"),sQuery(id+"F15.wireOp",EDGE,"E647"),sQuery(id+"F15.wireOp",EDGE,"E648"),sQuery(id+"F15.wireOp",EDGE,"E649"),sQuery(id+"F15.wireOp",EDGE,"E650"),sQuery(id+"F15.wireOp",EDGE,"E651"),sQuery(id+"F15.wireOp",EDGE,"E652"),sQuery(id+"F15.wireOp",EDGE,"E653"),sQuery(id+"F15.wireOp",EDGE,"E654"),sQuery(id+"F15.wireOp",EDGE,"E655"),sQuery(id+"F15.wireOp",EDGE,"E656"),sQuery(id+"F15.wireOp",EDGE,"E657"),sQuery(id+"F15.wireOp",EDGE,"E658"),sQuery(id+"F15.wireOp",EDGE,"E659"),sQuery(id+"F15.wireOp",EDGE,"E660"),sQuery(id+"F15.wireOp",EDGE,"E661"),sQuery(id+"F15.wireOp",EDGE,"E662"),sQuery(id+"F15.wireOp",EDGE,"E663"),sQuery(id+"F15.wireOp",EDGE,"E664"),sQuery(id+"F15.wireOp",EDGE,"E665"),sQuery(id+"F15.wireOp",EDGE,"E666"),sQuery(id+"F15.wireOp",EDGE,"E667"),sQuery(id+"F15.wireOp",EDGE,"E668"),sQuery(id+"F15.wireOp",EDGE,"E669"),sQuery(id+"F15.wireOp",EDGE,"E670"),sQuery(id+"F15.wireOp",EDGE,"E671"),sQuery(id+"F15.wireOp",EDGE,"E672"),sQuery(id+"F15.wireOp",EDGE,"E673"),sQuery(id+"F15.wireOp",EDGE,"E674"),sQuery(id+"F15.wireOp",EDGE,"E675"),sQuery(id+"F15.wireOp",EDGE,"E676"),sQuery(id+"F15.wireOp",EDGE,"E677"),sQuery(id+"F15.wireOp",EDGE,"E678"),sQuery(id+"F15.wireOp",EDGE,"E679"),sQuery(id+"F15.wireOp",EDGE,"E680"),sQuery(id+"F15.wireOp",EDGE,"E681"),sQuery(id+"F15.wireOp",EDGE,"E682"),sQuery(id+"F15.wireOp",EDGE,"E683"),sQuery(id+"F15.wireOp",EDGE,"E684"),sQuery(id+"F15.wireOp",EDGE,"E685"),sQuery(id+"F15.wireOp",EDGE,"E686"),sQuery(id+"F15.wireOp",EDGE,"E687"),sQuery(id+"F15.wireOp",EDGE,"E688"),sQuery(id+"F15.wireOp",EDGE,"E689"),sQuery(id+"F15.wireOp",EDGE,"E690"),sQuery(id+"F15.wireOp",EDGE,"E691"),sQuery(id+"F15.wireOp",EDGE,"E692"),sQuery(id+"F15.wireOp",EDGE,"E693"),sQuery(id+"F15.wireOp",EDGE,"E694"),sQuery(id+"F15.wireOp",EDGE,"E695"),sQuery(id+"F15.wireOp",EDGE,"E696"),sQuery(id+"F15.wireOp",EDGE,"E697"),sQuery(id+"F15.wireOp",EDGE,"E698"),sQuery(id+"F15.wireOp",EDGE,"E699"),sQuery(id+"F15.wireOp",EDGE,"E700"),sQuery(id+"F15.wireOp",EDGE,"E701"),sQuery(id+"F15.wireOp",EDGE,"E702"),sQuery(id+"F15.wireOp",EDGE,"E703"),sQuery(id+"F15.wireOp",EDGE,"E704"),sQuery(id+"F15.wireOp",EDGE,"E705"),sQuery(id+"F15.wireOp",EDGE,"E706"),sQuery(id+"F15.wireOp",EDGE,"E707"),sQuery(id+"F15.wireOp",EDGE,"E708"),sQuery(id+"F15.wireOp",EDGE,"E709"),sQuery(id+"F15.wireOp",EDGE,"E710"),sQuery(id+"F15.wireOp",EDGE,"E711"),sQuery(id+"F15.wireOp",EDGE,"E712"),sQuery(id+"F15.wireOp",EDGE,"E713"),sQuery(id+"F15.wireOp",EDGE,"E714"),sQuery(id+"F15.wireOp",EDGE,"E715"),sQuery(id+"F15.wireOp",EDGE,"E716"),sQuery(id+"F15.wireOp",EDGE,"E717"),sQuery(id+"F15.wireOp",EDGE,"E718"),sQuery(id+"F15.wireOp",EDGE,"E719"),sQuery(id+"F15.wireOp",EDGE,"E720"),sQuery(id+"F15.wireOp",EDGE,"E721"),sQuery(id+"F15.wireOp",EDGE,"E722"),sQuery(id+"F15.wireOp",EDGE,"E723"),sQuery(id+"F15.wireOp",EDGE,"E724"),sQuery(id+"F15.wireOp",EDGE,"E725"),sQuery(id+"F15.wireOp",EDGE,"E726"),sQuery(id+"F15.wireOp",EDGE,"E727"),sQuery(id+"F15.wireOp",EDGE,"E728"),sQuery(id+"F15.wireOp",EDGE,"E729"),sQuery(id+"F15.wireOp",EDGE,"E730"),sQuery(id+"F15.wireOp",EDGE,"E731"),sQuery(id+"F15.wireOp",EDGE,"E732"),sQuery(id+"F15.wireOp",EDGE,"E733"),sQuery(id+"F15.wireOp",EDGE,"E734"),sQuery(id+"F15.wireOp",EDGE,"E735"),sQuery(id+"F15.wireOp",EDGE,"E736"),sQuery(id+"F15.wireOp",EDGE,"E737"),sQuery(id+"F15.wireOp",EDGE,"E738"),sQuery(id+"F15.wireOp",EDGE,"E739"),sQuery(id+"F15.wireOp",EDGE,"E740"),sQuery(id+"F15.wireOp",EDGE,"E741"),sQuery(id+"F15.wireOp",EDGE,"E742"),sQuery(id+"F15.wireOp",EDGE,"E743"),sQuery(id+"F15.wireOp",EDGE,"E744"),sQuery(id+"F15.wireOp",EDGE,"E745"),sQuery(id+"F15.wireOp",EDGE,"E746"),sQuery(id+"F15.wireOp",EDGE,"E747"),sQuery(id+"F15.wireOp",EDGE,"E748"),sQuery(id+"F15.wireOp",EDGE,"E749"),sQuery(id+"F15.wireOp",EDGE,"E750"),sQuery(id+"F15.wireOp",EDGE,"E751"),sQuery(id+"F15.wireOp",EDGE,"E752"),sQuery(id+"F15.wireOp",EDGE,"E753"),sQuery(id+"F15.wireOp",EDGE,"E754"),sQuery(id+"F15.wireOp",EDGE,"E755"),sQuery(id+"F15.wireOp",EDGE,"E756"),sQuery(id+"F15.wireOp",EDGE,"E757"),sQuery(id+"F15.wireOp",EDGE,"E758"),sQuery(id+"F15.wireOp",EDGE,"E759"),sQuery(id+"F15.wireOp",EDGE,"E760"),sQuery(id+"F15.wireOp",EDGE,"E761"),sQuery(id+"F15.wireOp",EDGE,"E762"),sQuery(id+"F15.wireOp",EDGE,"E763"),sQuery(id+"F15.wireOp",EDGE,"E764"),sQuery(id+"F15.wireOp",EDGE,"E765"),sQuery(id+"F15.wireOp",EDGE,"E766"),sQuery(id+"F15.wireOp",EDGE,"E767"),sQuery(id+"F15.wireOp",EDGE,"E768"),sQuery(id+"F15.wireOp",EDGE,"E769"),sQuery(id+"F15.wireOp",EDGE,"E770"),sQuery(id+"F15.wireOp",EDGE,"E771"),sQuery(id+"F15.wireOp",EDGE,"E772"),sQuery(id+"F15.wireOp",EDGE,"E773"),sQuery(id+"F15.wireOp",EDGE,"E774"),sQuery(id+"F15.wireOp",EDGE,"E775"),sQuery(id+"F15.wireOp",EDGE,"E776"),sQuery(id+"F15.wireOp",EDGE,"E777"),sQuery(id+"F15.wireOp",EDGE,"E778"),sQuery(id+"F15.wireOp",EDGE,"E779"),sQuery(id+"F15.wireOp",EDGE,"E780"),sQuery(id+"F15.wireOp",EDGE,"E781"),sQuery(id+"F15.wireOp",EDGE,"E782"),sQuery(id+"F15.wireOp",EDGE,"E783"),sQuery(id+"F15.wireOp",EDGE,"E784"),sQuery(id+"F15.wireOp",EDGE,"E785"),sQuery(id+"F15.wireOp",EDGE,"E786"),sQuery(id+"F15.wireOp",EDGE,"E787"),sQuery(id+"F15.wireOp",EDGE,"E788"),sQuery(id+"F15.wireOp",EDGE,"E789"),sQuery(id+"F15.wireOp",EDGE,"E790"),sQuery(id+"F15.wireOp",EDGE,"E791"),sQuery(id+"F15.wireOp",EDGE,"E792"),sQuery(id+"F15.wireOp",EDGE,"E793"),sQuery(id+"F15.wireOp",EDGE,"E794"),sQuery(id+"F15.wireOp",EDGE,"E795"),sQuery(id+"F15.wireOp",EDGE,"E796"),sQuery(id+"F15.wireOp",EDGE,"E797"),sQuery(id+"F15.wireOp",EDGE,"E798"),sQuery(id+"F15.wireOp",EDGE,"E799"),sQuery(id+"F15.wireOp",EDGE,"E800"),sQuery(id+"F15.wireOp",EDGE,"E801"),sQuery(id+"F15.wireOp",EDGE,"E802"),sQuery(id+"F15.wireOp",EDGE,"E803"),sQuery(id+"F15.wireOp",EDGE,"E804"),sQuery(id+"F15.wireOp",EDGE,"E805"),sQuery(id+"F15.wireOp",EDGE,"E806"),sQuery(id+"F15.wireOp",EDGE,"E807"),sQuery(id+"F15.wireOp",EDGE,"E808"),sQuery(id+"F15.wireOp",EDGE,"E809"),sQuery(id+"F15.wireOp",EDGE,"E810"),sQuery(id+"F15.wireOp",EDGE,"E811"),sQuery(id+"F15.wireOp",EDGE,"E812"),sQuery(id+"F15.wireOp",EDGE,"E813"),sQuery(id+"F15.wireOp",EDGE,"E814"),sQuery(id+"F15.wireOp",EDGE,"E815"),sQuery(id+"F15.wireOp",EDGE,"E816"),sQuery(id+"F15.wireOp",EDGE,"E817"),sQuery(id+"F15.wireOp",EDGE,"E818"),sQuery(id+"F15.wireOp",EDGE,"E819"),sQuery(id+"F15.wireOp",EDGE,"E820"),sQuery(id+"F15.wireOp",EDGE,"E821"),sQuery(id+"F15.wireOp",EDGE,"E822"),sQuery(id+"F15.wireOp",EDGE,"E823"),sQuery(id+"F15.wireOp",EDGE,"E824"),sQuery(id+"F15.wireOp",EDGE,"E825"),sQuery(id+"F15.wireOp",EDGE,"E826"),sQuery(id+"F15.wireOp",EDGE,"E827"),sQuery(id+"F15.wireOp",EDGE,"E828"),sQuery(id+"F15.wireOp",EDGE,"E829"),sQuery(id+"F15.wireOp",EDGE,"E830"),sQuery(id+"F15.wireOp",EDGE,"E831"),sQuery(id+"F15.wireOp",EDGE,"E832"),sQuery(id+"F15.wireOp",EDGE,"E833"),sQuery(id+"F15.wireOp",EDGE,"E834"),sQuery(id+"F15.wireOp",EDGE,"E835"),sQuery(id+"F15.wireOp",EDGE,"E836"),sQuery(id+"F15.wireOp",EDGE,"E837"),sQuery(id+"F15.wireOp",EDGE,"E838"),sQuery(id+"F15.wireOp",EDGE,"E839"),sQuery(id+"F15.wireOp",EDGE,"E840"),sQuery(id+"F15.wireOp",EDGE,"E841"),sQuery(id+"F15.wireOp",EDGE,"E842"),sQuery(id+"F15.wireOp",EDGE,"E843"),sQuery(id+"F15.wireOp",EDGE,"E844"),sQuery(id+"F15.wireOp",EDGE,"E845"),sQuery(id+"F15.wireOp",EDGE,"E846"),sQuery(id+"F15.wireOp",EDGE,"E847"),sQuery(id+"F15.wireOp",EDGE,"E848"),sQuery(id+"F15.wireOp",EDGE,"E849"),sQuery(id+"F15.wireOp",EDGE,"E849"),sQuery(id+"F15.wireOp",EDGE,"E850"),sQuery(id+"F15.wireOp",EDGE,"E851"),sQuery(id+"F15.wireOp",EDGE,"E852"),sQuery(id+"F15.wireOp",EDGE,"E853"),sQuery(id+"F15.wireOp",EDGE,"E854"),sQuery(id+"F15.wireOp",EDGE,"E855"),sQuery(id+"F15.wireOp",EDGE,"E856"),sQuery(id+"F15.wireOp",EDGE,"E857"),sQuery(id+"F15.wireOp",EDGE,"E858"),sQuery(id+"F15.wireOp",EDGE,"E859"),sQuery(id+"F15.wireOp",EDGE,"E860"),sQuery(id+"F15.wireOp",EDGE,"E861"),sQuery(id+"F15.wireOp",EDGE,"E862"),sQuery(id+"F15.wireOp",EDGE,"E863"),sQuery(id+"F15.wireOp",EDGE,"E864"),sQuery(id+"F15.wireOp",EDGE,"E865"),sQuery(id+"F15.wireOp",EDGE,"E866"),sQuery(id+"F15.wireOp",EDGE,"E867"),sQuery(id+"F15.wireOp",EDGE,"E868"),sQuery(id+"F15.wireOp",EDGE,"E869"),sQuery(id+"F15.wireOp",EDGE,"E870"),sQuery(id+"F15.wireOp",EDGE,"E871"),sQuery(id+"F15.wireOp",EDGE,"E872"),sQuery(id+"F15.wireOp",EDGE,"E873"),sQuery(id+"F15.wireOp",EDGE,"E874"),sQuery(id+"F15.wireOp",EDGE,"E875"),sQuery(id+"F15.wireOp",EDGE,"E876"),sQuery(id+"F15.wireOp",EDGE,"E877"),sQuery(id+"F15.wireOp",EDGE,"E878"),sQuery(id+"F15.wireOp",EDGE,"E879"),sQuery(id+"F15.wireOp",EDGE,"E880"),sQuery(id+"F15.wireOp",EDGE,"E881"),sQuery(id+"F15.wireOp",EDGE,"E882"),sQuery(id+"F15.wireOp",EDGE,"E883"),sQuery(id+"F15.wireOp",EDGE,"E884"),sQuery(id+"F15.wireOp",EDGE,"E885"),sQuery(id+"F15.wireOp",EDGE,"E886"),sQuery(id+"F15.wireOp",EDGE,"E887"),sQuery(id+"F15.wireOp",EDGE,"E888"),sQuery(id+"F15.wireOp",EDGE,"E889"),sQuery(id+"F15.wireOp",EDGE,"E890"),sQuery(id+"F15.wireOp",EDGE,"E891"),sQuery(id+"F15.wireOp",EDGE,"E892"),sQuery(id+"F15.wireOp",EDGE,"E893"),sQuery(id+"F15.wireOp",EDGE,"E894"),sQuery(id+"F15.wireOp",EDGE,"E895"),sQuery(id+"F15.wireOp",EDGE,"E896"),sQuery(id+"F15.wireOp",EDGE,"E897"),sQuery(id+"F15.wireOp",EDGE,"E898"),sQuery(id+"F15.wireOp",EDGE,"E899"),sQuery(id+"F15.wireOp",EDGE,"E900"),sQuery(id+"F15.wireOp",EDGE,"E901"),sQuery(id+"F15.wireOp",EDGE,"E902"),sQuery(id+"F15.wireOp",EDGE,"E903"),sQuery(id+"F15.wireOp",EDGE,"E904"),sQuery(id+"F15.wireOp",EDGE,"E905"),sQuery(id+"F15.wireOp",EDGE,"E906"),sQuery(id+"F15.wireOp",EDGE,"E907"),sQuery(id+"F15.wireOp",EDGE,"E908"),sQuery(id+"F15.wireOp",EDGE,"E909"),sQuery(id+"F15.wireOp",EDGE,"E910"),sQuery(id+"F15.wireOp",EDGE,"E911"),sQuery(id+"F15.wireOp",EDGE,"E912"),sQuery(id+"F15.wireOp",EDGE,"E913"),sQuery(id+"F15.wireOp",EDGE,"E914"),sQuery(id+"F15.wireOp",EDGE,"E915"),sQuery(id+"F15.wireOp",EDGE,"E916"),sQuery(id+"F15.wireOp",EDGE,"E917"),sQuery(id+"F15.wireOp",EDGE,"E918"),sQuery(id+"F15.wireOp",EDGE,"E919"),sQuery(id+"F15.wireOp",EDGE,"E920"),sQuery(id+"F15.wireOp",EDGE,"E921"),sQuery(id+"F15.wireOp",EDGE,"E922"),sQuery(id+"F15.wireOp",EDGE,"E923"),sQuery(id+"F15.wireOp",EDGE,"E924"),sQuery(id+"F15.wireOp",EDGE,"E925"),sQuery(id+"F15.wireOp",EDGE,"E926"),sQuery(id+"F15.wireOp",EDGE,"E927"),sQuery(id+"F15.wireOp",EDGE,"E928"),sQuery(id+"F15.wireOp",EDGE,"E929"),sQuery(id+"F15.wireOp",EDGE,"E930"),sQuery(id+"F15.wireOp",EDGE,"E931"),sQuery(id+"F15.wireOp",EDGE,"E932"),sQuery(id+"F15.wireOp",EDGE,"E933"),sQuery(id+"F15.wireOp",EDGE,"E934"),sQuery(id+"F15.wireOp",EDGE,"E935"),sQuery(id+"F15.wireOp",EDGE,"E936"),sQuery(id+"F15.wireOp",EDGE,"E937"),sQuery(id+"F15.wireOp",EDGE,"E938"),sQuery(id+"F15.wireOp",EDGE,"E939"),sQuery(id+"F15.wireOp",EDGE,"E940"),sQuery(id+"F15.wireOp",EDGE,"E941"),sQuery(id+"F15.wireOp",EDGE,"E942"),sQuery(id+"F15.wireOp",EDGE,"E943"),sQuery(id+"F15.wireOp",EDGE,"E944"),sQuery(id+"F15.wireOp",EDGE,"E945"),sQuery(id+"F15.wireOp",EDGE,"E946"),sQuery(id+"F15.wireOp",EDGE,"E947"),sQuery(id+"F15.wireOp",EDGE,"E948"),sQuery(id+"F15.wireOp",EDGE,"E949"),sQuery(id+"F15.wireOp",EDGE,"E950"),sQuery(id+"F15.wireOp",EDGE,"E951"),sQuery(id+"F15.wireOp",EDGE,"E952"),sQuery(id+"F15.wireOp",EDGE,"E953"),sQuery(id+"F15.wireOp",EDGE,"E954"),sQuery(id+"F15.wireOp",EDGE,"E955"),sQuery(id+"F15.wireOp",EDGE,"E956"),sQuery(id+"F15.wireOp",EDGE,"E957"),sQuery(id+"F15.wireOp",EDGE,"E958"),sQuery(id+"F15.wireOp",EDGE,"E959"),sQuery(id+"F15.wireOp",EDGE,"E960"),sQuery(id+"F15.wireOp",EDGE,"E961"),sQuery(id+"F15.wireOp",EDGE,"E962"),sQuery(id+"F15.wireOp",EDGE,"E963"),sQuery(id+"F15.wireOp",EDGE,"E964"),sQuery(id+"F15.wireOp",EDGE,"E965"),sQuery(id+"F15.wireOp",EDGE,"E966"),sQuery(id+"F15.wireOp",EDGE,"E967"),sQuery(id+"F15.wireOp",EDGE,"E968"),sQuery(id+"F15.wireOp",EDGE,"E969"),sQuery(id+"F15.wireOp",EDGE,"E970"),sQuery(id+"F15.wireOp",EDGE,"E971"),sQuery(id+"F15.wireOp",EDGE,"E972"),sQuery(id+"F15.wireOp",EDGE,"E973"),sQuery(id+"F15.wireOp",EDGE,"E974"),sQuery(id+"F15.wireOp",EDGE,"E975"),sQuery(id+"F15.wireOp",EDGE,"E976"),sQuery(id+"F15.wireOp",EDGE,"E977"),sQuery(id+"F15.wireOp",EDGE,"E978"),sQuery(id+"F15.wireOp",EDGE,"E979"),sQuery(id+"F15.wireOp",EDGE,"E980"),sQuery(id+"F15.wireOp",EDGE,"E981"),sQuery(id+"F15.wireOp",EDGE,"E982"),sQuery(id+"F15.wireOp",EDGE,"E983"),sQuery(id+"F15.wireOp",EDGE,"E984"),sQuery(id+"F15.wireOp",EDGE,"E985"),sQuery(id+"F15.wireOp",EDGE,"E986"),sQuery(id+"F15.wireOp",EDGE,"E987"),sQuery(id+"F15.wireOp",EDGE,"E988"),sQuery(id+"F15.wireOp",EDGE,"E989"),sQuery(id+"F15.wireOp",EDGE,"E990"),sQuery(id+"F15.wireOp",EDGE,"E991"),sQuery(id+"F15.wireOp",EDGE,"E992"),sQuery(id+"F15.wireOp",EDGE,"E993"),sQuery(id+"F15.wireOp",EDGE,"E994"),sQuery(id+"F15.wireOp",EDGE,"E995"),sQuery(id+"F15.wireOp",EDGE,"E996"),sQuery(id+"F15.wireOp",EDGE,"E997"),sQuery(id+"F15.wireOp",EDGE,"E998"),sQuery(id+"F15.wireOp",EDGE,"E999"),sQuery(id+"F15.wireOp",EDGE,"E1000"),sQuery(id+"F15.wireOp",EDGE,"E1001"),sQuery(id+"F15.wireOp",EDGE,"E1002"),sQuery(id+"F15.wireOp",EDGE,"E1003"),sQuery(id+"F15.wireOp",EDGE,"E1004"),sQuery(id+"F15.wireOp",EDGE,"E1005"),sQuery(id+"F15.wireOp",EDGE,"E1006"),sQuery(id+"F15.wireOp",EDGE,"E1007"),sQuery(id+"F15.wireOp",EDGE,"E1008"),sQuery(id+"F15.wireOp",EDGE,"E1009"),sQuery(id+"F15.wireOp",EDGE,"E1010"),sQuery(id+"F15.wireOp",EDGE,"E1011"),sQuery(id+"F15.wireOp",EDGE,"E1012"),sQuery(id+"F15.wireOp",EDGE,"E1013"),sQuery(id+"F15.wireOp",EDGE,"E1014"),sQuery(id+"F15.wireOp",EDGE,"E1015"),sQuery(id+"F15.wireOp",EDGE,"E1016"),sQuery(id+"F15.wireOp",EDGE,"E1017"),sQuery(id+"F15.wireOp",EDGE,"E1018"),sQuery(id+"F15.wireOp",EDGE,"E1019"),sQuery(id+"F15.wireOp",EDGE,"E1020"),sQuery(id+"F15.wireOp",EDGE,"E1021"),sQuery(id+"F15.wireOp",EDGE,"E1022"),sQuery(id+"F15.wireOp",EDGE,"E1023"),sQuery(id+"F15.wireOp",EDGE,"E1024"),sQuery(id+"F15.wireOp",EDGE,"E1025"),sQuery(id+"F15.wireOp",EDGE,"E1026"),sQuery(id+"F15.wireOp",EDGE,"E1027"),sQuery(id+"F15.wireOp",EDGE,"E1028"),sQuery(id+"F15.wireOp",EDGE,"E1029"),sQuery(id+"F15.wireOp",EDGE,"E1030"),sQuery(id+"F15.wireOp",EDGE,"E1031"),sQuery(id+"F15.wireOp",EDGE,"E1032"),sQuery(id+"F15.wireOp",EDGE,"E1033"),sQuery(id+"F15.wireOp",EDGE,"E1034"),sQuery(id+"F15.wireOp",EDGE,"E1035"),sQuery(id+"F15.wireOp",EDGE,"E1036"),sQuery(id+"F15.wireOp",EDGE,"E1037"),sQuery(id+"F15.wireOp",EDGE,"E1038"),sQuery(id+"F15.wireOp",EDGE,"E1039"),sQuery(id+"F15.wireOp",EDGE,"E1040"),sQuery(id+"F15.wireOp",EDGE,"E1041"),sQuery(id+"F15.wireOp",EDGE,"E1042"),sQuery(id+"F15.wireOp",EDGE,"E1043"),sQuery(id+"F15.wireOp",EDGE,"E1044"),sQuery(id+"F15.wireOp",EDGE,"E1045"),sQuery(id+"F15.wireOp",EDGE,"E1046"),sQuery(id+"F15.wireOp",EDGE,"E1047"),sQuery(id+"F15.wireOp",EDGE,"E1048"),sQuery(id+"F15.wireOp",EDGE,"E1049"),sQuery(id+"F15.wireOp",EDGE,"E1050"),sQuery(id+"F15.wireOp",EDGE,"E1051"),sQuery(id+"F15.wireOp",EDGE,"E1052"),sQuery(id+"F15.wireOp",EDGE,"E1053"),sQuery(id+"F15.wireOp",EDGE,"E1054"),sQuery(id+"F15.wireOp",EDGE,"E1055"),sQuery(id+"F15.wireOp",EDGE,"E1056"),sQuery(id+"F15.wireOp",EDGE,"E1057"),sQuery(id+"F15.wireOp",EDGE,"E1058"),sQuery(id+"F15.wireOp",EDGE,"E1059"),sQuery(id+"F15.wireOp",EDGE,"E1060"),sQuery(id+"F15.wireOp",EDGE,"E1061"),sQuery(id+"F15.wireOp",EDGE,"E1062"),sQuery(id+"F15.wireOp",EDGE,"E1063"),sQuery(id+"F15.wireOp",EDGE,"E1064"),sQuery(id+"F15.wireOp",EDGE,"E1065"),sQuery(id+"F15.wireOp",EDGE,"E1066"),sQuery(id+"F15.wireOp",EDGE,"E1067"),sQuery(id+"F15.wireOp",EDGE,"E1068"),sQuery(id+"F15.wireOp",EDGE,"E1069"),sQuery(id+"F15.wireOp",EDGE,"E1070"),sQuery(id+"F15.wireOp",EDGE,"E1071"),sQuery(id+"F15.wireOp",EDGE,"E1072"),sQuery(id+"F15.wireOp",EDGE,"E1073"),sQuery(id+"F15.wireOp",EDGE,"E1074"),sQuery(id+"F15.wireOp",EDGE,"E1075"),sQuery(id+"F15.wireOp",EDGE,"E1076"),sQuery(id+"F15.wireOp",EDGE,"E1077"),sQuery(id+"F15.wireOp",EDGE,"E1078"),sQuery(id+"F15.wireOp",EDGE,"E1079"),sQuery(id+"F15.wireOp",EDGE,"E1080"),sQuery(id+"F15.wireOp",EDGE,"E1081"),sQuery(id+"F15.wireOp",EDGE,"E1082"),sQuery(id+"F15.wireOp",EDGE,"E1083"),sQuery(id+"F15.wireOp",EDGE,"E1084"),sQuery(id+"F15.wireOp",EDGE,"E1085"),sQuery(id+"F15.wireOp",EDGE,"E1086"),sQuery(id+"F15.wireOp",EDGE,"E1087"),sQuery(id+"F15.wireOp",EDGE,"E1088"),sQuery(id+"F15.wireOp",EDGE,"E1089"),sQuery(id+"F15.wireOp",EDGE,"E1090"),sQuery(id+"F15.wireOp",EDGE,"E1091"),sQuery(id+"F15.wireOp",EDGE,"E1092"),sQuery(id+"F15.wireOp",EDGE,"E1093"),sQuery(id+"F15.wireOp",EDGE,"E1094"),sQuery(id+"F15.wireOp",EDGE,"E1095"),sQuery(id+"F15.wireOp",EDGE,"E1096"),sQuery(id+"F15.wireOp",EDGE,"E1097"),sQuery(id+"F15.wireOp",EDGE,"E1098"),sQuery(id+"F15.wireOp",EDGE,"E1099"),sQuery(id+"F15.wireOp",EDGE,"E1100"),sQuery(id+"F15.wireOp",EDGE,"E1101"),sQuery(id+"F15.wireOp",EDGE,"E1102"),sQuery(id+"F15.wireOp",EDGE,"E1103"),sQuery(id+"F15.wireOp",EDGE,"E1104"),sQuery(id+"F15.wireOp",EDGE,"E1105"),sQuery(id+"F15.wireOp",EDGE,"E1106"),sQuery(id+"F15.wireOp",EDGE,"E1107"),sQuery(id+"F15.wireOp",EDGE,"E1108"),sQuery(id+"F15.wireOp",EDGE,"E1109"),sQuery(id+"F15.wireOp",EDGE,"E1110"),sQuery(id+"F15.wireOp",EDGE,"E1111"),sQuery(id+"F15.wireOp",EDGE,"E1112"),sQuery(id+"F15.wireOp",EDGE,"E1113"),sQuery(id+"F15.wireOp",EDGE,"E1114"),sQuery(id+"F15.wireOp",EDGE,"E1115"),sQuery(id+"F15.wireOp",EDGE,"E1116"),sQuery(id+"F15.wireOp",EDGE,"E1117"),sQuery(id+"F15.wireOp",EDGE,"E1118"),sQuery(id+"F15.wireOp",EDGE,"E1119"),sQuery(id+"F15.wireOp",EDGE,"E1120"),sQuery(id+"F15.wireOp",EDGE,"E1121"),sQuery(id+"F15.wireOp",EDGE,"E1122"),sQuery(id+"F15.wireOp",EDGE,"E1123"),sQuery(id+"F15.wireOp",EDGE,"E1124"),sQuery(id+"F15.wireOp",EDGE,"E1125"),sQuery(id+"F15.wireOp",EDGE,"E1126"),sQuery(id+"F15.wireOp",EDGE,"E1127"),sQuery(id+"F15.wireOp",EDGE,"E1128"),sQuery(id+"F15.wireOp",EDGE,"E1128"),sQuery(id+"F15.wireOp",EDGE,"E1129"),sQuery(id+"F15.wireOp",EDGE,"E1130")])]});
            var Q1;
            Q1=qCreatedBy(makeId("Origin.pointOp"),VERTEX);
            transform(context, id + "F17", {"entities" : qUnion([Q0]), "transformType" : TransformType.SCALE_UNIFORMLY, "scale" : 1.08, "scalePoint" : qUnion([Q1]), "makeCopy" : false});
        }
        {
            var Q0;
            {var subQ10=sQuery(id+"F10.wireOp",EDGE,"E69");Q0=makeQuery(id+"F10.imprint","IMPRINT",FACE,{"disambiguationData":[TD([[makeQuery(id+"F10.imprint","IMPRINT",EDGE,{"derivedFrom":subQ10}),-1.0]])]});}
            var sketch = newSketch(context, id + "F18", { "sketchPlane" : qUnion([Q0])});
            skCircle(sketch, "E1131", {"center": v(0, 0) * mm, "radius": 5.8 * mm});
            skSolve(sketch);
        }
        {
            var Q0;
            Q0=qSketchRegion(id+"F18",true);
            extrude(context, id + "F19", {"entities" : qUnion([Q0]), "operationType" : NewBodyOperationType.REMOVE, "oppositeDirection" : true, "depth" : 4 * mm, "offsetDistance" : 25 * mm});
        }
        {
            var Q0;
            {var subQ0=sQuery(id+"F0.wireOp",EDGE,"E1");Q0=makeQuery(id+"F7.boolean.opBoolean","MERGE",FACE,{"derivedFrom":[makeQuery(id+"F1.opExtrude","CAP_FACE",FACE,{"disambiguationData":[OSD([sQuery(id+"F0.wireOp",EDGE,"E0"),subQ0])],"isStart":false}),makeQuery(id+"F7.opExtrude","CAP_FACE",FACE,{"disambiguationData":[OSD([subQ0,sQuery(id+"F6.wireOp",EDGE,"E10"),sQuery(id+"F6.wireOp",EDGE,"E12.1.1")])],"isStart":true}),makeQuery(id+"F7.opExtrude","CAP_FACE",FACE,{"disambiguationData":[OSD([subQ0,sQuery(id+"F6.wireOp",EDGE,"E11"),sQuery(id+"F6.wireOp",EDGE,"E12.9.0")])],"isStart":true}),makeQuery(id+"F7.opExtrude","CAP_FACE",FACE,{"disambiguationData":[OSD([subQ0,sQuery(id+"F6.wireOp",EDGE,"E12.1.0"),sQuery(id+"F6.wireOp",EDGE,"E12.2.1")])],"isStart":true}),makeQuery(id+"F7.opExtrude","CAP_FACE",FACE,{"disambiguationData":[OSD([subQ0,sQuery(id+"F6.wireOp",EDGE,"E12.2.0"),sQuery(id+"F6.wireOp",EDGE,"E12.3.1")])],"isStart":true}),makeQuery(id+"F7.opExtrude","CAP_FACE",FACE,{"disambiguationData":[OSD([subQ0,sQuery(id+"F6.wireOp",EDGE,"E12.3.0"),sQuery(id+"F6.wireOp",EDGE,"E12.4.1")])],"isStart":true}),makeQuery(id+"F7.opExtrude","CAP_FACE",FACE,{"disambiguationData":[OSD([subQ0,sQuery(id+"F6.wireOp",EDGE,"E12.4.0"),sQuery(id+"F6.wireOp",EDGE,"E12.5.1")])],"isStart":true}),makeQuery(id+"F7.opExtrude","CAP_FACE",FACE,{"disambiguationData":[OSD([subQ0,sQuery(id+"F6.wireOp",EDGE,"E12.5.0"),sQuery(id+"F6.wireOp",EDGE,"E12.6.1")])],"isStart":true}),makeQuery(id+"F7.opExtrude","CAP_FACE",FACE,{"disambiguationData":[OSD([subQ0,sQuery(id+"F6.wireOp",EDGE,"E12.6.0"),sQuery(id+"F6.wireOp",EDGE,"E12.7.1")])],"isStart":true}),makeQuery(id+"F7.opExtrude","CAP_FACE",FACE,{"disambiguationData":[OSD([subQ0,sQuery(id+"F6.wireOp",EDGE,"E12.7.0"),sQuery(id+"F6.wireOp",EDGE,"E12.8.1")])],"isStart":true}),makeQuery(id+"F7.opExtrude","CAP_FACE",FACE,{"disambiguationData":[OSD([subQ0,sQuery(id+"F6.wireOp",EDGE,"E12.8.0"),sQuery(id+"F6.wireOp",EDGE,"E12.9.1")])],"isStart":true})]});}
            extrude(context, id + "F20", {"entities" : qUnion([Q0]), "operationType" : NewBodyOperationType.REMOVE, "oppositeDirection" : true, "depth" : 1 * mm, "offsetDistance" : 25 * mm});
        }
        {
            var Q0;
            Q0=makeQuery(id+"F16.opExtrude","CAP_FACE",FACE,{"disambiguationData":[OSD([sQuery(id+"F0.wireOp",EDGE,"E0"),sQuery(id+"F13.wireOp",EDGE,"E572"),sQuery(id+"F15.wireOp",EDGE,"E573"),sQuery(id+"F15.wireOp",EDGE,"E574"),sQuery(id+"F15.wireOp",EDGE,"E575"),sQuery(id+"F15.wireOp",EDGE,"E576"),sQuery(id+"F15.wireOp",EDGE,"E577"),sQuery(id+"F15.wireOp",EDGE,"E578"),sQuery(id+"F15.wireOp",EDGE,"E579"),sQuery(id+"F15.wireOp",EDGE,"E580"),sQuery(id+"F15.wireOp",EDGE,"E581"),sQuery(id+"F15.wireOp",EDGE,"E582"),sQuery(id+"F15.wireOp",EDGE,"E583"),sQuery(id+"F15.wireOp",EDGE,"E584"),sQuery(id+"F15.wireOp",EDGE,"E585"),sQuery(id+"F15.wireOp",EDGE,"E586"),sQuery(id+"F15.wireOp",EDGE,"E587"),sQuery(id+"F15.wireOp",EDGE,"E588"),sQuery(id+"F15.wireOp",EDGE,"E589"),sQuery(id+"F15.wireOp",EDGE,"E590"),sQuery(id+"F15.wireOp",EDGE,"E591"),sQuery(id+"F15.wireOp",EDGE,"E592"),sQuery(id+"F15.wireOp",EDGE,"E593"),sQuery(id+"F15.wireOp",EDGE,"E594"),sQuery(id+"F15.wireOp",EDGE,"E595"),sQuery(id+"F15.wireOp",EDGE,"E596"),sQuery(id+"F15.wireOp",EDGE,"E597"),sQuery(id+"F15.wireOp",EDGE,"E598"),sQuery(id+"F15.wireOp",EDGE,"E599"),sQuery(id+"F15.wireOp",EDGE,"E600"),sQuery(id+"F15.wireOp",EDGE,"E601"),sQuery(id+"F15.wireOp",EDGE,"E602"),sQuery(id+"F15.wireOp",EDGE,"E603"),sQuery(id+"F15.wireOp",EDGE,"E604"),sQuery(id+"F15.wireOp",EDGE,"E605"),sQuery(id+"F15.wireOp",EDGE,"E606"),sQuery(id+"F15.wireOp",EDGE,"E607"),sQuery(id+"F15.wireOp",EDGE,"E608"),sQuery(id+"F15.wireOp",EDGE,"E609"),sQuery(id+"F15.wireOp",EDGE,"E610"),sQuery(id+"F15.wireOp",EDGE,"E611"),sQuery(id+"F15.wireOp",EDGE,"E612"),sQuery(id+"F15.wireOp",EDGE,"E613"),sQuery(id+"F15.wireOp",EDGE,"E614"),sQuery(id+"F15.wireOp",EDGE,"E615"),sQuery(id+"F15.wireOp",EDGE,"E616"),sQuery(id+"F15.wireOp",EDGE,"E617"),sQuery(id+"F15.wireOp",EDGE,"E618"),sQuery(id+"F15.wireOp",EDGE,"E619"),sQuery(id+"F15.wireOp",EDGE,"E620"),sQuery(id+"F15.wireOp",EDGE,"E621"),sQuery(id+"F15.wireOp",EDGE,"E622"),sQuery(id+"F15.wireOp",EDGE,"E623"),sQuery(id+"F15.wireOp",EDGE,"E624"),sQuery(id+"F15.wireOp",EDGE,"E625"),sQuery(id+"F15.wireOp",EDGE,"E626"),sQuery(id+"F15.wireOp",EDGE,"E627"),sQuery(id+"F15.wireOp",EDGE,"E628"),sQuery(id+"F15.wireOp",EDGE,"E629"),sQuery(id+"F15.wireOp",EDGE,"E630"),sQuery(id+"F15.wireOp",EDGE,"E631"),sQuery(id+"F15.wireOp",EDGE,"E632"),sQuery(id+"F15.wireOp",EDGE,"E633"),sQuery(id+"F15.wireOp",EDGE,"E634"),sQuery(id+"F15.wireOp",EDGE,"E635"),sQuery(id+"F15.wireOp",EDGE,"E636"),sQuery(id+"F15.wireOp",EDGE,"E637"),sQuery(id+"F15.wireOp",EDGE,"E638"),sQuery(id+"F15.wireOp",EDGE,"E639"),sQuery(id+"F15.wireOp",EDGE,"E640"),sQuery(id+"F15.wireOp",EDGE,"E641"),sQuery(id+"F15.wireOp",EDGE,"E642"),sQuery(id+"F15.wireOp",EDGE,"E643"),sQuery(id+"F15.wireOp",EDGE,"E644"),sQuery(id+"F15.wireOp",EDGE,"E645"),sQuery(id+"F15.wireOp",EDGE,"E646"),sQuery(id+"F15.wireOp",EDGE,"E647"),sQuery(id+"F15.wireOp",EDGE,"E648"),sQuery(id+"F15.wireOp",EDGE,"E649"),sQuery(id+"F15.wireOp",EDGE,"E650"),sQuery(id+"F15.wireOp",EDGE,"E651"),sQuery(id+"F15.wireOp",EDGE,"E652"),sQuery(id+"F15.wireOp",EDGE,"E653"),sQuery(id+"F15.wireOp",EDGE,"E654"),sQuery(id+"F15.wireOp",EDGE,"E655"),sQuery(id+"F15.wireOp",EDGE,"E656"),sQuery(id+"F15.wireOp",EDGE,"E657"),sQuery(id+"F15.wireOp",EDGE,"E658"),sQuery(id+"F15.wireOp",EDGE,"E659"),sQuery(id+"F15.wireOp",EDGE,"E660"),sQuery(id+"F15.wireOp",EDGE,"E661"),sQuery(id+"F15.wireOp",EDGE,"E662"),sQuery(id+"F15.wireOp",EDGE,"E663"),sQuery(id+"F15.wireOp",EDGE,"E664"),sQuery(id+"F15.wireOp",EDGE,"E665"),sQuery(id+"F15.wireOp",EDGE,"E666"),sQuery(id+"F15.wireOp",EDGE,"E667"),sQuery(id+"F15.wireOp",EDGE,"E668"),sQuery(id+"F15.wireOp",EDGE,"E669"),sQuery(id+"F15.wireOp",EDGE,"E670"),sQuery(id+"F15.wireOp",EDGE,"E671"),sQuery(id+"F15.wireOp",EDGE,"E672"),sQuery(id+"F15.wireOp",EDGE,"E673"),sQuery(id+"F15.wireOp",EDGE,"E674"),sQuery(id+"F15.wireOp",EDGE,"E675"),sQuery(id+"F15.wireOp",EDGE,"E676"),sQuery(id+"F15.wireOp",EDGE,"E677"),sQuery(id+"F15.wireOp",EDGE,"E678"),sQuery(id+"F15.wireOp",EDGE,"E679"),sQuery(id+"F15.wireOp",EDGE,"E680"),sQuery(id+"F15.wireOp",EDGE,"E681"),sQuery(id+"F15.wireOp",EDGE,"E682"),sQuery(id+"F15.wireOp",EDGE,"E683"),sQuery(id+"F15.wireOp",EDGE,"E684"),sQuery(id+"F15.wireOp",EDGE,"E685"),sQuery(id+"F15.wireOp",EDGE,"E686"),sQuery(id+"F15.wireOp",EDGE,"E687"),sQuery(id+"F15.wireOp",EDGE,"E688"),sQuery(id+"F15.wireOp",EDGE,"E689"),sQuery(id+"F15.wireOp",EDGE,"E690"),sQuery(id+"F15.wireOp",EDGE,"E691"),sQuery(id+"F15.wireOp",EDGE,"E692"),sQuery(id+"F15.wireOp",EDGE,"E693"),sQuery(id+"F15.wireOp",EDGE,"E694"),sQuery(id+"F15.wireOp",EDGE,"E695"),sQuery(id+"F15.wireOp",EDGE,"E696"),sQuery(id+"F15.wireOp",EDGE,"E697"),sQuery(id+"F15.wireOp",EDGE,"E698"),sQuery(id+"F15.wireOp",EDGE,"E699"),sQuery(id+"F15.wireOp",EDGE,"E700"),sQuery(id+"F15.wireOp",EDGE,"E701"),sQuery(id+"F15.wireOp",EDGE,"E702"),sQuery(id+"F15.wireOp",EDGE,"E703"),sQuery(id+"F15.wireOp",EDGE,"E704"),sQuery(id+"F15.wireOp",EDGE,"E705"),sQuery(id+"F15.wireOp",EDGE,"E706"),sQuery(id+"F15.wireOp",EDGE,"E707"),sQuery(id+"F15.wireOp",EDGE,"E708"),sQuery(id+"F15.wireOp",EDGE,"E709"),sQuery(id+"F15.wireOp",EDGE,"E710"),sQuery(id+"F15.wireOp",EDGE,"E711"),sQuery(id+"F15.wireOp",EDGE,"E712"),sQuery(id+"F15.wireOp",EDGE,"E713"),sQuery(id+"F15.wireOp",EDGE,"E714"),sQuery(id+"F15.wireOp",EDGE,"E715"),sQuery(id+"F15.wireOp",EDGE,"E716"),sQuery(id+"F15.wireOp",EDGE,"E717"),sQuery(id+"F15.wireOp",EDGE,"E718"),sQuery(id+"F15.wireOp",EDGE,"E719"),sQuery(id+"F15.wireOp",EDGE,"E720"),sQuery(id+"F15.wireOp",EDGE,"E721"),sQuery(id+"F15.wireOp",EDGE,"E722"),sQuery(id+"F15.wireOp",EDGE,"E723"),sQuery(id+"F15.wireOp",EDGE,"E724"),sQuery(id+"F15.wireOp",EDGE,"E725"),sQuery(id+"F15.wireOp",EDGE,"E726"),sQuery(id+"F15.wireOp",EDGE,"E727"),sQuery(id+"F15.wireOp",EDGE,"E728"),sQuery(id+"F15.wireOp",EDGE,"E729"),sQuery(id+"F15.wireOp",EDGE,"E730"),sQuery(id+"F15.wireOp",EDGE,"E731"),sQuery(id+"F15.wireOp",EDGE,"E732"),sQuery(id+"F15.wireOp",EDGE,"E733"),sQuery(id+"F15.wireOp",EDGE,"E734"),sQuery(id+"F15.wireOp",EDGE,"E735"),sQuery(id+"F15.wireOp",EDGE,"E736"),sQuery(id+"F15.wireOp",EDGE,"E737"),sQuery(id+"F15.wireOp",EDGE,"E738"),sQuery(id+"F15.wireOp",EDGE,"E739"),sQuery(id+"F15.wireOp",EDGE,"E740"),sQuery(id+"F15.wireOp",EDGE,"E741"),sQuery(id+"F15.wireOp",EDGE,"E742"),sQuery(id+"F15.wireOp",EDGE,"E743"),sQuery(id+"F15.wireOp",EDGE,"E744"),sQuery(id+"F15.wireOp",EDGE,"E745"),sQuery(id+"F15.wireOp",EDGE,"E746"),sQuery(id+"F15.wireOp",EDGE,"E747"),sQuery(id+"F15.wireOp",EDGE,"E748"),sQuery(id+"F15.wireOp",EDGE,"E749"),sQuery(id+"F15.wireOp",EDGE,"E750"),sQuery(id+"F15.wireOp",EDGE,"E751"),sQuery(id+"F15.wireOp",EDGE,"E752"),sQuery(id+"F15.wireOp",EDGE,"E753"),sQuery(id+"F15.wireOp",EDGE,"E754"),sQuery(id+"F15.wireOp",EDGE,"E755"),sQuery(id+"F15.wireOp",EDGE,"E756"),sQuery(id+"F15.wireOp",EDGE,"E757"),sQuery(id+"F15.wireOp",EDGE,"E758"),sQuery(id+"F15.wireOp",EDGE,"E759"),sQuery(id+"F15.wireOp",EDGE,"E760"),sQuery(id+"F15.wireOp",EDGE,"E761"),sQuery(id+"F15.wireOp",EDGE,"E762"),sQuery(id+"F15.wireOp",EDGE,"E763"),sQuery(id+"F15.wireOp",EDGE,"E764"),sQuery(id+"F15.wireOp",EDGE,"E765"),sQuery(id+"F15.wireOp",EDGE,"E766"),sQuery(id+"F15.wireOp",EDGE,"E767"),sQuery(id+"F15.wireOp",EDGE,"E768"),sQuery(id+"F15.wireOp",EDGE,"E769"),sQuery(id+"F15.wireOp",EDGE,"E770"),sQuery(id+"F15.wireOp",EDGE,"E771"),sQuery(id+"F15.wireOp",EDGE,"E772"),sQuery(id+"F15.wireOp",EDGE,"E773"),sQuery(id+"F15.wireOp",EDGE,"E774"),sQuery(id+"F15.wireOp",EDGE,"E775"),sQuery(id+"F15.wireOp",EDGE,"E776"),sQuery(id+"F15.wireOp",EDGE,"E777"),sQuery(id+"F15.wireOp",EDGE,"E778"),sQuery(id+"F15.wireOp",EDGE,"E779"),sQuery(id+"F15.wireOp",EDGE,"E780"),sQuery(id+"F15.wireOp",EDGE,"E781"),sQuery(id+"F15.wireOp",EDGE,"E782"),sQuery(id+"F15.wireOp",EDGE,"E783"),sQuery(id+"F15.wireOp",EDGE,"E784"),sQuery(id+"F15.wireOp",EDGE,"E785"),sQuery(id+"F15.wireOp",EDGE,"E786"),sQuery(id+"F15.wireOp",EDGE,"E787"),sQuery(id+"F15.wireOp",EDGE,"E788"),sQuery(id+"F15.wireOp",EDGE,"E789"),sQuery(id+"F15.wireOp",EDGE,"E790"),sQuery(id+"F15.wireOp",EDGE,"E791"),sQuery(id+"F15.wireOp",EDGE,"E792"),sQuery(id+"F15.wireOp",EDGE,"E793"),sQuery(id+"F15.wireOp",EDGE,"E794"),sQuery(id+"F15.wireOp",EDGE,"E795"),sQuery(id+"F15.wireOp",EDGE,"E796"),sQuery(id+"F15.wireOp",EDGE,"E797"),sQuery(id+"F15.wireOp",EDGE,"E798"),sQuery(id+"F15.wireOp",EDGE,"E799"),sQuery(id+"F15.wireOp",EDGE,"E800"),sQuery(id+"F15.wireOp",EDGE,"E801"),sQuery(id+"F15.wireOp",EDGE,"E802"),sQuery(id+"F15.wireOp",EDGE,"E803"),sQuery(id+"F15.wireOp",EDGE,"E804"),sQuery(id+"F15.wireOp",EDGE,"E805"),sQuery(id+"F15.wireOp",EDGE,"E806"),sQuery(id+"F15.wireOp",EDGE,"E807"),sQuery(id+"F15.wireOp",EDGE,"E808"),sQuery(id+"F15.wireOp",EDGE,"E809"),sQuery(id+"F15.wireOp",EDGE,"E810"),sQuery(id+"F15.wireOp",EDGE,"E811"),sQuery(id+"F15.wireOp",EDGE,"E812"),sQuery(id+"F15.wireOp",EDGE,"E813"),sQuery(id+"F15.wireOp",EDGE,"E814"),sQuery(id+"F15.wireOp",EDGE,"E815"),sQuery(id+"F15.wireOp",EDGE,"E816"),sQuery(id+"F15.wireOp",EDGE,"E817"),sQuery(id+"F15.wireOp",EDGE,"E818"),sQuery(id+"F15.wireOp",EDGE,"E819"),sQuery(id+"F15.wireOp",EDGE,"E820"),sQuery(id+"F15.wireOp",EDGE,"E821"),sQuery(id+"F15.wireOp",EDGE,"E822"),sQuery(id+"F15.wireOp",EDGE,"E823"),sQuery(id+"F15.wireOp",EDGE,"E824"),sQuery(id+"F15.wireOp",EDGE,"E825"),sQuery(id+"F15.wireOp",EDGE,"E826"),sQuery(id+"F15.wireOp",EDGE,"E827"),sQuery(id+"F15.wireOp",EDGE,"E828"),sQuery(id+"F15.wireOp",EDGE,"E829"),sQuery(id+"F15.wireOp",EDGE,"E830"),sQuery(id+"F15.wireOp",EDGE,"E831"),sQuery(id+"F15.wireOp",EDGE,"E832"),sQuery(id+"F15.wireOp",EDGE,"E833"),sQuery(id+"F15.wireOp",EDGE,"E834"),sQuery(id+"F15.wireOp",EDGE,"E835"),sQuery(id+"F15.wireOp",EDGE,"E836"),sQuery(id+"F15.wireOp",EDGE,"E837"),sQuery(id+"F15.wireOp",EDGE,"E838"),sQuery(id+"F15.wireOp",EDGE,"E839"),sQuery(id+"F15.wireOp",EDGE,"E840"),sQuery(id+"F15.wireOp",EDGE,"E841"),sQuery(id+"F15.wireOp",EDGE,"E842"),sQuery(id+"F15.wireOp",EDGE,"E843"),sQuery(id+"F15.wireOp",EDGE,"E844"),sQuery(id+"F15.wireOp",EDGE,"E845"),sQuery(id+"F15.wireOp",EDGE,"E846"),sQuery(id+"F15.wireOp",EDGE,"E847"),sQuery(id+"F15.wireOp",EDGE,"E848"),sQuery(id+"F15.wireOp",EDGE,"E849"),sQuery(id+"F15.wireOp",EDGE,"E849"),sQuery(id+"F15.wireOp",EDGE,"E850"),sQuery(id+"F15.wireOp",EDGE,"E851"),sQuery(id+"F15.wireOp",EDGE,"E852"),sQuery(id+"F15.wireOp",EDGE,"E853"),sQuery(id+"F15.wireOp",EDGE,"E854"),sQuery(id+"F15.wireOp",EDGE,"E855"),sQuery(id+"F15.wireOp",EDGE,"E856"),sQuery(id+"F15.wireOp",EDGE,"E857"),sQuery(id+"F15.wireOp",EDGE,"E858"),sQuery(id+"F15.wireOp",EDGE,"E859"),sQuery(id+"F15.wireOp",EDGE,"E860"),sQuery(id+"F15.wireOp",EDGE,"E861"),sQuery(id+"F15.wireOp",EDGE,"E862"),sQuery(id+"F15.wireOp",EDGE,"E863"),sQuery(id+"F15.wireOp",EDGE,"E864"),sQuery(id+"F15.wireOp",EDGE,"E865"),sQuery(id+"F15.wireOp",EDGE,"E866"),sQuery(id+"F15.wireOp",EDGE,"E867"),sQuery(id+"F15.wireOp",EDGE,"E868"),sQuery(id+"F15.wireOp",EDGE,"E869"),sQuery(id+"F15.wireOp",EDGE,"E870"),sQuery(id+"F15.wireOp",EDGE,"E871"),sQuery(id+"F15.wireOp",EDGE,"E872"),sQuery(id+"F15.wireOp",EDGE,"E873"),sQuery(id+"F15.wireOp",EDGE,"E874"),sQuery(id+"F15.wireOp",EDGE,"E875"),sQuery(id+"F15.wireOp",EDGE,"E876"),sQuery(id+"F15.wireOp",EDGE,"E877"),sQuery(id+"F15.wireOp",EDGE,"E878"),sQuery(id+"F15.wireOp",EDGE,"E879"),sQuery(id+"F15.wireOp",EDGE,"E880"),sQuery(id+"F15.wireOp",EDGE,"E881"),sQuery(id+"F15.wireOp",EDGE,"E882"),sQuery(id+"F15.wireOp",EDGE,"E883"),sQuery(id+"F15.wireOp",EDGE,"E884"),sQuery(id+"F15.wireOp",EDGE,"E885"),sQuery(id+"F15.wireOp",EDGE,"E886"),sQuery(id+"F15.wireOp",EDGE,"E887"),sQuery(id+"F15.wireOp",EDGE,"E888"),sQuery(id+"F15.wireOp",EDGE,"E889"),sQuery(id+"F15.wireOp",EDGE,"E890"),sQuery(id+"F15.wireOp",EDGE,"E891"),sQuery(id+"F15.wireOp",EDGE,"E892"),sQuery(id+"F15.wireOp",EDGE,"E893"),sQuery(id+"F15.wireOp",EDGE,"E894"),sQuery(id+"F15.wireOp",EDGE,"E895"),sQuery(id+"F15.wireOp",EDGE,"E896"),sQuery(id+"F15.wireOp",EDGE,"E897"),sQuery(id+"F15.wireOp",EDGE,"E898"),sQuery(id+"F15.wireOp",EDGE,"E899"),sQuery(id+"F15.wireOp",EDGE,"E900"),sQuery(id+"F15.wireOp",EDGE,"E901"),sQuery(id+"F15.wireOp",EDGE,"E902"),sQuery(id+"F15.wireOp",EDGE,"E903"),sQuery(id+"F15.wireOp",EDGE,"E904"),sQuery(id+"F15.wireOp",EDGE,"E905"),sQuery(id+"F15.wireOp",EDGE,"E906"),sQuery(id+"F15.wireOp",EDGE,"E907"),sQuery(id+"F15.wireOp",EDGE,"E908"),sQuery(id+"F15.wireOp",EDGE,"E909"),sQuery(id+"F15.wireOp",EDGE,"E910"),sQuery(id+"F15.wireOp",EDGE,"E911"),sQuery(id+"F15.wireOp",EDGE,"E912"),sQuery(id+"F15.wireOp",EDGE,"E913"),sQuery(id+"F15.wireOp",EDGE,"E914"),sQuery(id+"F15.wireOp",EDGE,"E915"),sQuery(id+"F15.wireOp",EDGE,"E916"),sQuery(id+"F15.wireOp",EDGE,"E917"),sQuery(id+"F15.wireOp",EDGE,"E918"),sQuery(id+"F15.wireOp",EDGE,"E919"),sQuery(id+"F15.wireOp",EDGE,"E920"),sQuery(id+"F15.wireOp",EDGE,"E921"),sQuery(id+"F15.wireOp",EDGE,"E922"),sQuery(id+"F15.wireOp",EDGE,"E923"),sQuery(id+"F15.wireOp",EDGE,"E924"),sQuery(id+"F15.wireOp",EDGE,"E925"),sQuery(id+"F15.wireOp",EDGE,"E926"),sQuery(id+"F15.wireOp",EDGE,"E927"),sQuery(id+"F15.wireOp",EDGE,"E928"),sQuery(id+"F15.wireOp",EDGE,"E929"),sQuery(id+"F15.wireOp",EDGE,"E930"),sQuery(id+"F15.wireOp",EDGE,"E931"),sQuery(id+"F15.wireOp",EDGE,"E932"),sQuery(id+"F15.wireOp",EDGE,"E933"),sQuery(id+"F15.wireOp",EDGE,"E934"),sQuery(id+"F15.wireOp",EDGE,"E935"),sQuery(id+"F15.wireOp",EDGE,"E936"),sQuery(id+"F15.wireOp",EDGE,"E937"),sQuery(id+"F15.wireOp",EDGE,"E938"),sQuery(id+"F15.wireOp",EDGE,"E939"),sQuery(id+"F15.wireOp",EDGE,"E940"),sQuery(id+"F15.wireOp",EDGE,"E941"),sQuery(id+"F15.wireOp",EDGE,"E942"),sQuery(id+"F15.wireOp",EDGE,"E943"),sQuery(id+"F15.wireOp",EDGE,"E944"),sQuery(id+"F15.wireOp",EDGE,"E945"),sQuery(id+"F15.wireOp",EDGE,"E946"),sQuery(id+"F15.wireOp",EDGE,"E947"),sQuery(id+"F15.wireOp",EDGE,"E948"),sQuery(id+"F15.wireOp",EDGE,"E949"),sQuery(id+"F15.wireOp",EDGE,"E950"),sQuery(id+"F15.wireOp",EDGE,"E951"),sQuery(id+"F15.wireOp",EDGE,"E952"),sQuery(id+"F15.wireOp",EDGE,"E953"),sQuery(id+"F15.wireOp",EDGE,"E954"),sQuery(id+"F15.wireOp",EDGE,"E955"),sQuery(id+"F15.wireOp",EDGE,"E956"),sQuery(id+"F15.wireOp",EDGE,"E957"),sQuery(id+"F15.wireOp",EDGE,"E958"),sQuery(id+"F15.wireOp",EDGE,"E959"),sQuery(id+"F15.wireOp",EDGE,"E960"),sQuery(id+"F15.wireOp",EDGE,"E961"),sQuery(id+"F15.wireOp",EDGE,"E962"),sQuery(id+"F15.wireOp",EDGE,"E963"),sQuery(id+"F15.wireOp",EDGE,"E964"),sQuery(id+"F15.wireOp",EDGE,"E965"),sQuery(id+"F15.wireOp",EDGE,"E966"),sQuery(id+"F15.wireOp",EDGE,"E967"),sQuery(id+"F15.wireOp",EDGE,"E968"),sQuery(id+"F15.wireOp",EDGE,"E969"),sQuery(id+"F15.wireOp",EDGE,"E970"),sQuery(id+"F15.wireOp",EDGE,"E971"),sQuery(id+"F15.wireOp",EDGE,"E972"),sQuery(id+"F15.wireOp",EDGE,"E973"),sQuery(id+"F15.wireOp",EDGE,"E974"),sQuery(id+"F15.wireOp",EDGE,"E975"),sQuery(id+"F15.wireOp",EDGE,"E976"),sQuery(id+"F15.wireOp",EDGE,"E977"),sQuery(id+"F15.wireOp",EDGE,"E978"),sQuery(id+"F15.wireOp",EDGE,"E979"),sQuery(id+"F15.wireOp",EDGE,"E980"),sQuery(id+"F15.wireOp",EDGE,"E981"),sQuery(id+"F15.wireOp",EDGE,"E982"),sQuery(id+"F15.wireOp",EDGE,"E983"),sQuery(id+"F15.wireOp",EDGE,"E984"),sQuery(id+"F15.wireOp",EDGE,"E985"),sQuery(id+"F15.wireOp",EDGE,"E986"),sQuery(id+"F15.wireOp",EDGE,"E987"),sQuery(id+"F15.wireOp",EDGE,"E988"),sQuery(id+"F15.wireOp",EDGE,"E989"),sQuery(id+"F15.wireOp",EDGE,"E990"),sQuery(id+"F15.wireOp",EDGE,"E991"),sQuery(id+"F15.wireOp",EDGE,"E992"),sQuery(id+"F15.wireOp",EDGE,"E993"),sQuery(id+"F15.wireOp",EDGE,"E994"),sQuery(id+"F15.wireOp",EDGE,"E995"),sQuery(id+"F15.wireOp",EDGE,"E996"),sQuery(id+"F15.wireOp",EDGE,"E997"),sQuery(id+"F15.wireOp",EDGE,"E998"),sQuery(id+"F15.wireOp",EDGE,"E999"),sQuery(id+"F15.wireOp",EDGE,"E1000"),sQuery(id+"F15.wireOp",EDGE,"E1001"),sQuery(id+"F15.wireOp",EDGE,"E1002"),sQuery(id+"F15.wireOp",EDGE,"E1003"),sQuery(id+"F15.wireOp",EDGE,"E1004"),sQuery(id+"F15.wireOp",EDGE,"E1005"),sQuery(id+"F15.wireOp",EDGE,"E1006"),sQuery(id+"F15.wireOp",EDGE,"E1007"),sQuery(id+"F15.wireOp",EDGE,"E1008"),sQuery(id+"F15.wireOp",EDGE,"E1009"),sQuery(id+"F15.wireOp",EDGE,"E1010"),sQuery(id+"F15.wireOp",EDGE,"E1011"),sQuery(id+"F15.wireOp",EDGE,"E1012"),sQuery(id+"F15.wireOp",EDGE,"E1013"),sQuery(id+"F15.wireOp",EDGE,"E1014"),sQuery(id+"F15.wireOp",EDGE,"E1015"),sQuery(id+"F15.wireOp",EDGE,"E1016"),sQuery(id+"F15.wireOp",EDGE,"E1017"),sQuery(id+"F15.wireOp",EDGE,"E1018"),sQuery(id+"F15.wireOp",EDGE,"E1019"),sQuery(id+"F15.wireOp",EDGE,"E1020"),sQuery(id+"F15.wireOp",EDGE,"E1021"),sQuery(id+"F15.wireOp",EDGE,"E1022"),sQuery(id+"F15.wireOp",EDGE,"E1023"),sQuery(id+"F15.wireOp",EDGE,"E1024"),sQuery(id+"F15.wireOp",EDGE,"E1025"),sQuery(id+"F15.wireOp",EDGE,"E1026"),sQuery(id+"F15.wireOp",EDGE,"E1027"),sQuery(id+"F15.wireOp",EDGE,"E1028"),sQuery(id+"F15.wireOp",EDGE,"E1029"),sQuery(id+"F15.wireOp",EDGE,"E1030"),sQuery(id+"F15.wireOp",EDGE,"E1031"),sQuery(id+"F15.wireOp",EDGE,"E1032"),sQuery(id+"F15.wireOp",EDGE,"E1033"),sQuery(id+"F15.wireOp",EDGE,"E1034"),sQuery(id+"F15.wireOp",EDGE,"E1035"),sQuery(id+"F15.wireOp",EDGE,"E1036"),sQuery(id+"F15.wireOp",EDGE,"E1037"),sQuery(id+"F15.wireOp",EDGE,"E1038"),sQuery(id+"F15.wireOp",EDGE,"E1039"),sQuery(id+"F15.wireOp",EDGE,"E1040"),sQuery(id+"F15.wireOp",EDGE,"E1041"),sQuery(id+"F15.wireOp",EDGE,"E1042"),sQuery(id+"F15.wireOp",EDGE,"E1043"),sQuery(id+"F15.wireOp",EDGE,"E1044"),sQuery(id+"F15.wireOp",EDGE,"E1045"),sQuery(id+"F15.wireOp",EDGE,"E1046"),sQuery(id+"F15.wireOp",EDGE,"E1047"),sQuery(id+"F15.wireOp",EDGE,"E1048"),sQuery(id+"F15.wireOp",EDGE,"E1049"),sQuery(id+"F15.wireOp",EDGE,"E1050"),sQuery(id+"F15.wireOp",EDGE,"E1051"),sQuery(id+"F15.wireOp",EDGE,"E1052"),sQuery(id+"F15.wireOp",EDGE,"E1053"),sQuery(id+"F15.wireOp",EDGE,"E1054"),sQuery(id+"F15.wireOp",EDGE,"E1055"),sQuery(id+"F15.wireOp",EDGE,"E1056"),sQuery(id+"F15.wireOp",EDGE,"E1057"),sQuery(id+"F15.wireOp",EDGE,"E1058"),sQuery(id+"F15.wireOp",EDGE,"E1059"),sQuery(id+"F15.wireOp",EDGE,"E1060"),sQuery(id+"F15.wireOp",EDGE,"E1061"),sQuery(id+"F15.wireOp",EDGE,"E1062"),sQuery(id+"F15.wireOp",EDGE,"E1063"),sQuery(id+"F15.wireOp",EDGE,"E1064"),sQuery(id+"F15.wireOp",EDGE,"E1065"),sQuery(id+"F15.wireOp",EDGE,"E1066"),sQuery(id+"F15.wireOp",EDGE,"E1067"),sQuery(id+"F15.wireOp",EDGE,"E1068"),sQuery(id+"F15.wireOp",EDGE,"E1069"),sQuery(id+"F15.wireOp",EDGE,"E1070"),sQuery(id+"F15.wireOp",EDGE,"E1071"),sQuery(id+"F15.wireOp",EDGE,"E1072"),sQuery(id+"F15.wireOp",EDGE,"E1073"),sQuery(id+"F15.wireOp",EDGE,"E1074"),sQuery(id+"F15.wireOp",EDGE,"E1075"),sQuery(id+"F15.wireOp",EDGE,"E1076"),sQuery(id+"F15.wireOp",EDGE,"E1077"),sQuery(id+"F15.wireOp",EDGE,"E1078"),sQuery(id+"F15.wireOp",EDGE,"E1079"),sQuery(id+"F15.wireOp",EDGE,"E1080"),sQuery(id+"F15.wireOp",EDGE,"E1081"),sQuery(id+"F15.wireOp",EDGE,"E1082"),sQuery(id+"F15.wireOp",EDGE,"E1083"),sQuery(id+"F15.wireOp",EDGE,"E1084"),sQuery(id+"F15.wireOp",EDGE,"E1085"),sQuery(id+"F15.wireOp",EDGE,"E1086"),sQuery(id+"F15.wireOp",EDGE,"E1087"),sQuery(id+"F15.wireOp",EDGE,"E1088"),sQuery(id+"F15.wireOp",EDGE,"E1089"),sQuery(id+"F15.wireOp",EDGE,"E1090"),sQuery(id+"F15.wireOp",EDGE,"E1091"),sQuery(id+"F15.wireOp",EDGE,"E1092"),sQuery(id+"F15.wireOp",EDGE,"E1093"),sQuery(id+"F15.wireOp",EDGE,"E1094"),sQuery(id+"F15.wireOp",EDGE,"E1095"),sQuery(id+"F15.wireOp",EDGE,"E1096"),sQuery(id+"F15.wireOp",EDGE,"E1097"),sQuery(id+"F15.wireOp",EDGE,"E1098"),sQuery(id+"F15.wireOp",EDGE,"E1099"),sQuery(id+"F15.wireOp",EDGE,"E1100"),sQuery(id+"F15.wireOp",EDGE,"E1101"),sQuery(id+"F15.wireOp",EDGE,"E1102"),sQuery(id+"F15.wireOp",EDGE,"E1103"),sQuery(id+"F15.wireOp",EDGE,"E1104"),sQuery(id+"F15.wireOp",EDGE,"E1105"),sQuery(id+"F15.wireOp",EDGE,"E1106"),sQuery(id+"F15.wireOp",EDGE,"E1107"),sQuery(id+"F15.wireOp",EDGE,"E1108"),sQuery(id+"F15.wireOp",EDGE,"E1109"),sQuery(id+"F15.wireOp",EDGE,"E1110"),sQuery(id+"F15.wireOp",EDGE,"E1111"),sQuery(id+"F15.wireOp",EDGE,"E1112"),sQuery(id+"F15.wireOp",EDGE,"E1113"),sQuery(id+"F15.wireOp",EDGE,"E1114"),sQuery(id+"F15.wireOp",EDGE,"E1115"),sQuery(id+"F15.wireOp",EDGE,"E1116"),sQuery(id+"F15.wireOp",EDGE,"E1117"),sQuery(id+"F15.wireOp",EDGE,"E1118"),sQuery(id+"F15.wireOp",EDGE,"E1119"),sQuery(id+"F15.wireOp",EDGE,"E1120"),sQuery(id+"F15.wireOp",EDGE,"E1121"),sQuery(id+"F15.wireOp",EDGE,"E1122"),sQuery(id+"F15.wireOp",EDGE,"E1123"),sQuery(id+"F15.wireOp",EDGE,"E1124"),sQuery(id+"F15.wireOp",EDGE,"E1125"),sQuery(id+"F15.wireOp",EDGE,"E1126"),sQuery(id+"F15.wireOp",EDGE,"E1127"),sQuery(id+"F15.wireOp",EDGE,"E1128"),sQuery(id+"F15.wireOp",EDGE,"E1128"),sQuery(id+"F15.wireOp",EDGE,"E1129"),sQuery(id+"F15.wireOp",EDGE,"E1130")])],"isStart":false});
            var sketch = newSketch(context, id + "F21", { "sketchPlane" : qUnion([Q0])});
            skCircle(sketch, "E1132", {"center": v(0, 0) * mm, "radius": 1.55 * mm});
            skCircle(sketch, "E1133", {"center": v(0, 0) * mm, "radius": 1.72 * mm});
            skSolve(sketch);
        }
        {
            var Q0;
            Q0=makeQuery(id+"F21.imprint","IMPRINT",FACE,{"disambiguationData":[TD([[makeQuery(id+"F21.imprint","IMPRINT",EDGE,{"derivedFrom":sQuery(id+"F21.wireOp",EDGE,"E1133")}),1.0]])]});
            var Q1;
            Q1=makeQuery(id+"F21.imprint","IMPRINT",FACE,{"disambiguationData":[TD([[makeQuery(id+"F21.imprint","IMPRINT",EDGE,{"derivedFrom":sQuery(id+"F21.wireOp",EDGE,"E1132")}),-1.0]])]});
            extrude(context, id + "F22", {"entities" : qUnion([Q0, Q1]), "operationType" : NewBodyOperationType.ADD, "oppositeDirection" : true, "depth" : 3 * mm, "offsetDistance" : 25 * mm});
        }
        {
            var Q0;
            Q0=makeQuery(id+"F21.imprint","IMPRINT",FACE,{"disambiguationData":[TD([[makeQuery(id+"F21.imprint","IMPRINT",EDGE,{"derivedFrom":sQuery(id+"F21.wireOp",EDGE,"E1132")}),1.0]])]});
            extrude(context, id + "F23", {"entities" : qUnion([Q0]), "operationType" : NewBodyOperationType.REMOVE, "oppositeDirection" : true, "depth" : 10 * mm, "offsetDistance" : 25 * mm});
        }
        {
            var Q0;
            Q0=makeQuery(id+"F22.boolean.opBoolean","MERGE",FACE,{"derivedFrom":[makeQuery(id+"F16.opExtrude","CAP_FACE",FACE,{"disambiguationData":[OSD([sQuery(id+"F0.wireOp",EDGE,"E0"),sQuery(id+"F13.wireOp",EDGE,"E572"),sQuery(id+"F15.wireOp",EDGE,"E573"),sQuery(id+"F15.wireOp",EDGE,"E574"),sQuery(id+"F15.wireOp",EDGE,"E575"),sQuery(id+"F15.wireOp",EDGE,"E576"),sQuery(id+"F15.wireOp",EDGE,"E577"),sQuery(id+"F15.wireOp",EDGE,"E578"),sQuery(id+"F15.wireOp",EDGE,"E579"),sQuery(id+"F15.wireOp",EDGE,"E580"),sQuery(id+"F15.wireOp",EDGE,"E581"),sQuery(id+"F15.wireOp",EDGE,"E582"),sQuery(id+"F15.wireOp",EDGE,"E583"),sQuery(id+"F15.wireOp",EDGE,"E584"),sQuery(id+"F15.wireOp",EDGE,"E585"),sQuery(id+"F15.wireOp",EDGE,"E586"),sQuery(id+"F15.wireOp",EDGE,"E587"),sQuery(id+"F15.wireOp",EDGE,"E588"),sQuery(id+"F15.wireOp",EDGE,"E589"),sQuery(id+"F15.wireOp",EDGE,"E590"),sQuery(id+"F15.wireOp",EDGE,"E591"),sQuery(id+"F15.wireOp",EDGE,"E592"),sQuery(id+"F15.wireOp",EDGE,"E593"),sQuery(id+"F15.wireOp",EDGE,"E594"),sQuery(id+"F15.wireOp",EDGE,"E595"),sQuery(id+"F15.wireOp",EDGE,"E596"),sQuery(id+"F15.wireOp",EDGE,"E597"),sQuery(id+"F15.wireOp",EDGE,"E598"),sQuery(id+"F15.wireOp",EDGE,"E599"),sQuery(id+"F15.wireOp",EDGE,"E600"),sQuery(id+"F15.wireOp",EDGE,"E601"),sQuery(id+"F15.wireOp",EDGE,"E602"),sQuery(id+"F15.wireOp",EDGE,"E603"),sQuery(id+"F15.wireOp",EDGE,"E604"),sQuery(id+"F15.wireOp",EDGE,"E605"),sQuery(id+"F15.wireOp",EDGE,"E606"),sQuery(id+"F15.wireOp",EDGE,"E607"),sQuery(id+"F15.wireOp",EDGE,"E608"),sQuery(id+"F15.wireOp",EDGE,"E609"),sQuery(id+"F15.wireOp",EDGE,"E610"),sQuery(id+"F15.wireOp",EDGE,"E611"),sQuery(id+"F15.wireOp",EDGE,"E612"),sQuery(id+"F15.wireOp",EDGE,"E613"),sQuery(id+"F15.wireOp",EDGE,"E614"),sQuery(id+"F15.wireOp",EDGE,"E615"),sQuery(id+"F15.wireOp",EDGE,"E616"),sQuery(id+"F15.wireOp",EDGE,"E617"),sQuery(id+"F15.wireOp",EDGE,"E618"),sQuery(id+"F15.wireOp",EDGE,"E619"),sQuery(id+"F15.wireOp",EDGE,"E620"),sQuery(id+"F15.wireOp",EDGE,"E621"),sQuery(id+"F15.wireOp",EDGE,"E622"),sQuery(id+"F15.wireOp",EDGE,"E623"),sQuery(id+"F15.wireOp",EDGE,"E624"),sQuery(id+"F15.wireOp",EDGE,"E625"),sQuery(id+"F15.wireOp",EDGE,"E626"),sQuery(id+"F15.wireOp",EDGE,"E627"),sQuery(id+"F15.wireOp",EDGE,"E628"),sQuery(id+"F15.wireOp",EDGE,"E629"),sQuery(id+"F15.wireOp",EDGE,"E630"),sQuery(id+"F15.wireOp",EDGE,"E631"),sQuery(id+"F15.wireOp",EDGE,"E632"),sQuery(id+"F15.wireOp",EDGE,"E633"),sQuery(id+"F15.wireOp",EDGE,"E634"),sQuery(id+"F15.wireOp",EDGE,"E635"),sQuery(id+"F15.wireOp",EDGE,"E636"),sQuery(id+"F15.wireOp",EDGE,"E637"),sQuery(id+"F15.wireOp",EDGE,"E638"),sQuery(id+"F15.wireOp",EDGE,"E639"),sQuery(id+"F15.wireOp",EDGE,"E640"),sQuery(id+"F15.wireOp",EDGE,"E641"),sQuery(id+"F15.wireOp",EDGE,"E642"),sQuery(id+"F15.wireOp",EDGE,"E643"),sQuery(id+"F15.wireOp",EDGE,"E644"),sQuery(id+"F15.wireOp",EDGE,"E645"),sQuery(id+"F15.wireOp",EDGE,"E646"),sQuery(id+"F15.wireOp",EDGE,"E647"),sQuery(id+"F15.wireOp",EDGE,"E648"),sQuery(id+"F15.wireOp",EDGE,"E649"),sQuery(id+"F15.wireOp",EDGE,"E650"),sQuery(id+"F15.wireOp",EDGE,"E651"),sQuery(id+"F15.wireOp",EDGE,"E652"),sQuery(id+"F15.wireOp",EDGE,"E653"),sQuery(id+"F15.wireOp",EDGE,"E654"),sQuery(id+"F15.wireOp",EDGE,"E655"),sQuery(id+"F15.wireOp",EDGE,"E656"),sQuery(id+"F15.wireOp",EDGE,"E657"),sQuery(id+"F15.wireOp",EDGE,"E658"),sQuery(id+"F15.wireOp",EDGE,"E659"),sQuery(id+"F15.wireOp",EDGE,"E660"),sQuery(id+"F15.wireOp",EDGE,"E661"),sQuery(id+"F15.wireOp",EDGE,"E662"),sQuery(id+"F15.wireOp",EDGE,"E663"),sQuery(id+"F15.wireOp",EDGE,"E664"),sQuery(id+"F15.wireOp",EDGE,"E665"),sQuery(id+"F15.wireOp",EDGE,"E666"),sQuery(id+"F15.wireOp",EDGE,"E667"),sQuery(id+"F15.wireOp",EDGE,"E668"),sQuery(id+"F15.wireOp",EDGE,"E669"),sQuery(id+"F15.wireOp",EDGE,"E670"),sQuery(id+"F15.wireOp",EDGE,"E671"),sQuery(id+"F15.wireOp",EDGE,"E672"),sQuery(id+"F15.wireOp",EDGE,"E673"),sQuery(id+"F15.wireOp",EDGE,"E674"),sQuery(id+"F15.wireOp",EDGE,"E675"),sQuery(id+"F15.wireOp",EDGE,"E676"),sQuery(id+"F15.wireOp",EDGE,"E677"),sQuery(id+"F15.wireOp",EDGE,"E678"),sQuery(id+"F15.wireOp",EDGE,"E679"),sQuery(id+"F15.wireOp",EDGE,"E680"),sQuery(id+"F15.wireOp",EDGE,"E681"),sQuery(id+"F15.wireOp",EDGE,"E682"),sQuery(id+"F15.wireOp",EDGE,"E683"),sQuery(id+"F15.wireOp",EDGE,"E684"),sQuery(id+"F15.wireOp",EDGE,"E685"),sQuery(id+"F15.wireOp",EDGE,"E686"),sQuery(id+"F15.wireOp",EDGE,"E687"),sQuery(id+"F15.wireOp",EDGE,"E688"),sQuery(id+"F15.wireOp",EDGE,"E689"),sQuery(id+"F15.wireOp",EDGE,"E690"),sQuery(id+"F15.wireOp",EDGE,"E691"),sQuery(id+"F15.wireOp",EDGE,"E692"),sQuery(id+"F15.wireOp",EDGE,"E693"),sQuery(id+"F15.wireOp",EDGE,"E694"),sQuery(id+"F15.wireOp",EDGE,"E695"),sQuery(id+"F15.wireOp",EDGE,"E696"),sQuery(id+"F15.wireOp",EDGE,"E697"),sQuery(id+"F15.wireOp",EDGE,"E698"),sQuery(id+"F15.wireOp",EDGE,"E699"),sQuery(id+"F15.wireOp",EDGE,"E700"),sQuery(id+"F15.wireOp",EDGE,"E701"),sQuery(id+"F15.wireOp",EDGE,"E702"),sQuery(id+"F15.wireOp",EDGE,"E703"),sQuery(id+"F15.wireOp",EDGE,"E704"),sQuery(id+"F15.wireOp",EDGE,"E705"),sQuery(id+"F15.wireOp",EDGE,"E706"),sQuery(id+"F15.wireOp",EDGE,"E707"),sQuery(id+"F15.wireOp",EDGE,"E708"),sQuery(id+"F15.wireOp",EDGE,"E709"),sQuery(id+"F15.wireOp",EDGE,"E710"),sQuery(id+"F15.wireOp",EDGE,"E711"),sQuery(id+"F15.wireOp",EDGE,"E712"),sQuery(id+"F15.wireOp",EDGE,"E713"),sQuery(id+"F15.wireOp",EDGE,"E714"),sQuery(id+"F15.wireOp",EDGE,"E715"),sQuery(id+"F15.wireOp",EDGE,"E716"),sQuery(id+"F15.wireOp",EDGE,"E717"),sQuery(id+"F15.wireOp",EDGE,"E718"),sQuery(id+"F15.wireOp",EDGE,"E719"),sQuery(id+"F15.wireOp",EDGE,"E720"),sQuery(id+"F15.wireOp",EDGE,"E721"),sQuery(id+"F15.wireOp",EDGE,"E722"),sQuery(id+"F15.wireOp",EDGE,"E723"),sQuery(id+"F15.wireOp",EDGE,"E724"),sQuery(id+"F15.wireOp",EDGE,"E725"),sQuery(id+"F15.wireOp",EDGE,"E726"),sQuery(id+"F15.wireOp",EDGE,"E727"),sQuery(id+"F15.wireOp",EDGE,"E728"),sQuery(id+"F15.wireOp",EDGE,"E729"),sQuery(id+"F15.wireOp",EDGE,"E730"),sQuery(id+"F15.wireOp",EDGE,"E731"),sQuery(id+"F15.wireOp",EDGE,"E732"),sQuery(id+"F15.wireOp",EDGE,"E733"),sQuery(id+"F15.wireOp",EDGE,"E734"),sQuery(id+"F15.wireOp",EDGE,"E735"),sQuery(id+"F15.wireOp",EDGE,"E736"),sQuery(id+"F15.wireOp",EDGE,"E737"),sQuery(id+"F15.wireOp",EDGE,"E738"),sQuery(id+"F15.wireOp",EDGE,"E739"),sQuery(id+"F15.wireOp",EDGE,"E740"),sQuery(id+"F15.wireOp",EDGE,"E741"),sQuery(id+"F15.wireOp",EDGE,"E742"),sQuery(id+"F15.wireOp",EDGE,"E743"),sQuery(id+"F15.wireOp",EDGE,"E744"),sQuery(id+"F15.wireOp",EDGE,"E745"),sQuery(id+"F15.wireOp",EDGE,"E746"),sQuery(id+"F15.wireOp",EDGE,"E747"),sQuery(id+"F15.wireOp",EDGE,"E748"),sQuery(id+"F15.wireOp",EDGE,"E749"),sQuery(id+"F15.wireOp",EDGE,"E750"),sQuery(id+"F15.wireOp",EDGE,"E751"),sQuery(id+"F15.wireOp",EDGE,"E752"),sQuery(id+"F15.wireOp",EDGE,"E753"),sQuery(id+"F15.wireOp",EDGE,"E754"),sQuery(id+"F15.wireOp",EDGE,"E755"),sQuery(id+"F15.wireOp",EDGE,"E756"),sQuery(id+"F15.wireOp",EDGE,"E757"),sQuery(id+"F15.wireOp",EDGE,"E758"),sQuery(id+"F15.wireOp",EDGE,"E759"),sQuery(id+"F15.wireOp",EDGE,"E760"),sQuery(id+"F15.wireOp",EDGE,"E761"),sQuery(id+"F15.wireOp",EDGE,"E762"),sQuery(id+"F15.wireOp",EDGE,"E763"),sQuery(id+"F15.wireOp",EDGE,"E764"),sQuery(id+"F15.wireOp",EDGE,"E765"),sQuery(id+"F15.wireOp",EDGE,"E766"),sQuery(id+"F15.wireOp",EDGE,"E767"),sQuery(id+"F15.wireOp",EDGE,"E768"),sQuery(id+"F15.wireOp",EDGE,"E769"),sQuery(id+"F15.wireOp",EDGE,"E770"),sQuery(id+"F15.wireOp",EDGE,"E771"),sQuery(id+"F15.wireOp",EDGE,"E772"),sQuery(id+"F15.wireOp",EDGE,"E773"),sQuery(id+"F15.wireOp",EDGE,"E774"),sQuery(id+"F15.wireOp",EDGE,"E775"),sQuery(id+"F15.wireOp",EDGE,"E776"),sQuery(id+"F15.wireOp",EDGE,"E777"),sQuery(id+"F15.wireOp",EDGE,"E778"),sQuery(id+"F15.wireOp",EDGE,"E779"),sQuery(id+"F15.wireOp",EDGE,"E780"),sQuery(id+"F15.wireOp",EDGE,"E781"),sQuery(id+"F15.wireOp",EDGE,"E782"),sQuery(id+"F15.wireOp",EDGE,"E783"),sQuery(id+"F15.wireOp",EDGE,"E784"),sQuery(id+"F15.wireOp",EDGE,"E785"),sQuery(id+"F15.wireOp",EDGE,"E786"),sQuery(id+"F15.wireOp",EDGE,"E787"),sQuery(id+"F15.wireOp",EDGE,"E788"),sQuery(id+"F15.wireOp",EDGE,"E789"),sQuery(id+"F15.wireOp",EDGE,"E790"),sQuery(id+"F15.wireOp",EDGE,"E791"),sQuery(id+"F15.wireOp",EDGE,"E792"),sQuery(id+"F15.wireOp",EDGE,"E793"),sQuery(id+"F15.wireOp",EDGE,"E794"),sQuery(id+"F15.wireOp",EDGE,"E795"),sQuery(id+"F15.wireOp",EDGE,"E796"),sQuery(id+"F15.wireOp",EDGE,"E797"),sQuery(id+"F15.wireOp",EDGE,"E798"),sQuery(id+"F15.wireOp",EDGE,"E799"),sQuery(id+"F15.wireOp",EDGE,"E800"),sQuery(id+"F15.wireOp",EDGE,"E801"),sQuery(id+"F15.wireOp",EDGE,"E802"),sQuery(id+"F15.wireOp",EDGE,"E803"),sQuery(id+"F15.wireOp",EDGE,"E804"),sQuery(id+"F15.wireOp",EDGE,"E805"),sQuery(id+"F15.wireOp",EDGE,"E806"),sQuery(id+"F15.wireOp",EDGE,"E807"),sQuery(id+"F15.wireOp",EDGE,"E808"),sQuery(id+"F15.wireOp",EDGE,"E809"),sQuery(id+"F15.wireOp",EDGE,"E810"),sQuery(id+"F15.wireOp",EDGE,"E811"),sQuery(id+"F15.wireOp",EDGE,"E812"),sQuery(id+"F15.wireOp",EDGE,"E813"),sQuery(id+"F15.wireOp",EDGE,"E814"),sQuery(id+"F15.wireOp",EDGE,"E815"),sQuery(id+"F15.wireOp",EDGE,"E816"),sQuery(id+"F15.wireOp",EDGE,"E817"),sQuery(id+"F15.wireOp",EDGE,"E818"),sQuery(id+"F15.wireOp",EDGE,"E819"),sQuery(id+"F15.wireOp",EDGE,"E820"),sQuery(id+"F15.wireOp",EDGE,"E821"),sQuery(id+"F15.wireOp",EDGE,"E822"),sQuery(id+"F15.wireOp",EDGE,"E823"),sQuery(id+"F15.wireOp",EDGE,"E824"),sQuery(id+"F15.wireOp",EDGE,"E825"),sQuery(id+"F15.wireOp",EDGE,"E826"),sQuery(id+"F15.wireOp",EDGE,"E827"),sQuery(id+"F15.wireOp",EDGE,"E828"),sQuery(id+"F15.wireOp",EDGE,"E829"),sQuery(id+"F15.wireOp",EDGE,"E830"),sQuery(id+"F15.wireOp",EDGE,"E831"),sQuery(id+"F15.wireOp",EDGE,"E832"),sQuery(id+"F15.wireOp",EDGE,"E833"),sQuery(id+"F15.wireOp",EDGE,"E834"),sQuery(id+"F15.wireOp",EDGE,"E835"),sQuery(id+"F15.wireOp",EDGE,"E836"),sQuery(id+"F15.wireOp",EDGE,"E837"),sQuery(id+"F15.wireOp",EDGE,"E838"),sQuery(id+"F15.wireOp",EDGE,"E839"),sQuery(id+"F15.wireOp",EDGE,"E840"),sQuery(id+"F15.wireOp",EDGE,"E841"),sQuery(id+"F15.wireOp",EDGE,"E842"),sQuery(id+"F15.wireOp",EDGE,"E843"),sQuery(id+"F15.wireOp",EDGE,"E844"),sQuery(id+"F15.wireOp",EDGE,"E845"),sQuery(id+"F15.wireOp",EDGE,"E846"),sQuery(id+"F15.wireOp",EDGE,"E847"),sQuery(id+"F15.wireOp",EDGE,"E848"),sQuery(id+"F15.wireOp",EDGE,"E849"),sQuery(id+"F15.wireOp",EDGE,"E849"),sQuery(id+"F15.wireOp",EDGE,"E850"),sQuery(id+"F15.wireOp",EDGE,"E851"),sQuery(id+"F15.wireOp",EDGE,"E852"),sQuery(id+"F15.wireOp",EDGE,"E853"),sQuery(id+"F15.wireOp",EDGE,"E854"),sQuery(id+"F15.wireOp",EDGE,"E855"),sQuery(id+"F15.wireOp",EDGE,"E856"),sQuery(id+"F15.wireOp",EDGE,"E857"),sQuery(id+"F15.wireOp",EDGE,"E858"),sQuery(id+"F15.wireOp",EDGE,"E859"),sQuery(id+"F15.wireOp",EDGE,"E860"),sQuery(id+"F15.wireOp",EDGE,"E861"),sQuery(id+"F15.wireOp",EDGE,"E862"),sQuery(id+"F15.wireOp",EDGE,"E863"),sQuery(id+"F15.wireOp",EDGE,"E864"),sQuery(id+"F15.wireOp",EDGE,"E865"),sQuery(id+"F15.wireOp",EDGE,"E866"),sQuery(id+"F15.wireOp",EDGE,"E867"),sQuery(id+"F15.wireOp",EDGE,"E868"),sQuery(id+"F15.wireOp",EDGE,"E869"),sQuery(id+"F15.wireOp",EDGE,"E870"),sQuery(id+"F15.wireOp",EDGE,"E871"),sQuery(id+"F15.wireOp",EDGE,"E872"),sQuery(id+"F15.wireOp",EDGE,"E873"),sQuery(id+"F15.wireOp",EDGE,"E874"),sQuery(id+"F15.wireOp",EDGE,"E875"),sQuery(id+"F15.wireOp",EDGE,"E876"),sQuery(id+"F15.wireOp",EDGE,"E877"),sQuery(id+"F15.wireOp",EDGE,"E878"),sQuery(id+"F15.wireOp",EDGE,"E879"),sQuery(id+"F15.wireOp",EDGE,"E880"),sQuery(id+"F15.wireOp",EDGE,"E881"),sQuery(id+"F15.wireOp",EDGE,"E882"),sQuery(id+"F15.wireOp",EDGE,"E883"),sQuery(id+"F15.wireOp",EDGE,"E884"),sQuery(id+"F15.wireOp",EDGE,"E885"),sQuery(id+"F15.wireOp",EDGE,"E886"),sQuery(id+"F15.wireOp",EDGE,"E887"),sQuery(id+"F15.wireOp",EDGE,"E888"),sQuery(id+"F15.wireOp",EDGE,"E889"),sQuery(id+"F15.wireOp",EDGE,"E890"),sQuery(id+"F15.wireOp",EDGE,"E891"),sQuery(id+"F15.wireOp",EDGE,"E892"),sQuery(id+"F15.wireOp",EDGE,"E893"),sQuery(id+"F15.wireOp",EDGE,"E894"),sQuery(id+"F15.wireOp",EDGE,"E895"),sQuery(id+"F15.wireOp",EDGE,"E896"),sQuery(id+"F15.wireOp",EDGE,"E897"),sQuery(id+"F15.wireOp",EDGE,"E898"),sQuery(id+"F15.wireOp",EDGE,"E899"),sQuery(id+"F15.wireOp",EDGE,"E900"),sQuery(id+"F15.wireOp",EDGE,"E901"),sQuery(id+"F15.wireOp",EDGE,"E902"),sQuery(id+"F15.wireOp",EDGE,"E903"),sQuery(id+"F15.wireOp",EDGE,"E904"),sQuery(id+"F15.wireOp",EDGE,"E905"),sQuery(id+"F15.wireOp",EDGE,"E906"),sQuery(id+"F15.wireOp",EDGE,"E907"),sQuery(id+"F15.wireOp",EDGE,"E908"),sQuery(id+"F15.wireOp",EDGE,"E909"),sQuery(id+"F15.wireOp",EDGE,"E910"),sQuery(id+"F15.wireOp",EDGE,"E911"),sQuery(id+"F15.wireOp",EDGE,"E912"),sQuery(id+"F15.wireOp",EDGE,"E913"),sQuery(id+"F15.wireOp",EDGE,"E914"),sQuery(id+"F15.wireOp",EDGE,"E915"),sQuery(id+"F15.wireOp",EDGE,"E916"),sQuery(id+"F15.wireOp",EDGE,"E917"),sQuery(id+"F15.wireOp",EDGE,"E918"),sQuery(id+"F15.wireOp",EDGE,"E919"),sQuery(id+"F15.wireOp",EDGE,"E920"),sQuery(id+"F15.wireOp",EDGE,"E921"),sQuery(id+"F15.wireOp",EDGE,"E922"),sQuery(id+"F15.wireOp",EDGE,"E923"),sQuery(id+"F15.wireOp",EDGE,"E924"),sQuery(id+"F15.wireOp",EDGE,"E925"),sQuery(id+"F15.wireOp",EDGE,"E926"),sQuery(id+"F15.wireOp",EDGE,"E927"),sQuery(id+"F15.wireOp",EDGE,"E928"),sQuery(id+"F15.wireOp",EDGE,"E929"),sQuery(id+"F15.wireOp",EDGE,"E930"),sQuery(id+"F15.wireOp",EDGE,"E931"),sQuery(id+"F15.wireOp",EDGE,"E932"),sQuery(id+"F15.wireOp",EDGE,"E933"),sQuery(id+"F15.wireOp",EDGE,"E934"),sQuery(id+"F15.wireOp",EDGE,"E935"),sQuery(id+"F15.wireOp",EDGE,"E936"),sQuery(id+"F15.wireOp",EDGE,"E937"),sQuery(id+"F15.wireOp",EDGE,"E938"),sQuery(id+"F15.wireOp",EDGE,"E939"),sQuery(id+"F15.wireOp",EDGE,"E940"),sQuery(id+"F15.wireOp",EDGE,"E941"),sQuery(id+"F15.wireOp",EDGE,"E942"),sQuery(id+"F15.wireOp",EDGE,"E943"),sQuery(id+"F15.wireOp",EDGE,"E944"),sQuery(id+"F15.wireOp",EDGE,"E945"),sQuery(id+"F15.wireOp",EDGE,"E946"),sQuery(id+"F15.wireOp",EDGE,"E947"),sQuery(id+"F15.wireOp",EDGE,"E948"),sQuery(id+"F15.wireOp",EDGE,"E949"),sQuery(id+"F15.wireOp",EDGE,"E950"),sQuery(id+"F15.wireOp",EDGE,"E951"),sQuery(id+"F15.wireOp",EDGE,"E952"),sQuery(id+"F15.wireOp",EDGE,"E953"),sQuery(id+"F15.wireOp",EDGE,"E954"),sQuery(id+"F15.wireOp",EDGE,"E955"),sQuery(id+"F15.wireOp",EDGE,"E956"),sQuery(id+"F15.wireOp",EDGE,"E957"),sQuery(id+"F15.wireOp",EDGE,"E958"),sQuery(id+"F15.wireOp",EDGE,"E959"),sQuery(id+"F15.wireOp",EDGE,"E960"),sQuery(id+"F15.wireOp",EDGE,"E961"),sQuery(id+"F15.wireOp",EDGE,"E962"),sQuery(id+"F15.wireOp",EDGE,"E963"),sQuery(id+"F15.wireOp",EDGE,"E964"),sQuery(id+"F15.wireOp",EDGE,"E965"),sQuery(id+"F15.wireOp",EDGE,"E966"),sQuery(id+"F15.wireOp",EDGE,"E967"),sQuery(id+"F15.wireOp",EDGE,"E968"),sQuery(id+"F15.wireOp",EDGE,"E969"),sQuery(id+"F15.wireOp",EDGE,"E970"),sQuery(id+"F15.wireOp",EDGE,"E971"),sQuery(id+"F15.wireOp",EDGE,"E972"),sQuery(id+"F15.wireOp",EDGE,"E973"),sQuery(id+"F15.wireOp",EDGE,"E974"),sQuery(id+"F15.wireOp",EDGE,"E975"),sQuery(id+"F15.wireOp",EDGE,"E976"),sQuery(id+"F15.wireOp",EDGE,"E977"),sQuery(id+"F15.wireOp",EDGE,"E978"),sQuery(id+"F15.wireOp",EDGE,"E979"),sQuery(id+"F15.wireOp",EDGE,"E980"),sQuery(id+"F15.wireOp",EDGE,"E981"),sQuery(id+"F15.wireOp",EDGE,"E982"),sQuery(id+"F15.wireOp",EDGE,"E983"),sQuery(id+"F15.wireOp",EDGE,"E984"),sQuery(id+"F15.wireOp",EDGE,"E985"),sQuery(id+"F15.wireOp",EDGE,"E986"),sQuery(id+"F15.wireOp",EDGE,"E987"),sQuery(id+"F15.wireOp",EDGE,"E988"),sQuery(id+"F15.wireOp",EDGE,"E989"),sQuery(id+"F15.wireOp",EDGE,"E990"),sQuery(id+"F15.wireOp",EDGE,"E991"),sQuery(id+"F15.wireOp",EDGE,"E992"),sQuery(id+"F15.wireOp",EDGE,"E993"),sQuery(id+"F15.wireOp",EDGE,"E994"),sQuery(id+"F15.wireOp",EDGE,"E995"),sQuery(id+"F15.wireOp",EDGE,"E996"),sQuery(id+"F15.wireOp",EDGE,"E997"),sQuery(id+"F15.wireOp",EDGE,"E998"),sQuery(id+"F15.wireOp",EDGE,"E999"),sQuery(id+"F15.wireOp",EDGE,"E1000"),sQuery(id+"F15.wireOp",EDGE,"E1001"),sQuery(id+"F15.wireOp",EDGE,"E1002"),sQuery(id+"F15.wireOp",EDGE,"E1003"),sQuery(id+"F15.wireOp",EDGE,"E1004"),sQuery(id+"F15.wireOp",EDGE,"E1005"),sQuery(id+"F15.wireOp",EDGE,"E1006"),sQuery(id+"F15.wireOp",EDGE,"E1007"),sQuery(id+"F15.wireOp",EDGE,"E1008"),sQuery(id+"F15.wireOp",EDGE,"E1009"),sQuery(id+"F15.wireOp",EDGE,"E1010"),sQuery(id+"F15.wireOp",EDGE,"E1011"),sQuery(id+"F15.wireOp",EDGE,"E1012"),sQuery(id+"F15.wireOp",EDGE,"E1013"),sQuery(id+"F15.wireOp",EDGE,"E1014"),sQuery(id+"F15.wireOp",EDGE,"E1015"),sQuery(id+"F15.wireOp",EDGE,"E1016"),sQuery(id+"F15.wireOp",EDGE,"E1017"),sQuery(id+"F15.wireOp",EDGE,"E1018"),sQuery(id+"F15.wireOp",EDGE,"E1019"),sQuery(id+"F15.wireOp",EDGE,"E1020"),sQuery(id+"F15.wireOp",EDGE,"E1021"),sQuery(id+"F15.wireOp",EDGE,"E1022"),sQuery(id+"F15.wireOp",EDGE,"E1023"),sQuery(id+"F15.wireOp",EDGE,"E1024"),sQuery(id+"F15.wireOp",EDGE,"E1025"),sQuery(id+"F15.wireOp",EDGE,"E1026"),sQuery(id+"F15.wireOp",EDGE,"E1027"),sQuery(id+"F15.wireOp",EDGE,"E1028"),sQuery(id+"F15.wireOp",EDGE,"E1029"),sQuery(id+"F15.wireOp",EDGE,"E1030"),sQuery(id+"F15.wireOp",EDGE,"E1031"),sQuery(id+"F15.wireOp",EDGE,"E1032"),sQuery(id+"F15.wireOp",EDGE,"E1033"),sQuery(id+"F15.wireOp",EDGE,"E1034"),sQuery(id+"F15.wireOp",EDGE,"E1035"),sQuery(id+"F15.wireOp",EDGE,"E1036"),sQuery(id+"F15.wireOp",EDGE,"E1037"),sQuery(id+"F15.wireOp",EDGE,"E1038"),sQuery(id+"F15.wireOp",EDGE,"E1039"),sQuery(id+"F15.wireOp",EDGE,"E1040"),sQuery(id+"F15.wireOp",EDGE,"E1041"),sQuery(id+"F15.wireOp",EDGE,"E1042"),sQuery(id+"F15.wireOp",EDGE,"E1043"),sQuery(id+"F15.wireOp",EDGE,"E1044"),sQuery(id+"F15.wireOp",EDGE,"E1045"),sQuery(id+"F15.wireOp",EDGE,"E1046"),sQuery(id+"F15.wireOp",EDGE,"E1047"),sQuery(id+"F15.wireOp",EDGE,"E1048"),sQuery(id+"F15.wireOp",EDGE,"E1049"),sQuery(id+"F15.wireOp",EDGE,"E1050"),sQuery(id+"F15.wireOp",EDGE,"E1051"),sQuery(id+"F15.wireOp",EDGE,"E1052"),sQuery(id+"F15.wireOp",EDGE,"E1053"),sQuery(id+"F15.wireOp",EDGE,"E1054"),sQuery(id+"F15.wireOp",EDGE,"E1055"),sQuery(id+"F15.wireOp",EDGE,"E1056"),sQuery(id+"F15.wireOp",EDGE,"E1057"),sQuery(id+"F15.wireOp",EDGE,"E1058"),sQuery(id+"F15.wireOp",EDGE,"E1059"),sQuery(id+"F15.wireOp",EDGE,"E1060"),sQuery(id+"F15.wireOp",EDGE,"E1061"),sQuery(id+"F15.wireOp",EDGE,"E1062"),sQuery(id+"F15.wireOp",EDGE,"E1063"),sQuery(id+"F15.wireOp",EDGE,"E1064"),sQuery(id+"F15.wireOp",EDGE,"E1065"),sQuery(id+"F15.wireOp",EDGE,"E1066"),sQuery(id+"F15.wireOp",EDGE,"E1067"),sQuery(id+"F15.wireOp",EDGE,"E1068"),sQuery(id+"F15.wireOp",EDGE,"E1069"),sQuery(id+"F15.wireOp",EDGE,"E1070"),sQuery(id+"F15.wireOp",EDGE,"E1071"),sQuery(id+"F15.wireOp",EDGE,"E1072"),sQuery(id+"F15.wireOp",EDGE,"E1073"),sQuery(id+"F15.wireOp",EDGE,"E1074"),sQuery(id+"F15.wireOp",EDGE,"E1075"),sQuery(id+"F15.wireOp",EDGE,"E1076"),sQuery(id+"F15.wireOp",EDGE,"E1077"),sQuery(id+"F15.wireOp",EDGE,"E1078"),sQuery(id+"F15.wireOp",EDGE,"E1079"),sQuery(id+"F15.wireOp",EDGE,"E1080"),sQuery(id+"F15.wireOp",EDGE,"E1081"),sQuery(id+"F15.wireOp",EDGE,"E1082"),sQuery(id+"F15.wireOp",EDGE,"E1083"),sQuery(id+"F15.wireOp",EDGE,"E1084"),sQuery(id+"F15.wireOp",EDGE,"E1085"),sQuery(id+"F15.wireOp",EDGE,"E1086"),sQuery(id+"F15.wireOp",EDGE,"E1087"),sQuery(id+"F15.wireOp",EDGE,"E1088"),sQuery(id+"F15.wireOp",EDGE,"E1089"),sQuery(id+"F15.wireOp",EDGE,"E1090"),sQuery(id+"F15.wireOp",EDGE,"E1091"),sQuery(id+"F15.wireOp",EDGE,"E1092"),sQuery(id+"F15.wireOp",EDGE,"E1093"),sQuery(id+"F15.wireOp",EDGE,"E1094"),sQuery(id+"F15.wireOp",EDGE,"E1095"),sQuery(id+"F15.wireOp",EDGE,"E1096"),sQuery(id+"F15.wireOp",EDGE,"E1097"),sQuery(id+"F15.wireOp",EDGE,"E1098"),sQuery(id+"F15.wireOp",EDGE,"E1099"),sQuery(id+"F15.wireOp",EDGE,"E1100"),sQuery(id+"F15.wireOp",EDGE,"E1101"),sQuery(id+"F15.wireOp",EDGE,"E1102"),sQuery(id+"F15.wireOp",EDGE,"E1103"),sQuery(id+"F15.wireOp",EDGE,"E1104"),sQuery(id+"F15.wireOp",EDGE,"E1105"),sQuery(id+"F15.wireOp",EDGE,"E1106"),sQuery(id+"F15.wireOp",EDGE,"E1107"),sQuery(id+"F15.wireOp",EDGE,"E1108"),sQuery(id+"F15.wireOp",EDGE,"E1109"),sQuery(id+"F15.wireOp",EDGE,"E1110"),sQuery(id+"F15.wireOp",EDGE,"E1111"),sQuery(id+"F15.wireOp",EDGE,"E1112"),sQuery(id+"F15.wireOp",EDGE,"E1113"),sQuery(id+"F15.wireOp",EDGE,"E1114"),sQuery(id+"F15.wireOp",EDGE,"E1115"),sQuery(id+"F15.wireOp",EDGE,"E1116"),sQuery(id+"F15.wireOp",EDGE,"E1117"),sQuery(id+"F15.wireOp",EDGE,"E1118"),sQuery(id+"F15.wireOp",EDGE,"E1119"),sQuery(id+"F15.wireOp",EDGE,"E1120"),sQuery(id+"F15.wireOp",EDGE,"E1121"),sQuery(id+"F15.wireOp",EDGE,"E1122"),sQuery(id+"F15.wireOp",EDGE,"E1123"),sQuery(id+"F15.wireOp",EDGE,"E1124"),sQuery(id+"F15.wireOp",EDGE,"E1125"),sQuery(id+"F15.wireOp",EDGE,"E1126"),sQuery(id+"F15.wireOp",EDGE,"E1127"),sQuery(id+"F15.wireOp",EDGE,"E1128"),sQuery(id+"F15.wireOp",EDGE,"E1128"),sQuery(id+"F15.wireOp",EDGE,"E1129"),sQuery(id+"F15.wireOp",EDGE,"E1130")])],"isStart":false}),makeQuery(id+"F22.opExtrude","CAP_FACE",FACE,{"disambiguationData":[OSD([sQuery(id+"F21.wireOp",EDGE,"E1132"),sQuery(id+"F21.wireOp",EDGE,"E1133")])],"isStart":true})]});
            var sketch = newSketch(context, id + "F24", { "sketchPlane" : qUnion([Q0])});
            skLineSegment(sketch, "E1134", {"start": v(-1.23, 4.07) * mm, "end": v(-0.8, 5.27) * mm});
            skLineSegment(sketch, "E1135", {"start": v(-0.8, 5.27) * mm, "end": v(-0.46, 5.3) * mm});
            skLineSegment(sketch, "E1136", {"start": v(-0.46, 5.3) * mm, "end": v(0.26, 4.24) * mm});
            skLineSegment(sketch, "E1137", {"start": v(0.26, 4.24) * mm, "end": v(0.26, 5.75) * mm});
            skLineSegment(sketch, "E1138", {"start": v(0.26, 5.75) * mm, "end": v(-1.64, 5.73) * mm});
            skLineSegment(sketch, "E1139", {"start": v(-1.64, 5.73) * mm, "end": v(-1.25, 4.07) * mm});
            skLineSegment(sketch, "E1140", {"start": v(-1.25, 4.07) * mm, "end": v(-1.23, 4.07) * mm});
            skLineSegment(sketch, "E1141", {"start": v(-1.23, 4.07) * mm, "end": v(-1.23, 4.07) * mm});
            skLineSegment(sketch, "E1142.1.0", {"start": v(-2.29, 3.58) * mm, "end": v(-3.17, 4.8) * mm});
            skLineSegment(sketch, "E1142.1.1", {"start": v(-3.17, 4.8) * mm, "end": v(-4.7, 3.67) * mm});
            skLineSegment(sketch, "E1142.1.2", {"start": v(-4.7, 3.67) * mm, "end": v(-3.4, 2.55) * mm});
            skLineSegment(sketch, "E1142.1.3", {"start": v(-3.4, 2.57) * mm, "end": v(-3.74, 3.8) * mm});
            skLineSegment(sketch, "E1142.1.4", {"start": v(-3.74, 3.8) * mm, "end": v(-3.5, 4.03) * mm});
            skLineSegment(sketch, "E1142.1.5", {"start": v(-3.5, 4.03) * mm, "end": v(-2.29, 3.58) * mm});
            skLineSegment(sketch, "E1142.2.0", {"start": v(-3.96, 1.56) * mm, "end": v(-5.4, 2.02) * mm});
            skLineSegment(sketch, "E1142.2.1", {"start": v(-5.4, 2.02) * mm, "end": v(-5.95, 0.21) * mm});
            skLineSegment(sketch, "E1142.2.2", {"start": v(-5.95, 0.21) * mm, "end": v(-4.25, 0.07) * mm});
            skLineSegment(sketch, "E1142.2.3", {"start": v(-4.26, 0.09) * mm, "end": v(-5.26, 0.87) * mm});
            skLineSegment(sketch, "E1142.2.4", {"start": v(-5.26, 0.87) * mm, "end": v(-5.2, 1.2) * mm});
            skLineSegment(sketch, "E1142.2.5", {"start": v(-5.2, 1.2) * mm, "end": v(-3.96, 1.56) * mm});
            skLineSegment(sketch, "E1142.3.0", {"start": v(-4.11, -1.07) * mm, "end": v(-5.55, -1.53) * mm});
            skLineSegment(sketch, "E1142.3.1", {"start": v(-5.55, -1.53) * mm, "end": v(-4.94, -3.33) * mm});
            skLineSegment(sketch, "E1142.3.2", {"start": v(-4.94, -3.33) * mm, "end": v(-3.48, -2.45) * mm});
            skLineSegment(sketch, "E1142.3.3", {"start": v(-3.5, -2.43) * mm, "end": v(-4.77, -2.38) * mm});
            skLineSegment(sketch, "E1142.3.4", {"start": v(-4.77, -2.38) * mm, "end": v(-4.9, -2.08) * mm});
            skLineSegment(sketch, "E1142.3.5", {"start": v(-4.9, -2.08) * mm, "end": v(-4.11, -1.07) * mm});
            skLineSegment(sketch, "E1142.4.0", {"start": v(-2.7, -3.28) * mm, "end": v(-3.59, -4.5) * mm});
            skLineSegment(sketch, "E1142.4.1", {"start": v(-3.59, -4.5) * mm, "end": v(-2.04, -5.6) * mm});
            skLineSegment(sketch, "E1142.4.2", {"start": v(-2.04, -5.6) * mm, "end": v(-1.38, -4.02) * mm});
            skLineSegment(sketch, "E1142.4.3", {"start": v(-1.4, -4.02) * mm, "end": v(-2.46, -4.73) * mm});
            skLineSegment(sketch, "E1142.4.4", {"start": v(-2.46, -4.73) * mm, "end": v(-2.75, -4.57) * mm});
            skLineSegment(sketch, "E1142.4.5", {"start": v(-2.75, -4.57) * mm, "end": v(-2.7, -3.28) * mm});
            skLineSegment(sketch, "E1142.5.0", {"start": v(-0.26, -4.24) * mm, "end": v(-0.26, -5.75) * mm});
            skLineSegment(sketch, "E1142.5.1", {"start": v(-0.26, -5.75) * mm, "end": v(1.64, -5.73) * mm});
            skLineSegment(sketch, "E1142.5.2", {"start": v(1.64, -5.73) * mm, "end": v(1.25, -4.07) * mm});
            skLineSegment(sketch, "E1142.5.3", {"start": v(1.23, -4.07) * mm, "end": v(0.8, -5.27) * mm});
            skLineSegment(sketch, "E1142.5.4", {"start": v(0.8, -5.27) * mm, "end": v(0.46, -5.3) * mm});
            skLineSegment(sketch, "E1142.5.5", {"start": v(0.46, -5.3) * mm, "end": v(-0.26, -4.24) * mm});
            skLineSegment(sketch, "E1142.6.0", {"start": v(2.29, -3.58) * mm, "end": v(3.17, -4.8) * mm});
            skLineSegment(sketch, "E1142.6.1", {"start": v(3.17, -4.8) * mm, "end": v(4.7, -3.67) * mm});
            skLineSegment(sketch, "E1142.6.2", {"start": v(4.7, -3.67) * mm, "end": v(3.4, -2.55) * mm});
            skLineSegment(sketch, "E1142.6.3", {"start": v(3.4, -2.57) * mm, "end": v(3.74, -3.8) * mm});
            skLineSegment(sketch, "E1142.6.4", {"start": v(3.74, -3.8) * mm, "end": v(3.5, -4.03) * mm});
            skLineSegment(sketch, "E1142.6.5", {"start": v(3.5, -4.03) * mm, "end": v(2.29, -3.58) * mm});
            skLineSegment(sketch, "E1142.7.0", {"start": v(3.96, -1.56) * mm, "end": v(5.4, -2.02) * mm});
            skLineSegment(sketch, "E1142.7.1", {"start": v(5.4, -2.02) * mm, "end": v(5.95, -0.21) * mm});
            skLineSegment(sketch, "E1142.7.2", {"start": v(5.95, -0.21) * mm, "end": v(4.25, -0.07) * mm});
            skLineSegment(sketch, "E1142.7.3", {"start": v(4.26, -0.09) * mm, "end": v(5.26, -0.87) * mm});
            skLineSegment(sketch, "E1142.7.4", {"start": v(5.26, -0.87) * mm, "end": v(5.2, -1.2) * mm});
            skLineSegment(sketch, "E1142.7.5", {"start": v(5.2, -1.2) * mm, "end": v(3.96, -1.56) * mm});
            skLineSegment(sketch, "E1142.8.0", {"start": v(4.11, 1.07) * mm, "end": v(5.55, 1.53) * mm});
            skLineSegment(sketch, "E1142.8.1", {"start": v(5.55, 1.53) * mm, "end": v(4.94, 3.33) * mm});
            skLineSegment(sketch, "E1142.8.2", {"start": v(4.94, 3.33) * mm, "end": v(3.48, 2.45) * mm});
            skLineSegment(sketch, "E1142.8.3", {"start": v(3.5, 2.43) * mm, "end": v(4.77, 2.38) * mm});
            skLineSegment(sketch, "E1142.8.4", {"start": v(4.77, 2.38) * mm, "end": v(4.9, 2.08) * mm});
            skLineSegment(sketch, "E1142.8.5", {"start": v(4.9, 2.08) * mm, "end": v(4.11, 1.07) * mm});
            skLineSegment(sketch, "E1142.9.0", {"start": v(2.7, 3.28) * mm, "end": v(3.59, 4.5) * mm});
            skLineSegment(sketch, "E1142.9.1", {"start": v(3.59, 4.5) * mm, "end": v(2.04, 5.6) * mm});
            skLineSegment(sketch, "E1142.9.2", {"start": v(2.04, 5.6) * mm, "end": v(1.38, 4.02) * mm});
            skLineSegment(sketch, "E1142.9.3", {"start": v(1.4, 4.02) * mm, "end": v(2.46, 4.73) * mm});
            skLineSegment(sketch, "E1142.9.4", {"start": v(2.46, 4.73) * mm, "end": v(2.75, 4.57) * mm});
            skLineSegment(sketch, "E1142.9.5", {"start": v(2.75, 4.57) * mm, "end": v(2.7, 3.28) * mm});
            skPoint(sketch, "E1142.center", {"position": v(0, 0) * mm});
            skLineSegment(sketch, "E1143.1.0", {"start": v(-3.4, 2.55) * mm, "end": v(-3.39, 2.57) * mm});
            skLineSegment(sketch, "E1143.1.1", {"start": v(-3.39, 2.57) * mm, "end": v(-3.4, 2.57) * mm});
            skLineSegment(sketch, "E1143.2.0", {"start": v(-4.25, 0.07) * mm, "end": v(-4.25, 0.09) * mm});
            skLineSegment(sketch, "E1143.2.1", {"start": v(-4.25, 0.09) * mm, "end": v(-4.26, 0.09) * mm});
            skLineSegment(sketch, "E1143.3.0", {"start": v(-3.48, -2.45) * mm, "end": v(-3.5, -2.43) * mm});
            skLineSegment(sketch, "E1143.3.1", {"start": v(-3.5, -2.43) * mm, "end": v(-3.5, -2.43) * mm});
            skLineSegment(sketch, "E1143.4.0", {"start": v(-1.38, -4.02) * mm, "end": v(-1.4, -4.02) * mm});
            skLineSegment(sketch, "E1143.4.1", {"start": v(-1.4, -4.02) * mm, "end": v(-1.4, -4.02) * mm});
            skLineSegment(sketch, "E1143.5.0", {"start": v(1.25, -4.07) * mm, "end": v(1.23, -4.07) * mm});
            skLineSegment(sketch, "E1143.5.1", {"start": v(1.23, -4.07) * mm, "end": v(1.23, -4.07) * mm});
            skLineSegment(sketch, "E1143.6.0", {"start": v(3.4, -2.55) * mm, "end": v(3.39, -2.57) * mm});
            skLineSegment(sketch, "E1143.6.1", {"start": v(3.39, -2.57) * mm, "end": v(3.4, -2.57) * mm});
            skLineSegment(sketch, "E1143.7.0", {"start": v(4.25, -0.07) * mm, "end": v(4.25, -0.09) * mm});
            skLineSegment(sketch, "E1143.7.1", {"start": v(4.25, -0.09) * mm, "end": v(4.26, -0.09) * mm});
            skLineSegment(sketch, "E1143.8.0", {"start": v(3.48, 2.45) * mm, "end": v(3.5, 2.43) * mm});
            skLineSegment(sketch, "E1143.8.1", {"start": v(3.5, 2.43) * mm, "end": v(3.5, 2.43) * mm});
            skLineSegment(sketch, "E1143.9.0", {"start": v(1.38, 4.02) * mm, "end": v(1.4, 4.02) * mm});
            skLineSegment(sketch, "E1143.9.1", {"start": v(1.4, 4.02) * mm, "end": v(1.4, 4.02) * mm});
            skSolve(sketch);
        }
        {
            var Q0;
            Q0 = qSketchRegion(id + "F24", true);
            extrude(context, id + "F25", {"entities" : qUnion([Q0]), "operationType" : NewBodyOperationType.REMOVE, "oppositeDirection" : true, "depth" : 3.4 * mm, "offsetDistance" : 25 * mm});
        }
    });
